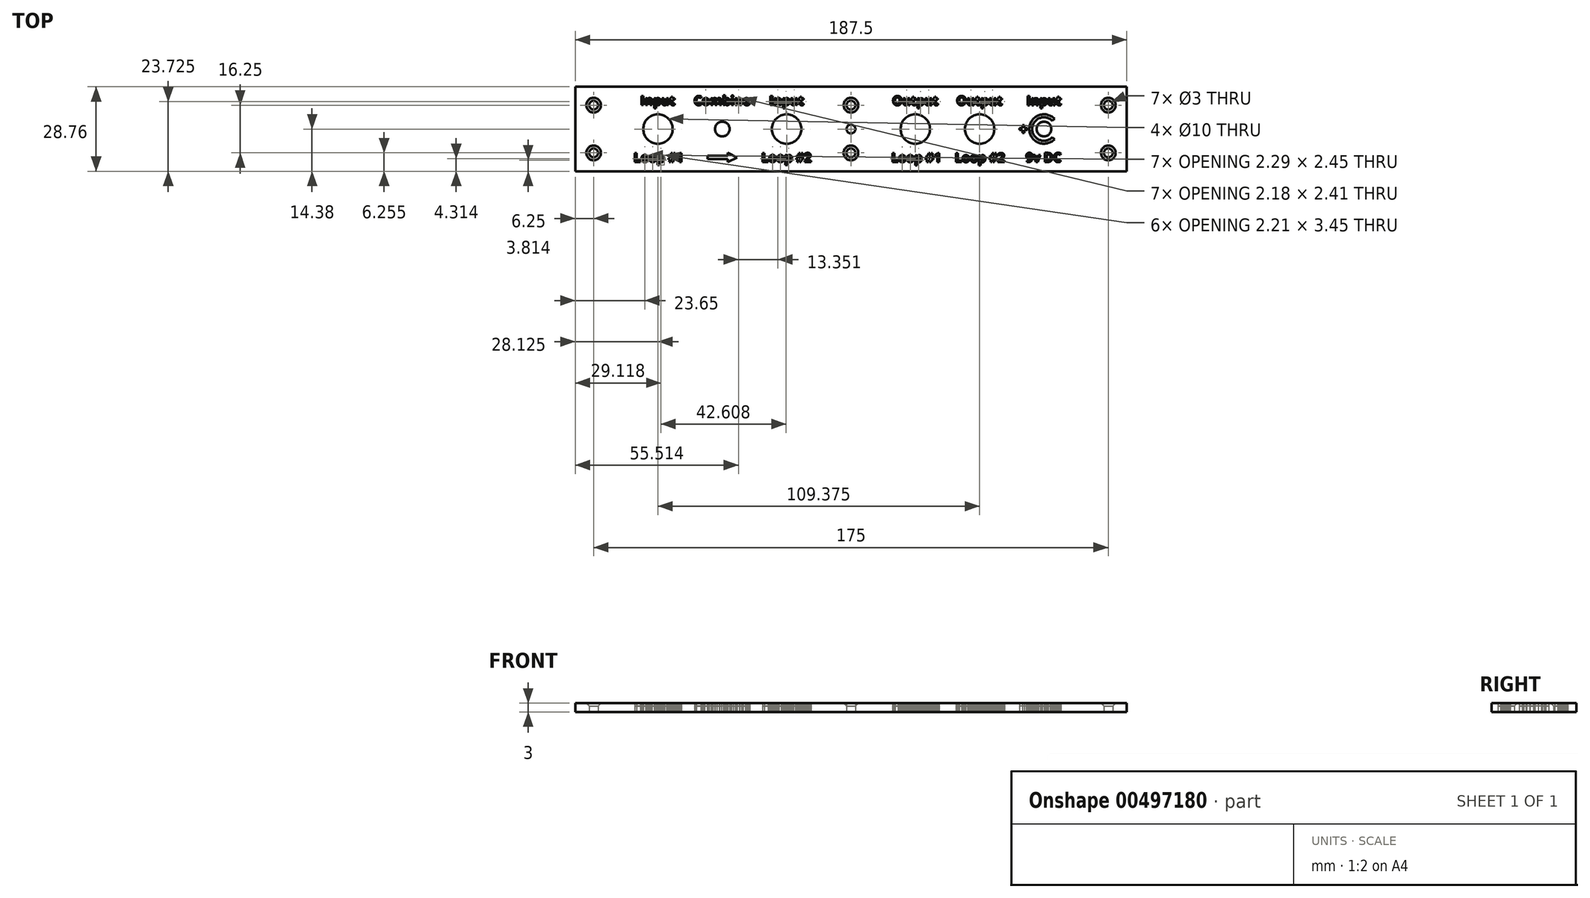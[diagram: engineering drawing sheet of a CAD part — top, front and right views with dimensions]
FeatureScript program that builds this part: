
annotation { "Feature Type Name" : "Feature", "Feature Type Description" : "" }
export const myFeature = defineFeature(function(context is Context, id is Id, definition is map)
    precondition{}
    {
        {
            var Q0;
            Q0=qCreatedBy(makeId("Top.planeOp"),FACE);
            var sketch = newSketch(context, id + "F0", { "sketchPlane" : qUnion([Q0])});
            skLineSegment(sketch, "E0.bottom", {"start": v(-93.75, 14.38) * mm, "end": v(93.75, 14.38) * mm});
            skLineSegment(sketch, "E0.top", {"start": v(-93.75, -14.37) * mm, "end": v(93.75, -14.37) * mm});
            skLineSegment(sketch, "E0.left", {"start": v(-93.75, 14.38) * mm, "end": v(-93.75, -14.37) * mm});
            skLineSegment(sketch, "E0.right", {"start": v(93.75, 14.38) * mm, "end": v(93.75, -14.37) * mm});
            skPoint(sketch, "E0.middle", {"position": v(0, 0) * mm});
            skPoint(sketch, "E1", {"position": v(-87.5, 14.38) * mm});
            skPoint(sketch, "E2", {"position": v(-87.5, -14.37) * mm});
            skPoint(sketch, "E3", {"position": v(87.5, 14.38) * mm});
            skPoint(sketch, "E4", {"position": v(87.5, -14.37) * mm});
            skPoint(sketch, "E5", {"position": v(-93.75, 8.12) * mm});
            skPoint(sketch, "E6", {"position": v(93.75, 8.13) * mm});
            skPoint(sketch, "E7", {"position": v(93.75, -8.13) * mm});
            skPoint(sketch, "E8", {"position": v(-93.75, -8.13) * mm});
            skPoint(sketch, "E9", {"position": v(-87.5, 8.12) * mm});
            skPoint(sketch, "E10", {"position": v(-87.5, -8.13) * mm});
            skPoint(sketch, "E11", {"position": v(87.5, 8.13) * mm});
            skPoint(sketch, "E12", {"position": v(87.5, -8.13) * mm});
            skLineSegment(sketch, "E13", {"start": v(-87.5, 8.12) * mm, "end": v(87.5, 8.13) * mm, "construction": true});
            skLineSegment(sketch, "E14", {"start": v(87.5, 8.13) * mm, "end": v(87.5, -8.13) * mm, "construction": true});
            skLineSegment(sketch, "E15", {"start": v(87.5, -8.13) * mm, "end": v(-87.5, -8.13) * mm, "construction": true});
            skLineSegment(sketch, "E16", {"start": v(-87.5, -8.13) * mm, "end": v(-87.5, 8.12) * mm, "construction": true});
            skPoint(sketch, "E17", {"position": v(0, 8.12) * mm});
            skPoint(sketch, "E18", {"position": v(0, -8.13) * mm});
            skLineSegment(sketch, "E19", {"start": v(0, 8.12) * mm, "end": v(0, -8.13) * mm, "construction": true});
            skPoint(sketch, "E20", {"position": v(-43.75, 8.13) * mm});
            skPoint(sketch, "E21", {"position": v(-43.75, -8.12) * mm});
            skPoint(sketch, "E22", {"position": v(43.75, 8.13) * mm});
            skPoint(sketch, "E23", {"position": v(43.75, -8.12) * mm});
            skPoint(sketch, "E24", {"position": v(-65.62, -8.12) * mm});
            skPoint(sketch, "E25", {"position": v(-65.62, 8.13) * mm});
            skPoint(sketch, "E26", {"position": v(-21.88, 8.13) * mm});
            skPoint(sketch, "E27", {"position": v(-21.88, -8.12) * mm});
            skPoint(sketch, "E28", {"position": v(21.88, 8.13) * mm});
            skPoint(sketch, "E29", {"position": v(21.88, -8.12) * mm});
            skPoint(sketch, "E30", {"position": v(65.62, 8.13) * mm});
            skPoint(sketch, "E31", {"position": v(65.62, -8.12) * mm});
            skLineSegment(sketch, "E32", {"start": v(-65.62, 8.13) * mm, "end": v(-65.62, -8.12) * mm, "construction": true});
            skLineSegment(sketch, "E33", {"start": v(-43.75, 8.12) * mm, "end": v(-43.75, -8.12) * mm, "construction": true});
            skLineSegment(sketch, "E34", {"start": v(-21.88, 8.13) * mm, "end": v(-21.88, -8.12) * mm, "construction": true});
            skLineSegment(sketch, "E35", {"start": v(21.88, 8.13) * mm, "end": v(21.88, -8.12) * mm, "construction": true});
            skLineSegment(sketch, "E36", {"start": v(43.75, 8.13) * mm, "end": v(43.75, -8.12) * mm, "construction": true});
            skLineSegment(sketch, "E37", {"start": v(65.62, 8.13) * mm, "end": v(65.62, -8.12) * mm, "construction": true});
            skPoint(sketch, "E38", {"position": v(65.62, 0) * mm});
            skPoint(sketch, "E39", {"position": v(43.75, 0) * mm});
            skPoint(sketch, "E40", {"position": v(21.88, 0) * mm});
            skPoint(sketch, "E41", {"position": v(-21.88, 0) * mm});
            skPoint(sketch, "E42", {"position": v(-43.75, 0) * mm});
            skPoint(sketch, "E43", {"position": v(-65.62, 0) * mm});
            skCircle(sketch, "E44", {"center": v(-65.62, 0) * mm, "radius": 5 * mm});
            skCircle(sketch, "E45", {"center": v(-21.88, 0) * mm, "radius": 5 * mm});
            skCircle(sketch, "E46", {"center": v(21.88, 0) * mm, "radius": 5 * mm});
            skCircle(sketch, "E47", {"center": v(43.75, 0) * mm, "radius": 5 * mm});
            skCircle(sketch, "E48", {"center": v(65.62, 0) * mm, "radius": 2.5 * mm});
            skCircle(sketch, "E49", {"center": v(0, 0) * mm, "radius": 1.5 * mm});
            skCircle(sketch, "E50", {"center": v(-43.75, 0) * mm, "radius": 2.5 * mm});
            skPoint(sketch, "E51", {"position": v(-65.62, 11.25) * mm});
            skPoint(sketch, "E52", {"position": v(-65.62, -11.25) * mm});
            skPoint(sketch, "E53", {"position": v(-43.75, -11.25) * mm});
            skPoint(sketch, "E54", {"position": v(-21.88, -11.25) * mm});
            skPoint(sketch, "E55", {"position": v(0, -11.25) * mm});
            skPoint(sketch, "E56", {"position": v(-43.75, 11.25) * mm});
            skPoint(sketch, "E57", {"position": v(-21.88, 11.25) * mm});
            skPoint(sketch, "E58", {"position": v(0, 11.25) * mm});
            skPoint(sketch, "E59", {"position": v(21.88, 11.25) * mm});
            skPoint(sketch, "E60", {"position": v(21.88, -11.25) * mm});
            skPoint(sketch, "E61", {"position": v(43.75, 11.25) * mm});
            skPoint(sketch, "E62", {"position": v(65.62, 11.25) * mm});
            skPoint(sketch, "E63", {"position": v(43.75, -11.25) * mm});
            skPoint(sketch, "E64", {"position": v(65.62, -11.25) * mm});
            skPoint(sketch, "E65", {"position": v(-73.89, -8.12) * mm});
            skPoint(sketch, "E66", {"position": v(-73.89, -11.25) * mm});
            skText(sketch, "E67", { "text": "Loop #1", "fontName": "OpenSans-Bold.ttf"});
            skPoint(sketch, "E68", {"position": v(-30.43, -8.12) * mm});
            skPoint(sketch, "E69", {"position": v(-30.43, -11.25) * mm});
            skText(sketch, "E70", { "text": "Loop #2", "fontName": "OpenSans-Bold.ttf"});
            skPoint(sketch, "E71", {"position": v(-71.6, 8.14) * mm});
            skPoint(sketch, "E72", {"position": v(-71.6, 11.27) * mm});
            skText(sketch, "E73", { "text": "Input", "fontName": "OpenSans-Bold.ttf"});
            skPoint(sketch, "E74", {"position": v(-53.43, 8.14) * mm});
            skPoint(sketch, "E75", {"position": v(-53.43, 11.27) * mm});
            skText(sketch, "E76", { "text": "Combine", "fontName": "OpenSans-Bold.ttf"});
            skPoint(sketch, "E77", {"position": v(-27.75, 8.14) * mm});
            skPoint(sketch, "E78", {"position": v(-27.75, 11.27) * mm});
            skText(sketch, "E79", { "text": "Input", "fontName": "OpenSans-Bold.ttf"});
            skPoint(sketch, "E80", {"position": v(-41.87, -8.12) * mm});
            skPoint(sketch, "E81", {"position": v(-41.87, -11.25) * mm});
            skPoint(sketch, "E82", {"position": v(-41.87, -9.12) * mm});
            skLineSegment(sketch, "E83", {"start": v(-41.87, -11.25) * mm, "end": v(-41.87, -10.25) * mm});
            skLineSegment(sketch, "E84", {"start": v(-41.87, -8.12) * mm, "end": v(-41.87, -9.12) * mm});
            skPoint(sketch, "E85", {"position": v(-48.75, -9.12) * mm});
            skPoint(sketch, "E86", {"position": v(-48.75, -10.25) * mm});
            skLineSegment(sketch, "E87", {"start": v(-41.87, -9.12) * mm, "end": v(-48.75, -9.12) * mm});
            skLineSegment(sketch, "E88", {"start": v(-41.87, -10.25) * mm, "end": v(-48.75, -10.25) * mm});
            skLineSegment(sketch, "E89", {"start": v(-48.75, -10.25) * mm, "end": v(-48.75, -9.12) * mm});
            skPoint(sketch, "E90", {"position": v(-38.75, -9.69) * mm});
            skLineSegment(sketch, "E91", {"start": v(-41.87, -8.12) * mm, "end": v(-38.75, -9.69) * mm});
            skLineSegment(sketch, "E92", {"start": v(-41.87, -11.25) * mm, "end": v(-38.75, -9.69) * mm});
            skPoint(sketch, "E93", {"position": v(-6.94, 2.58) * mm});
            skPoint(sketch, "E94", {"position": v(-6.94, 5.7) * mm});
            skPoint(sketch, "E95", {"position": v(14.05, 8.12) * mm});
            skPoint(sketch, "E96", {"position": v(14.05, 11.25) * mm});
            skText(sketch, "E97", { "text": "Output", "fontName": "OpenSans-Bold.ttf"});
            skPoint(sketch, "E98", {"position": v(35.87, 8.12) * mm});
            skPoint(sketch, "E99", {"position": v(35.87, 11.25) * mm});
            skText(sketch, "E100", { "text": "Output", "fontName": "OpenSans-Bold.ttf"});
            skPoint(sketch, "E101", {"position": v(59.74, 8.11) * mm});
            skPoint(sketch, "E102", {"position": v(59.74, 11.24) * mm});
            skText(sketch, "E103", { "text": "Input", "fontName": "OpenSans-Bold.ttf"});
            skPoint(sketch, "E104", {"position": v(59.47, -11.22) * mm});
            skPoint(sketch, "E105", {"position": v(59.47, -8.1) * mm});
            skText(sketch, "E106", { "text": "9v DC", "fontName": "OpenSans-Bold.ttf"});
            skPoint(sketch, "E107", {"position": v(13.69, -11.28) * mm});
            skPoint(sketch, "E108", {"position": v(13.69, -8.15) * mm});
            skText(sketch, "E109", { "text": "Loop #1", "fontName": "OpenSans-Bold.ttf"});
            skPoint(sketch, "E110", {"position": v(35.29, -11.28) * mm});
            skPoint(sketch, "E111", {"position": v(35.29, -8.15) * mm});
            skText(sketch, "E112", { "text": "Loop #2", "fontName": "OpenSans-Bold.ttf"});
            skCircle(sketch, "E113", {"center": v(65.62, 0) * mm, "radius": 4 * mm});
            skCircle(sketch, "E114", {"center": v(65.62, 0) * mm, "radius": 5 * mm});
            skLineSegment(sketch, "E115", {"start": v(65.62, 0) * mm, "end": v(70.63, 0) * mm, "construction": true});
            skPoint(sketch, "E116", {"position": v(69.2, 3.5) * mm});
            skPoint(sketch, "E117", {"position": v(69.2, -3.5) * mm});
            skPoint(sketch, "E118", {"position": v(68.48, 2.8) * mm});
            skPoint(sketch, "E119", {"position": v(68.48, -2.8) * mm});
            skLineSegment(sketch, "E120", {"start": v(68.48, 2.8) * mm, "end": v(69.2, 3.5) * mm});
            skLineSegment(sketch, "E121", {"start": v(68.48, -2.8) * mm, "end": v(69.2, -3.5) * mm});
            skPoint(sketch, "E122", {"position": v(57, -1.92) * mm});
            skPoint(sketch, "E123", {"position": v(57, 2.08) * mm});
            skText(sketch, "E124", { "text": "+", "fontName": "OpenSans-Bold.ttf"});
            skLineSegment(sketch, "E125", {"start": v(65.62, 0) * mm, "end": v(60.3, 0) * mm, "construction": true});
            const initialGuessF0  = {"E67": [-0.07389, -0.01125, 1, 0, 0.00312], "E70": [-0.03043, -0.01125, 1, 0, 0.00312], "E73": [-0.0716, 0.00814, 1, 0, 0.00313], "E76": [-0.05343, 0.00814, 1, 0, 0.00312], "E79": [-0.02775, 0.00814, 1, 0, 0.00312], "E97": [0.01405, 0.00812, 1, 0, 0.00312], "E100": [0.03587, 0.00812, 1, 0, 0.00312], "E103": [0.05974, 0.00811, 1, 0, 0.00313], "E106": [0.05947, -0.01122, 1, 0, 0.00313], "E109": [0.01369, -0.01128, 1, 0, 0.00312], "E112": [0.03529, -0.01128, 1, 0, 0.00313], "E124": [0.057, -0.00192, 1, 0, 0.004]};
            skSetInitialGuess(sketch, initialGuessF0);
            skSolve(sketch);
        }
        {
            var Q0;
            Q0=makeQuery(id+"F0.imprint","IMPRINT",FACE,{"disambiguationData":[TD([[makeQuery(id+"F0.imprint","IMPRINT",EDGE,{"derivedFrom":sQuery(id+"F0.wireOp",EDGE,"E73.sketch_text.stroke-0")}),-1.0]])]});
            var Q1;
            Q1=makeQuery(id+"F0.imprint","IMPRINT",FACE,{"disambiguationData":[TD([[makeQuery(id+"F0.imprint","IMPRINT",EDGE,{"derivedFrom":sQuery(id+"F0.wireOp",EDGE,"E73.sketch_text.stroke-4")}),-1.0]])]});
            var Q2;
            Q2=makeQuery(id+"F0.imprint","IMPRINT",FACE,{"disambiguationData":[TD([[makeQuery(id+"F0.imprint","IMPRINT",EDGE,{"derivedFrom":sQuery(id+"F0.wireOp",EDGE,"E73.sketch_text.stroke-21")}),-1.0]])]});
            var Q3;
            Q3=makeQuery(id+"F0.imprint","IMPRINT",FACE,{"disambiguationData":[TD([[makeQuery(id+"F0.imprint","IMPRINT",EDGE,{"derivedFrom":sQuery(id+"F0.wireOp",EDGE,"E73.sketch_text.stroke-44")}),-1.0]])]});
            var Q4;
            Q4=makeQuery(id+"F0.imprint","IMPRINT",FACE,{"disambiguationData":[TD([[makeQuery(id+"F0.imprint","IMPRINT",EDGE,{"derivedFrom":sQuery(id+"F0.wireOp",EDGE,"E73.sketch_text.stroke-61")}),-1.0]])]});
            var Q5;
            Q5=makeQuery(id+"F0.imprint","IMPRINT",FACE,{"disambiguationData":[TD([[makeQuery(id+"F0.imprint","IMPRINT",EDGE,{"derivedFrom":sQuery(id+"F0.wireOp",EDGE,"E76.sketch_text.stroke-0")}),-1.0]])]});
            var Q6;
            Q6=makeQuery(id+"F0.imprint","IMPRINT",FACE,{"disambiguationData":[TD([[makeQuery(id+"F0.imprint","IMPRINT",EDGE,{"derivedFrom":sQuery(id+"F0.wireOp",EDGE,"E76.sketch_text.stroke-15")}),-1.0]])]});
            var Q7;
            Q7=makeQuery(id+"F0.imprint","IMPRINT",FACE,{"disambiguationData":[TD([[makeQuery(id+"F0.imprint","IMPRINT",EDGE,{"derivedFrom":sQuery(id+"F0.wireOp",EDGE,"E76.sketch_text.stroke-33")}),-1.0]])]});
            var Q8;
            Q8=makeQuery(id+"F0.imprint","IMPRINT",FACE,{"disambiguationData":[TD([[makeQuery(id+"F0.imprint","IMPRINT",EDGE,{"derivedFrom":sQuery(id+"F0.wireOp",EDGE,"E76.sketch_text.stroke-61")}),-1.0]])]});
            var Q9;
            Q9=makeQuery(id+"F0.imprint","IMPRINT",FACE,{"disambiguationData":[TD([[makeQuery(id+"F0.imprint","IMPRINT",EDGE,{"derivedFrom":sQuery(id+"F0.wireOp",EDGE,"E76.sketch_text.stroke-89")}),-1.0]])]});
            var Q10;
            Q10=makeQuery(id+"F0.imprint","IMPRINT",FACE,{"disambiguationData":[TD([[makeQuery(id+"F0.imprint","IMPRINT",EDGE,{"derivedFrom":sQuery(id+"F0.wireOp",EDGE,"E76.sketch_text.stroke-84")}),-1.0]])]});
            var Q11;
            Q11=makeQuery(id+"F0.imprint","IMPRINT",FACE,{"disambiguationData":[TD([[makeQuery(id+"F0.imprint","IMPRINT",EDGE,{"derivedFrom":sQuery(id+"F0.wireOp",EDGE,"E76.sketch_text.stroke-93")}),-1.0]])]});
            var Q12;
            Q12=makeQuery(id+"F0.imprint","IMPRINT",FACE,{"disambiguationData":[TD([[makeQuery(id+"F0.imprint","IMPRINT",EDGE,{"derivedFrom":sQuery(id+"F0.wireOp",EDGE,"E76.sketch_text.stroke-110")}),-1.0]])]});
            var Q13;
            Q13=makeQuery(id+"F0.imprint","IMPRINT",FACE,{"disambiguationData":[TD([[makeQuery(id+"F0.imprint","IMPRINT",EDGE,{"derivedFrom":sQuery(id+"F0.wireOp",EDGE,"E79.sketch_text.stroke-0")}),-1.0]])]});
            var Q14;
            Q14=makeQuery(id+"F0.imprint","IMPRINT",FACE,{"disambiguationData":[TD([[makeQuery(id+"F0.imprint","IMPRINT",EDGE,{"derivedFrom":sQuery(id+"F0.wireOp",EDGE,"E79.sketch_text.stroke-4")}),-1.0]])]});
            var Q15;
            Q15=makeQuery(id+"F0.imprint","IMPRINT",FACE,{"disambiguationData":[TD([[makeQuery(id+"F0.imprint","IMPRINT",EDGE,{"derivedFrom":sQuery(id+"F0.wireOp",EDGE,"E79.sketch_text.stroke-21")}),-1.0]])]});
            var Q16;
            Q16=makeQuery(id+"F0.imprint","IMPRINT",FACE,{"disambiguationData":[TD([[makeQuery(id+"F0.imprint","IMPRINT",EDGE,{"derivedFrom":sQuery(id+"F0.wireOp",EDGE,"E79.sketch_text.stroke-44")}),-1.0]])]});
            var Q17;
            Q17=makeQuery(id+"F0.imprint","IMPRINT",FACE,{"disambiguationData":[TD([[makeQuery(id+"F0.imprint","IMPRINT",EDGE,{"derivedFrom":sQuery(id+"F0.wireOp",EDGE,"E67.sketch_text.stroke-0")}),-1.0]])]});
            var Q18;
            Q18=makeQuery(id+"F0.imprint","IMPRINT",FACE,{"disambiguationData":[TD([[makeQuery(id+"F0.imprint","IMPRINT",EDGE,{"derivedFrom":sQuery(id+"F0.wireOp",EDGE,"E67.sketch_text.stroke-6")}),-1.0]])]});
            var Q19;
            Q19=makeQuery(id+"F0.imprint","IMPRINT",FACE,{"disambiguationData":[TD([[makeQuery(id+"F0.imprint","IMPRINT",EDGE,{"derivedFrom":sQuery(id+"F0.wireOp",EDGE,"E67.sketch_text.stroke-42")}),-1.0]])]});
            var Q20;
            Q20=makeQuery(id+"F0.imprint","IMPRINT",FACE,{"disambiguationData":[TD([[makeQuery(id+"F0.imprint","IMPRINT",EDGE,{"derivedFrom":sQuery(id+"F0.wireOp",EDGE,"E67.sketch_text.stroke-24")}),-1.0]])]});
            var Q21;
            Q21=makeQuery(id+"F0.imprint","IMPRINT",FACE,{"disambiguationData":[TD([[makeQuery(id+"F0.imprint","IMPRINT",EDGE,{"derivedFrom":sQuery(id+"F0.wireOp",EDGE,"E67.sketch_text.stroke-65")}),-1.0]])]});
            var Q22;
            Q22=makeQuery(id+"F0.imprint","IMPRINT",FACE,{"disambiguationData":[TD([[makeQuery(id+"F0.imprint","IMPRINT",EDGE,{"derivedFrom":sQuery(id+"F0.wireOp",EDGE,"E67.sketch_text.stroke-97")}),-1.0]])]});
            var Q23;
            Q23=makeQuery(id+"F0.imprint","IMPRINT",FACE,{"disambiguationData":[TD([[makeQuery(id+"F0.imprint","IMPRINT",EDGE,{"derivedFrom":sQuery(id+"F0.wireOp",EDGE,"E83")}),-1.0]])]});
            var Q24;
            Q24=makeQuery(id+"F0.imprint","IMPRINT",FACE,{"disambiguationData":[TD([[makeQuery(id+"F0.imprint","IMPRINT",EDGE,{"derivedFrom":sQuery(id+"F0.wireOp",EDGE,"E79.sketch_text.stroke-61")}),-1.0]])]});
            var Q25;
            Q25=makeQuery(id+"F0.imprint","IMPRINT",FACE,{"disambiguationData":[TD([[makeQuery(id+"F0.imprint","IMPRINT",EDGE,{"derivedFrom":sQuery(id+"F0.wireOp",EDGE,"E70.sketch_text.stroke-97")}),-1.0]])]});
            var Q26;
            Q26=makeQuery(id+"F0.imprint","IMPRINT",FACE,{"disambiguationData":[TD([[makeQuery(id+"F0.imprint","IMPRINT",EDGE,{"derivedFrom":sQuery(id+"F0.wireOp",EDGE,"E70.sketch_text.stroke-65")}),-1.0]])]});
            var Q27;
            Q27=makeQuery(id+"F0.imprint","IMPRINT",FACE,{"disambiguationData":[TD([[makeQuery(id+"F0.imprint","IMPRINT",EDGE,{"derivedFrom":sQuery(id+"F0.wireOp",EDGE,"E70.sketch_text.stroke-42")}),-1.0]])]});
            var Q28;
            Q28=makeQuery(id+"F0.imprint","IMPRINT",FACE,{"disambiguationData":[TD([[makeQuery(id+"F0.imprint","IMPRINT",EDGE,{"derivedFrom":sQuery(id+"F0.wireOp",EDGE,"E70.sketch_text.stroke-24")}),-1.0]])]});
            var Q29;
            Q29=makeQuery(id+"F0.imprint","IMPRINT",FACE,{"disambiguationData":[TD([[makeQuery(id+"F0.imprint","IMPRINT",EDGE,{"derivedFrom":sQuery(id+"F0.wireOp",EDGE,"E70.sketch_text.stroke-6")}),-1.0]])]});
            var Q30;
            Q30=makeQuery(id+"F0.imprint","IMPRINT",FACE,{"disambiguationData":[TD([[makeQuery(id+"F0.imprint","IMPRINT",EDGE,{"derivedFrom":sQuery(id+"F0.wireOp",EDGE,"E70.sketch_text.stroke-0")}),-1.0]])]});
            var Q31;
            Q31=makeQuery(id+"F0.imprint","IMPRINT",FACE,{"disambiguationData":[TD([[makeQuery(id+"F0.imprint","IMPRINT",EDGE,{"derivedFrom":sQuery(id+"F0.wireOp",EDGE,"ed6ad51a-24f1-4634-a6e9-502759cafa60.sketch_text.stroke-0")}),-1.0]])]});
            var Q32;
            Q32=makeQuery(id+"F0.imprint","IMPRINT",FACE,{"disambiguationData":[TD([[makeQuery(id+"F0.imprint","IMPRINT",EDGE,{"derivedFrom":sQuery(id+"F0.wireOp",EDGE,"ed6ad51a-24f1-4634-a6e9-502759cafa60.sketch_text.stroke-16")}),-1.0]])]});
            var Q33;
            Q33=makeQuery(id+"F0.imprint","IMPRINT",FACE,{"disambiguationData":[TD([[makeQuery(id+"F0.imprint","IMPRINT",EDGE,{"derivedFrom":sQuery(id+"F0.wireOp",EDGE,"ed6ad51a-24f1-4634-a6e9-502759cafa60.sketch_text.stroke-34")}),-1.0]])]});
            var Q34;
            Q34=makeQuery(id+"F0.imprint","IMPRINT",FACE,{"disambiguationData":[TD([[makeQuery(id+"F0.imprint","IMPRINT",EDGE,{"derivedFrom":sQuery(id+"F0.wireOp",EDGE,"ed6ad51a-24f1-4634-a6e9-502759cafa60.sketch_text.stroke-60")}),-1.0]])]});
            var Q35;
            Q35=makeQuery(id+"F0.imprint","IMPRINT",FACE,{"disambiguationData":[TD([[makeQuery(id+"F0.imprint","IMPRINT",EDGE,{"derivedFrom":sQuery(id+"F0.wireOp",EDGE,"ed6ad51a-24f1-4634-a6e9-502759cafa60.sketch_text.stroke-80")}),-1.0]])]});
            var Q36;
            Q36=makeQuery(id+"F0.imprint","IMPRINT",FACE,{"disambiguationData":[TD([[makeQuery(id+"F0.imprint","IMPRINT",EDGE,{"derivedFrom":sQuery(id+"F0.wireOp",EDGE,"E97.sketch_text.stroke-0")}),-1.0]])]});
            var Q37;
            Q37=makeQuery(id+"F0.imprint","IMPRINT",FACE,{"disambiguationData":[TD([[makeQuery(id+"F0.imprint","IMPRINT",EDGE,{"derivedFrom":sQuery(id+"F0.wireOp",EDGE,"E97.sketch_text.stroke-14")}),-1.0]])]});
            var Q38;
            Q38=makeQuery(id+"F0.imprint","IMPRINT",FACE,{"disambiguationData":[TD([[makeQuery(id+"F0.imprint","IMPRINT",EDGE,{"derivedFrom":sQuery(id+"F0.wireOp",EDGE,"E97.sketch_text.stroke-31")}),-1.0]])]});
            var Q39;
            Q39=makeQuery(id+"F0.imprint","IMPRINT",FACE,{"disambiguationData":[TD([[makeQuery(id+"F0.imprint","IMPRINT",EDGE,{"derivedFrom":sQuery(id+"F0.wireOp",EDGE,"E97.sketch_text.stroke-49")}),-1.0]])]});
            var Q40;
            Q40=makeQuery(id+"F0.imprint","IMPRINT",FACE,{"disambiguationData":[TD([[makeQuery(id+"F0.imprint","IMPRINT",EDGE,{"derivedFrom":sQuery(id+"F0.wireOp",EDGE,"E97.sketch_text.stroke-72")}),-1.0]])]});
            var Q41;
            Q41=makeQuery(id+"F0.imprint","IMPRINT",FACE,{"disambiguationData":[TD([[makeQuery(id+"F0.imprint","IMPRINT",EDGE,{"derivedFrom":sQuery(id+"F0.wireOp",EDGE,"E97.sketch_text.stroke-89")}),-1.0]])]});
            var Q42;
            Q42=makeQuery(id+"F0.imprint","IMPRINT",FACE,{"disambiguationData":[TD([[makeQuery(id+"F0.imprint","IMPRINT",EDGE,{"derivedFrom":sQuery(id+"F0.wireOp",EDGE,"E109.sketch_text.stroke-0")}),-1.0]])]});
            var Q43;
            Q43=makeQuery(id+"F0.imprint","IMPRINT",FACE,{"disambiguationData":[TD([[makeQuery(id+"F0.imprint","IMPRINT",EDGE,{"derivedFrom":sQuery(id+"F0.wireOp",EDGE,"E109.sketch_text.stroke-6")}),-1.0]])]});
            var Q44;
            Q44=makeQuery(id+"F0.imprint","IMPRINT",FACE,{"disambiguationData":[TD([[makeQuery(id+"F0.imprint","IMPRINT",EDGE,{"derivedFrom":sQuery(id+"F0.wireOp",EDGE,"E109.sketch_text.stroke-24")}),-1.0]])]});
            var Q45;
            Q45=makeQuery(id+"F0.imprint","IMPRINT",FACE,{"disambiguationData":[TD([[makeQuery(id+"F0.imprint","IMPRINT",EDGE,{"derivedFrom":sQuery(id+"F0.wireOp",EDGE,"E109.sketch_text.stroke-42")}),-1.0]])]});
            var Q46;
            Q46=makeQuery(id+"F0.imprint","IMPRINT",FACE,{"disambiguationData":[TD([[makeQuery(id+"F0.imprint","IMPRINT",EDGE,{"derivedFrom":sQuery(id+"F0.wireOp",EDGE,"E109.sketch_text.stroke-65")}),-1.0]])]});
            var Q47;
            Q47=makeQuery(id+"F0.imprint","IMPRINT",FACE,{"disambiguationData":[TD([[makeQuery(id+"F0.imprint","IMPRINT",EDGE,{"derivedFrom":sQuery(id+"F0.wireOp",EDGE,"E109.sketch_text.stroke-97")}),-1.0]])]});
            var Q48;
            Q48=makeQuery(id+"F0.imprint","IMPRINT",FACE,{"disambiguationData":[TD([[makeQuery(id+"F0.imprint","IMPRINT",EDGE,{"derivedFrom":sQuery(id+"F0.wireOp",EDGE,"E100.sketch_text.stroke-0")}),-1.0]])]});
            var Q49;
            Q49=makeQuery(id+"F0.imprint","IMPRINT",FACE,{"disambiguationData":[TD([[makeQuery(id+"F0.imprint","IMPRINT",EDGE,{"derivedFrom":sQuery(id+"F0.wireOp",EDGE,"E100.sketch_text.stroke-14")}),-1.0]])]});
            var Q50;
            Q50=makeQuery(id+"F0.imprint","IMPRINT",FACE,{"disambiguationData":[TD([[makeQuery(id+"F0.imprint","IMPRINT",EDGE,{"derivedFrom":sQuery(id+"F0.wireOp",EDGE,"E100.sketch_text.stroke-31")}),-1.0]])]});
            var Q51;
            Q51=makeQuery(id+"F0.imprint","IMPRINT",FACE,{"disambiguationData":[TD([[makeQuery(id+"F0.imprint","IMPRINT",EDGE,{"derivedFrom":sQuery(id+"F0.wireOp",EDGE,"E100.sketch_text.stroke-49")}),-1.0]])]});
            var Q52;
            Q52=makeQuery(id+"F0.imprint","IMPRINT",FACE,{"disambiguationData":[TD([[makeQuery(id+"F0.imprint","IMPRINT",EDGE,{"derivedFrom":sQuery(id+"F0.wireOp",EDGE,"E112.sketch_text.stroke-0")}),-1.0]])]});
            var Q53;
            Q53=makeQuery(id+"F0.imprint","IMPRINT",FACE,{"disambiguationData":[TD([[makeQuery(id+"F0.imprint","IMPRINT",EDGE,{"derivedFrom":sQuery(id+"F0.wireOp",EDGE,"E112.sketch_text.stroke-6")}),-1.0]])]});
            var Q54;
            Q54=makeQuery(id+"F0.imprint","IMPRINT",FACE,{"disambiguationData":[TD([[makeQuery(id+"F0.imprint","IMPRINT",EDGE,{"derivedFrom":sQuery(id+"F0.wireOp",EDGE,"E112.sketch_text.stroke-24")}),-1.0]])]});
            var Q55;
            Q55=makeQuery(id+"F0.imprint","IMPRINT",FACE,{"disambiguationData":[TD([[makeQuery(id+"F0.imprint","IMPRINT",EDGE,{"derivedFrom":sQuery(id+"F0.wireOp",EDGE,"E112.sketch_text.stroke-42")}),-1.0]])]});
            var Q56;
            Q56=makeQuery(id+"F0.imprint","IMPRINT",FACE,{"disambiguationData":[TD([[makeQuery(id+"F0.imprint","IMPRINT",EDGE,{"derivedFrom":sQuery(id+"F0.wireOp",EDGE,"E100.sketch_text.stroke-72")}),-1.0]])]});
            var Q57;
            Q57=makeQuery(id+"F0.imprint","IMPRINT",FACE,{"disambiguationData":[TD([[makeQuery(id+"F0.imprint","IMPRINT",EDGE,{"derivedFrom":sQuery(id+"F0.wireOp",EDGE,"E100.sketch_text.stroke-89")}),-1.0]])]});
            var Q58;
            Q58=makeQuery(id+"F0.imprint","IMPRINT",FACE,{"disambiguationData":[TD([[makeQuery(id+"F0.imprint","IMPRINT",EDGE,{"derivedFrom":sQuery(id+"F0.wireOp",EDGE,"E112.sketch_text.stroke-65")}),-1.0]])]});
            var Q59;
            Q59=makeQuery(id+"F0.imprint","IMPRINT",FACE,{"disambiguationData":[TD([[makeQuery(id+"F0.imprint","IMPRINT",EDGE,{"derivedFrom":sQuery(id+"F0.wireOp",EDGE,"E112.sketch_text.stroke-97")}),-1.0]])]});
            var Q60;
            Q60=makeQuery(id+"F0.imprint","IMPRINT",FACE,{"disambiguationData":[TD([[makeQuery(id+"F0.imprint","IMPRINT",EDGE,{"derivedFrom":sQuery(id+"F0.wireOp",EDGE,"E124.sketch_text.stroke-0")}),-1.0]])]});
            var Q61;
            Q61=makeQuery(id+"F0.imprint","IMPRINT",FACE,{"disambiguationData":[TD([[makeQuery(id+"F0.imprint","IMPRINT",EDGE,{"derivedFrom":sQuery(id+"F0.wireOp",EDGE,"E106.sketch_text.stroke-0")}),-1.0]])]});
            var Q62;
            Q62=makeQuery(id+"F0.imprint","IMPRINT",FACE,{"disambiguationData":[TD([[makeQuery(id+"F0.imprint","IMPRINT",EDGE,{"derivedFrom":sQuery(id+"F0.wireOp",EDGE,"E106.sketch_text.stroke-26")}),-1.0]])]});
            var Q63;
            Q63=makeQuery(id+"F0.imprint","IMPRINT",FACE,{"disambiguationData":[TD([[makeQuery(id+"F0.imprint","IMPRINT",EDGE,{"derivedFrom":sQuery(id+"F0.wireOp",EDGE,"E106.sketch_text.stroke-36")}),-1.0]])]});
            var Q64;
            Q64=makeQuery(id+"F0.imprint","IMPRINT",FACE,{"disambiguationData":[TD([[makeQuery(id+"F0.imprint","IMPRINT",EDGE,{"derivedFrom":sQuery(id+"F0.wireOp",EDGE,"E106.sketch_text.stroke-48")}),-1.0]])]});
            var Q65;
            {var subQ0=sQuery(id+"F0.wireOp",EDGE,"E120");Q65=makeQuery(id+"F0.imprint","IMPRINT",FACE,{"disambiguationData":[TD([[makeQuery(id+"F0.imprint","IMPRINT",EDGE,{"derivedFrom":subQ0}),1.0]])]});}
            var Q66;
            Q66=makeQuery(id+"F0.imprint","IMPRINT",FACE,{"disambiguationData":[TD([[makeQuery(id+"F0.imprint","IMPRINT",EDGE,{"derivedFrom":sQuery(id+"F0.wireOp",EDGE,"E103.sketch_text.stroke-0")}),-1.0]])]});
            var Q67;
            Q67=makeQuery(id+"F0.imprint","IMPRINT",FACE,{"disambiguationData":[TD([[makeQuery(id+"F0.imprint","IMPRINT",EDGE,{"derivedFrom":sQuery(id+"F0.wireOp",EDGE,"E103.sketch_text.stroke-4")}),-1.0]])]});
            var Q68;
            Q68=makeQuery(id+"F0.imprint","IMPRINT",FACE,{"disambiguationData":[TD([[makeQuery(id+"F0.imprint","IMPRINT",EDGE,{"derivedFrom":sQuery(id+"F0.wireOp",EDGE,"E103.sketch_text.stroke-21")}),-1.0]])]});
            var Q69;
            Q69=makeQuery(id+"F0.imprint","IMPRINT",FACE,{"disambiguationData":[TD([[makeQuery(id+"F0.imprint","IMPRINT",EDGE,{"derivedFrom":sQuery(id+"F0.wireOp",EDGE,"E103.sketch_text.stroke-44")}),-1.0]])]});
            var Q70;
            Q70=makeQuery(id+"F0.imprint","IMPRINT",FACE,{"disambiguationData":[TD([[makeQuery(id+"F0.imprint","IMPRINT",EDGE,{"derivedFrom":sQuery(id+"F0.wireOp",EDGE,"E103.sketch_text.stroke-61")}),-1.0]])]});
            extrude(context, id + "F1", {"entities" : qUnion([Q0, Q1, Q2, Q3, Q4, Q5, Q6, Q7, Q8, Q9, Q10, Q11, Q12, Q13, Q14, Q15, Q16, Q17, Q18, Q19, Q20, Q21, Q22, Q23, Q24, Q25, Q26, Q27, Q28, Q29, Q30, Q31, Q32, Q33, Q34, Q35, Q36, Q37, Q38, Q39, Q40, Q41, Q42, Q43, Q44, Q45, Q46, Q47, Q48, Q49, Q50, Q51, Q52, Q53, Q54, Q55, Q56, Q57, Q58, Q59, Q60, Q61, Q62, Q63, Q64, Q65, Q66, Q67, Q68, Q69, Q70]), "depth" : 2 * mm});
        }
        {
            var Q0;
            {var subQ0=sQuery(id+"F0.wireOp",EDGE,"E120");Q0=makeQuery(id+"F0.imprint","IMPRINT",FACE,{"disambiguationData":[TD([[makeQuery(id+"F0.imprint","IMPRINT",EDGE,{"derivedFrom":subQ0}),-1.0]])]});}
            var Q1;
            Q1=makeQuery(id+"F0.imprint","IMPRINT",FACE,{"disambiguationData":[TD([[makeQuery(id+"F0.imprint","IMPRINT",EDGE,{"derivedFrom":sQuery(id+"F0.wireOp",EDGE,"E0.bottom")}),-1.0]])]});
            var Q2;
            Q2=makeQuery(id+"F0.imprint","IMPRINT",FACE,{"disambiguationData":[TD([[makeQuery(id+"F0.imprint","IMPRINT",EDGE,{"derivedFrom":sQuery(id+"F0.wireOp",EDGE,"E73.sketch_text.stroke-36")}),1.0]])]});
            var Q3;
            Q3=makeQuery(id+"F0.imprint","IMPRINT",FACE,{"disambiguationData":[TD([[makeQuery(id+"F0.imprint","IMPRINT",EDGE,{"derivedFrom":sQuery(id+"F0.wireOp",EDGE,"E76.sketch_text.stroke-15")}),1.0]])]});
            var Q4;
            Q4=makeQuery(id+"F0.imprint","IMPRINT",FACE,{"disambiguationData":[TD([[makeQuery(id+"F0.imprint","IMPRINT",EDGE,{"derivedFrom":sQuery(id+"F0.wireOp",EDGE,"E76.sketch_text.stroke-75")}),1.0]])]});
            var Q5;
            Q5=makeQuery(id+"F0.imprint","IMPRINT",FACE,{"disambiguationData":[TD([[makeQuery(id+"F0.imprint","IMPRINT",EDGE,{"derivedFrom":sQuery(id+"F0.wireOp",EDGE,"E76.sketch_text.stroke-110")}),1.0]])]});
            var Q6;
            Q6=makeQuery(id+"F0.imprint","IMPRINT",FACE,{"disambiguationData":[TD([[makeQuery(id+"F0.imprint","IMPRINT",EDGE,{"derivedFrom":sQuery(id+"F0.wireOp",EDGE,"E67.sketch_text.stroke-6")}),1.0]])]});
            var Q7;
            Q7=makeQuery(id+"F0.imprint","IMPRINT",FACE,{"disambiguationData":[TD([[makeQuery(id+"F0.imprint","IMPRINT",EDGE,{"derivedFrom":sQuery(id+"F0.wireOp",EDGE,"E67.sketch_text.stroke-24")}),1.0]])]});
            var Q8;
            Q8=makeQuery(id+"F0.imprint","IMPRINT",FACE,{"disambiguationData":[TD([[makeQuery(id+"F0.imprint","IMPRINT",EDGE,{"derivedFrom":sQuery(id+"F0.wireOp",EDGE,"E67.sketch_text.stroke-57")}),1.0]])]});
            var Q9;
            Q9=makeQuery(id+"F0.imprint","IMPRINT",FACE,{"disambiguationData":[TD([[makeQuery(id+"F0.imprint","IMPRINT",EDGE,{"derivedFrom":sQuery(id+"F0.wireOp",EDGE,"E67.sketch_text.stroke-93")}),1.0]])]});
            var Q10;
            Q10=makeQuery(id+"F0.imprint","IMPRINT",FACE,{"disambiguationData":[TD([[makeQuery(id+"F0.imprint","IMPRINT",EDGE,{"derivedFrom":sQuery(id+"F0.wireOp",EDGE,"E70.sketch_text.stroke-6")}),1.0]])]});
            var Q11;
            Q11=makeQuery(id+"F0.imprint","IMPRINT",FACE,{"disambiguationData":[TD([[makeQuery(id+"F0.imprint","IMPRINT",EDGE,{"derivedFrom":sQuery(id+"F0.wireOp",EDGE,"E70.sketch_text.stroke-24")}),1.0]])]});
            var Q12;
            Q12=makeQuery(id+"F0.imprint","IMPRINT",FACE,{"disambiguationData":[TD([[makeQuery(id+"F0.imprint","IMPRINT",EDGE,{"derivedFrom":sQuery(id+"F0.wireOp",EDGE,"E70.sketch_text.stroke-57")}),1.0]])]});
            var Q13;
            Q13=makeQuery(id+"F0.imprint","IMPRINT",FACE,{"disambiguationData":[TD([[makeQuery(id+"F0.imprint","IMPRINT",EDGE,{"derivedFrom":sQuery(id+"F0.wireOp",EDGE,"E79.sketch_text.stroke-36")}),1.0]])]});
            var Q14;
            Q14=makeQuery(id+"F0.imprint","IMPRINT",FACE,{"disambiguationData":[TD([[makeQuery(id+"F0.imprint","IMPRINT",EDGE,{"derivedFrom":sQuery(id+"F0.wireOp",EDGE,"E70.sketch_text.stroke-93")}),1.0]])]});
            var Q15;
            Q15=makeQuery(id+"F0.imprint","IMPRINT",FACE,{"disambiguationData":[TD([[makeQuery(id+"F0.imprint","IMPRINT",EDGE,{"derivedFrom":sQuery(id+"F0.wireOp",EDGE,"ed6ad51a-24f1-4634-a6e9-502759cafa60.sketch_text.stroke-0")}),1.0]])]});
            var Q16;
            Q16=makeQuery(id+"F0.imprint","IMPRINT",FACE,{"disambiguationData":[TD([[makeQuery(id+"F0.imprint","IMPRINT",EDGE,{"derivedFrom":sQuery(id+"F0.wireOp",EDGE,"ed6ad51a-24f1-4634-a6e9-502759cafa60.sketch_text.stroke-16")}),1.0]])]});
            var Q17;
            Q17=makeQuery(id+"F0.imprint","IMPRINT",FACE,{"disambiguationData":[TD([[makeQuery(id+"F0.imprint","IMPRINT",EDGE,{"derivedFrom":sQuery(id+"F0.wireOp",EDGE,"ed6ad51a-24f1-4634-a6e9-502759cafa60.sketch_text.stroke-60")}),1.0]])]});
            var Q18;
            Q18=makeQuery(id+"F0.imprint","IMPRINT",FACE,{"disambiguationData":[TD([[makeQuery(id+"F0.imprint","IMPRINT",EDGE,{"derivedFrom":sQuery(id+"F0.wireOp",EDGE,"E97.sketch_text.stroke-8")}),1.0]])]});
            var Q19;
            Q19=makeQuery(id+"F0.imprint","IMPRINT",FACE,{"disambiguationData":[TD([[makeQuery(id+"F0.imprint","IMPRINT",EDGE,{"derivedFrom":sQuery(id+"F0.wireOp",EDGE,"E97.sketch_text.stroke-64")}),1.0]])]});
            var Q20;
            Q20=makeQuery(id+"F0.imprint","IMPRINT",FACE,{"disambiguationData":[TD([[makeQuery(id+"F0.imprint","IMPRINT",EDGE,{"derivedFrom":sQuery(id+"F0.wireOp",EDGE,"E109.sketch_text.stroke-6")}),1.0]])]});
            var Q21;
            Q21=makeQuery(id+"F0.imprint","IMPRINT",FACE,{"disambiguationData":[TD([[makeQuery(id+"F0.imprint","IMPRINT",EDGE,{"derivedFrom":sQuery(id+"F0.wireOp",EDGE,"E109.sketch_text.stroke-24")}),1.0]])]});
            var Q22;
            Q22=makeQuery(id+"F0.imprint","IMPRINT",FACE,{"disambiguationData":[TD([[makeQuery(id+"F0.imprint","IMPRINT",EDGE,{"derivedFrom":sQuery(id+"F0.wireOp",EDGE,"E109.sketch_text.stroke-57")}),1.0]])]});
            var Q23;
            Q23=makeQuery(id+"F0.imprint","IMPRINT",FACE,{"disambiguationData":[TD([[makeQuery(id+"F0.imprint","IMPRINT",EDGE,{"derivedFrom":sQuery(id+"F0.wireOp",EDGE,"E109.sketch_text.stroke-93")}),1.0]])]});
            var Q24;
            Q24=makeQuery(id+"F0.imprint","IMPRINT",FACE,{"disambiguationData":[TD([[makeQuery(id+"F0.imprint","IMPRINT",EDGE,{"derivedFrom":sQuery(id+"F0.wireOp",EDGE,"E100.sketch_text.stroke-8")}),1.0]])]});
            var Q25;
            Q25=makeQuery(id+"F0.imprint","IMPRINT",FACE,{"disambiguationData":[TD([[makeQuery(id+"F0.imprint","IMPRINT",EDGE,{"derivedFrom":sQuery(id+"F0.wireOp",EDGE,"E100.sketch_text.stroke-64")}),1.0]])]});
            var Q26;
            Q26=makeQuery(id+"F0.imprint","IMPRINT",FACE,{"disambiguationData":[TD([[makeQuery(id+"F0.imprint","IMPRINT",EDGE,{"derivedFrom":sQuery(id+"F0.wireOp",EDGE,"E112.sketch_text.stroke-6")}),1.0]])]});
            var Q27;
            Q27=makeQuery(id+"F0.imprint","IMPRINT",FACE,{"disambiguationData":[TD([[makeQuery(id+"F0.imprint","IMPRINT",EDGE,{"derivedFrom":sQuery(id+"F0.wireOp",EDGE,"E112.sketch_text.stroke-24")}),1.0]])]});
            var Q28;
            Q28=makeQuery(id+"F0.imprint","IMPRINT",FACE,{"disambiguationData":[TD([[makeQuery(id+"F0.imprint","IMPRINT",EDGE,{"derivedFrom":sQuery(id+"F0.wireOp",EDGE,"E112.sketch_text.stroke-57")}),1.0]])]});
            var Q29;
            Q29=makeQuery(id+"F0.imprint","IMPRINT",FACE,{"disambiguationData":[TD([[makeQuery(id+"F0.imprint","IMPRINT",EDGE,{"derivedFrom":sQuery(id+"F0.wireOp",EDGE,"E112.sketch_text.stroke-93")}),1.0]])]});
            var Q30;
            Q30=makeQuery(id+"F0.imprint","IMPRINT",FACE,{"disambiguationData":[TD([[makeQuery(id+"F0.imprint","IMPRINT",EDGE,{"derivedFrom":sQuery(id+"F0.wireOp",EDGE,"E48")}),-1.0]])]});
            var Q31;
            Q31=makeQuery(id+"F0.imprint","IMPRINT",FACE,{"disambiguationData":[TD([[makeQuery(id+"F0.imprint","IMPRINT",EDGE,{"derivedFrom":sQuery(id+"F0.wireOp",EDGE,"E106.sketch_text.stroke-18")}),1.0]])]});
            var Q32;
            Q32=makeQuery(id+"F0.imprint","IMPRINT",FACE,{"disambiguationData":[TD([[makeQuery(id+"F0.imprint","IMPRINT",EDGE,{"derivedFrom":sQuery(id+"F0.wireOp",EDGE,"E106.sketch_text.stroke-43")}),1.0]])]});
            var Q33;
            Q33=makeQuery(id+"F0.imprint","IMPRINT",FACE,{"disambiguationData":[TD([[makeQuery(id+"F0.imprint","IMPRINT",EDGE,{"derivedFrom":sQuery(id+"F0.wireOp",EDGE,"E103.sketch_text.stroke-36")}),1.0]])]});
            extrude(context, id + "F2", {"entities" : qUnion([Q0, Q1, Q2, Q3, Q4, Q5, Q6, Q7, Q8, Q9, Q10, Q11, Q12, Q13, Q14, Q15, Q16, Q17, Q18, Q19, Q20, Q21, Q22, Q23, Q24, Q25, Q26, Q27, Q28, Q29, Q30, Q31, Q32, Q33]), "depth" : 3 * mm});
        }
        {
            var Q0;
            Q0=makeQuery(id+"F2.opExtrude","CAP_FACE",FACE,{"disambiguationData":[OSD([sQuery(id+"F0.wireOp",EDGE,"E0.bottom"),sQuery(id+"F0.wireOp",EDGE,"E0.top"),sQuery(id+"F0.wireOp",EDGE,"E0.left"),sQuery(id+"F0.wireOp",EDGE,"E0.right"),sQuery(id+"F0.wireOp",EDGE,"E44"),sQuery(id+"F0.wireOp",EDGE,"E45"),sQuery(id+"F0.wireOp",EDGE,"E46"),sQuery(id+"F0.wireOp",EDGE,"E47"),sQuery(id+"F0.wireOp",EDGE,"E48"),sQuery(id+"F0.wireOp",EDGE,"E49"),sQuery(id+"F0.wireOp",EDGE,"E50"),sQuery(id+"F0.wireOp",EDGE,"E67.sketch_text.stroke-0"),sQuery(id+"F0.wireOp",EDGE,"E67.sketch_text.stroke-1"),sQuery(id+"F0.wireOp",EDGE,"E67.sketch_text.stroke-2"),sQuery(id+"F0.wireOp",EDGE,"E67.sketch_text.stroke-3"),sQuery(id+"F0.wireOp",EDGE,"E67.sketch_text.stroke-4"),sQuery(id+"F0.wireOp",EDGE,"E67.sketch_text.stroke-5"),sQuery(id+"F0.wireOp",EDGE,"E67.sketch_text.stroke-14"),sQuery(id+"F0.wireOp",EDGE,"E67.sketch_text.stroke-15"),sQuery(id+"F0.wireOp",EDGE,"E67.sketch_text.stroke-16"),sQuery(id+"F0.wireOp",EDGE,"E67.sketch_text.stroke-17"),sQuery(id+"F0.wireOp",EDGE,"E67.sketch_text.stroke-18"),sQuery(id+"F0.wireOp",EDGE,"E67.sketch_text.stroke-19"),sQuery(id+"F0.wireOp",EDGE,"E67.sketch_text.stroke-20"),sQuery(id+"F0.wireOp",EDGE,"E67.sketch_text.stroke-21"),sQuery(id+"F0.wireOp",EDGE,"E67.sketch_text.stroke-22"),sQuery(id+"F0.wireOp",EDGE,"E67.sketch_text.stroke-23"),sQuery(id+"F0.wireOp",EDGE,"E67.sketch_text.stroke-32"),sQuery(id+"F0.wireOp",EDGE,"E67.sketch_text.stroke-33"),sQuery(id+"F0.wireOp",EDGE,"E67.sketch_text.stroke-34"),sQuery(id+"F0.wireOp",EDGE,"E67.sketch_text.stroke-35"),sQuery(id+"F0.wireOp",EDGE,"E67.sketch_text.stroke-36"),sQuery(id+"F0.wireOp",EDGE,"E67.sketch_text.stroke-37"),sQuery(id+"F0.wireOp",EDGE,"E67.sketch_text.stroke-38"),sQuery(id+"F0.wireOp",EDGE,"E67.sketch_text.stroke-39"),sQuery(id+"F0.wireOp",EDGE,"E67.sketch_text.stroke-40"),sQuery(id+"F0.wireOp",EDGE,"E67.sketch_text.stroke-41"),sQuery(id+"F0.wireOp",EDGE,"E67.sketch_text.stroke-42"),sQuery(id+"F0.wireOp",EDGE,"E67.sketch_text.stroke-43"),sQuery(id+"F0.wireOp",EDGE,"E67.sketch_text.stroke-44"),sQuery(id+"F0.wireOp",EDGE,"E67.sketch_text.stroke-45"),sQuery(id+"F0.wireOp",EDGE,"E67.sketch_text.stroke-46"),sQuery(id+"F0.wireOp",EDGE,"E67.sketch_text.stroke-47"),sQuery(id+"F0.wireOp",EDGE,"E67.sketch_text.stroke-48"),sQuery(id+"F0.wireOp",EDGE,"E67.sketch_text.stroke-49"),sQuery(id+"F0.wireOp",EDGE,"E67.sketch_text.stroke-50"),sQuery(id+"F0.wireOp",EDGE,"E67.sketch_text.stroke-51"),sQuery(id+"F0.wireOp",EDGE,"E67.sketch_text.stroke-52"),sQuery(id+"F0.wireOp",EDGE,"E67.sketch_text.stroke-53"),sQuery(id+"F0.wireOp",EDGE,"E67.sketch_text.stroke-54"),sQuery(id+"F0.wireOp",EDGE,"E67.sketch_text.stroke-55"),sQuery(id+"F0.wireOp",EDGE,"E67.sketch_text.stroke-56"),sQuery(id+"F0.wireOp",EDGE,"E67.sketch_text.stroke-65"),sQuery(id+"F0.wireOp",EDGE,"E67.sketch_text.stroke-66"),sQuery(id+"F0.wireOp",EDGE,"E67.sketch_text.stroke-67"),sQuery(id+"F0.wireOp",EDGE,"E67.sketch_text.stroke-68"),sQuery(id+"F0.wireOp",EDGE,"E67.sketch_text.stroke-69"),sQuery(id+"F0.wireOp",EDGE,"E67.sketch_text.stroke-70"),sQuery(id+"F0.wireOp",EDGE,"E67.sketch_text.stroke-71"),sQuery(id+"F0.wireOp",EDGE,"E67.sketch_text.stroke-72"),sQuery(id+"F0.wireOp",EDGE,"E67.sketch_text.stroke-73"),sQuery(id+"F0.wireOp",EDGE,"E67.sketch_text.stroke-74"),sQuery(id+"F0.wireOp",EDGE,"E67.sketch_text.stroke-75"),sQuery(id+"F0.wireOp",EDGE,"E67.sketch_text.stroke-76"),sQuery(id+"F0.wireOp",EDGE,"E67.sketch_text.stroke-77"),sQuery(id+"F0.wireOp",EDGE,"E67.sketch_text.stroke-78"),sQuery(id+"F0.wireOp",EDGE,"E67.sketch_text.stroke-79"),sQuery(id+"F0.wireOp",EDGE,"E67.sketch_text.stroke-80"),sQuery(id+"F0.wireOp",EDGE,"E67.sketch_text.stroke-81"),sQuery(id+"F0.wireOp",EDGE,"E67.sketch_text.stroke-82"),sQuery(id+"F0.wireOp",EDGE,"E67.sketch_text.stroke-83"),sQuery(id+"F0.wireOp",EDGE,"E67.sketch_text.stroke-84"),sQuery(id+"F0.wireOp",EDGE,"E67.sketch_text.stroke-85"),sQuery(id+"F0.wireOp",EDGE,"E67.sketch_text.stroke-86"),sQuery(id+"F0.wireOp",EDGE,"E67.sketch_text.stroke-87"),sQuery(id+"F0.wireOp",EDGE,"E67.sketch_text.stroke-88"),sQuery(id+"F0.wireOp",EDGE,"E67.sketch_text.stroke-89"),sQuery(id+"F0.wireOp",EDGE,"E67.sketch_text.stroke-90"),sQuery(id+"F0.wireOp",EDGE,"E67.sketch_text.stroke-91"),sQuery(id+"F0.wireOp",EDGE,"E67.sketch_text.stroke-92"),sQuery(id+"F0.wireOp",EDGE,"E67.sketch_text.stroke-97"),sQuery(id+"F0.wireOp",EDGE,"E67.sketch_text.stroke-98"),sQuery(id+"F0.wireOp",EDGE,"E67.sketch_text.stroke-99"),sQuery(id+"F0.wireOp",EDGE,"E67.sketch_text.stroke-100"),sQuery(id+"F0.wireOp",EDGE,"E67.sketch_text.stroke-101"),sQuery(id+"F0.wireOp",EDGE,"E67.sketch_text.stroke-102"),sQuery(id+"F0.wireOp",EDGE,"E67.sketch_text.stroke-103"),sQuery(id+"F0.wireOp",EDGE,"E67.sketch_text.stroke-104"),sQuery(id+"F0.wireOp",EDGE,"E67.sketch_text.stroke-105"),sQuery(id+"F0.wireOp",EDGE,"E67.sketch_text.stroke-106"),sQuery(id+"F0.wireOp",EDGE,"E70.sketch_text.stroke-0"),sQuery(id+"F0.wireOp",EDGE,"E70.sketch_text.stroke-1"),sQuery(id+"F0.wireOp",EDGE,"E70.sketch_text.stroke-2"),sQuery(id+"F0.wireOp",EDGE,"E70.sketch_text.stroke-3"),sQuery(id+"F0.wireOp",EDGE,"E70.sketch_text.stroke-4"),sQuery(id+"F0.wireOp",EDGE,"E70.sketch_text.stroke-5"),sQuery(id+"F0.wireOp",EDGE,"E70.sketch_text.stroke-14"),sQuery(id+"F0.wireOp",EDGE,"E70.sketch_text.stroke-15"),sQuery(id+"F0.wireOp",EDGE,"E70.sketch_text.stroke-16"),sQuery(id+"F0.wireOp",EDGE,"E70.sketch_text.stroke-17"),sQuery(id+"F0.wireOp",EDGE,"E70.sketch_text.stroke-18"),sQuery(id+"F0.wireOp",EDGE,"E70.sketch_text.stroke-19"),sQuery(id+"F0.wireOp",EDGE,"E70.sketch_text.stroke-20"),sQuery(id+"F0.wireOp",EDGE,"E70.sketch_text.stroke-21"),sQuery(id+"F0.wireOp",EDGE,"E70.sketch_text.stroke-22"),sQuery(id+"F0.wireOp",EDGE,"E70.sketch_text.stroke-23"),sQuery(id+"F0.wireOp",EDGE,"E70.sketch_text.stroke-32"),sQuery(id+"F0.wireOp",EDGE,"E70.sketch_text.stroke-33"),sQuery(id+"F0.wireOp",EDGE,"E70.sketch_text.stroke-34"),sQuery(id+"F0.wireOp",EDGE,"E70.sketch_text.stroke-35"),sQuery(id+"F0.wireOp",EDGE,"E70.sketch_text.stroke-36"),sQuery(id+"F0.wireOp",EDGE,"E70.sketch_text.stroke-37"),sQuery(id+"F0.wireOp",EDGE,"E70.sketch_text.stroke-38"),sQuery(id+"F0.wireOp",EDGE,"E70.sketch_text.stroke-39"),sQuery(id+"F0.wireOp",EDGE,"E70.sketch_text.stroke-40"),sQuery(id+"F0.wireOp",EDGE,"E70.sketch_text.stroke-41"),sQuery(id+"F0.wireOp",EDGE,"E70.sketch_text.stroke-42"),sQuery(id+"F0.wireOp",EDGE,"E70.sketch_text.stroke-43"),sQuery(id+"F0.wireOp",EDGE,"E70.sketch_text.stroke-44"),sQuery(id+"F0.wireOp",EDGE,"E70.sketch_text.stroke-45"),sQuery(id+"F0.wireOp",EDGE,"E70.sketch_text.stroke-46"),sQuery(id+"F0.wireOp",EDGE,"E70.sketch_text.stroke-47"),sQuery(id+"F0.wireOp",EDGE,"E70.sketch_text.stroke-48"),sQuery(id+"F0.wireOp",EDGE,"E70.sketch_text.stroke-49"),sQuery(id+"F0.wireOp",EDGE,"E70.sketch_text.stroke-50"),sQuery(id+"F0.wireOp",EDGE,"E70.sketch_text.stroke-51"),sQuery(id+"F0.wireOp",EDGE,"E70.sketch_text.stroke-52"),sQuery(id+"F0.wireOp",EDGE,"E70.sketch_text.stroke-53"),sQuery(id+"F0.wireOp",EDGE,"E70.sketch_text.stroke-54"),sQuery(id+"F0.wireOp",EDGE,"E70.sketch_text.stroke-55"),sQuery(id+"F0.wireOp",EDGE,"E70.sketch_text.stroke-56"),sQuery(id+"F0.wireOp",EDGE,"E70.sketch_text.stroke-65"),sQuery(id+"F0.wireOp",EDGE,"E70.sketch_text.stroke-66"),sQuery(id+"F0.wireOp",EDGE,"E70.sketch_text.stroke-67"),sQuery(id+"F0.wireOp",EDGE,"E70.sketch_text.stroke-68"),sQuery(id+"F0.wireOp",EDGE,"E70.sketch_text.stroke-69"),sQuery(id+"F0.wireOp",EDGE,"E70.sketch_text.stroke-70"),sQuery(id+"F0.wireOp",EDGE,"E70.sketch_text.stroke-71"),sQuery(id+"F0.wireOp",EDGE,"E70.sketch_text.stroke-72"),sQuery(id+"F0.wireOp",EDGE,"E70.sketch_text.stroke-73"),sQuery(id+"F0.wireOp",EDGE,"E70.sketch_text.stroke-74"),sQuery(id+"F0.wireOp",EDGE,"E70.sketch_text.stroke-75"),sQuery(id+"F0.wireOp",EDGE,"E70.sketch_text.stroke-76"),sQuery(id+"F0.wireOp",EDGE,"E70.sketch_text.stroke-77"),sQuery(id+"F0.wireOp",EDGE,"E70.sketch_text.stroke-78"),sQuery(id+"F0.wireOp",EDGE,"E70.sketch_text.stroke-79"),sQuery(id+"F0.wireOp",EDGE,"E70.sketch_text.stroke-80"),sQuery(id+"F0.wireOp",EDGE,"E70.sketch_text.stroke-81"),sQuery(id+"F0.wireOp",EDGE,"E70.sketch_text.stroke-82"),sQuery(id+"F0.wireOp",EDGE,"E70.sketch_text.stroke-83"),sQuery(id+"F0.wireOp",EDGE,"E70.sketch_text.stroke-84"),sQuery(id+"F0.wireOp",EDGE,"E70.sketch_text.stroke-85"),sQuery(id+"F0.wireOp",EDGE,"E70.sketch_text.stroke-86"),sQuery(id+"F0.wireOp",EDGE,"E70.sketch_text.stroke-87"),sQuery(id+"F0.wireOp",EDGE,"E70.sketch_text.stroke-88"),sQuery(id+"F0.wireOp",EDGE,"E70.sketch_text.stroke-89"),sQuery(id+"F0.wireOp",EDGE,"E70.sketch_text.stroke-90"),sQuery(id+"F0.wireOp",EDGE,"E70.sketch_text.stroke-91"),sQuery(id+"F0.wireOp",EDGE,"E70.sketch_text.stroke-92"),sQuery(id+"F0.wireOp",EDGE,"E70.sketch_text.stroke-97"),sQuery(id+"F0.wireOp",EDGE,"E70.sketch_text.stroke-98"),sQuery(id+"F0.wireOp",EDGE,"E70.sketch_text.stroke-99"),sQuery(id+"F0.wireOp",EDGE,"E70.sketch_text.stroke-100"),sQuery(id+"F0.wireOp",EDGE,"E70.sketch_text.stroke-101"),sQuery(id+"F0.wireOp",EDGE,"E70.sketch_text.stroke-102"),sQuery(id+"F0.wireOp",EDGE,"E70.sketch_text.stroke-103"),sQuery(id+"F0.wireOp",EDGE,"E70.sketch_text.stroke-104"),sQuery(id+"F0.wireOp",EDGE,"E70.sketch_text.stroke-105"),sQuery(id+"F0.wireOp",EDGE,"E70.sketch_text.stroke-106"),sQuery(id+"F0.wireOp",EDGE,"E70.sketch_text.stroke-107"),sQuery(id+"F0.wireOp",EDGE,"E70.sketch_text.stroke-108"),sQuery(id+"F0.wireOp",EDGE,"E70.sketch_text.stroke-109"),sQuery(id+"F0.wireOp",EDGE,"E70.sketch_text.stroke-110"),sQuery(id+"F0.wireOp",EDGE,"E70.sketch_text.stroke-111"),sQuery(id+"F0.wireOp",EDGE,"E70.sketch_text.stroke-112"),sQuery(id+"F0.wireOp",EDGE,"E70.sketch_text.stroke-113"),sQuery(id+"F0.wireOp",EDGE,"E70.sketch_text.stroke-114"),sQuery(id+"F0.wireOp",EDGE,"E70.sketch_text.stroke-115"),sQuery(id+"F0.wireOp",EDGE,"E70.sketch_text.stroke-116"),sQuery(id+"F0.wireOp",EDGE,"E70.sketch_text.stroke-117"),sQuery(id+"F0.wireOp",EDGE,"E70.sketch_text.stroke-118"),sQuery(id+"F0.wireOp",EDGE,"E70.sketch_text.stroke-119"),sQuery(id+"F0.wireOp",EDGE,"E70.sketch_text.stroke-120"),sQuery(id+"F0.wireOp",EDGE,"E73.sketch_text.stroke-0"),sQuery(id+"F0.wireOp",EDGE,"E73.sketch_text.stroke-1"),sQuery(id+"F0.wireOp",EDGE,"E73.sketch_text.stroke-2"),sQuery(id+"F0.wireOp",EDGE,"E73.sketch_text.stroke-3"),sQuery(id+"F0.wireOp",EDGE,"E73.sketch_text.stroke-4"),sQuery(id+"F0.wireOp",EDGE,"E73.sketch_text.stroke-5"),sQuery(id+"F0.wireOp",EDGE,"E73.sketch_text.stroke-6"),sQuery(id+"F0.wireOp",EDGE,"E73.sketch_text.stroke-7"),sQuery(id+"F0.wireOp",EDGE,"E73.sketch_text.stroke-8"),sQuery(id+"F0.wireOp",EDGE,"E73.sketch_text.stroke-9"),sQuery(id+"F0.wireOp",EDGE,"E73.sketch_text.stroke-10"),sQuery(id+"F0.wireOp",EDGE,"E73.sketch_text.stroke-11"),sQuery(id+"F0.wireOp",EDGE,"E73.sketch_text.stroke-12"),sQuery(id+"F0.wireOp",EDGE,"E73.sketch_text.stroke-13"),sQuery(id+"F0.wireOp",EDGE,"E73.sketch_text.stroke-14"),sQuery(id+"F0.wireOp",EDGE,"E73.sketch_text.stroke-15"),sQuery(id+"F0.wireOp",EDGE,"E73.sketch_text.stroke-16"),sQuery(id+"F0.wireOp",EDGE,"E73.sketch_text.stroke-17"),sQuery(id+"F0.wireOp",EDGE,"E73.sketch_text.stroke-18"),sQuery(id+"F0.wireOp",EDGE,"E73.sketch_text.stroke-19"),sQuery(id+"F0.wireOp",EDGE,"E73.sketch_text.stroke-20"),sQuery(id+"F0.wireOp",EDGE,"E73.sketch_text.stroke-21"),sQuery(id+"F0.wireOp",EDGE,"E73.sketch_text.stroke-22"),sQuery(id+"F0.wireOp",EDGE,"E73.sketch_text.stroke-23"),sQuery(id+"F0.wireOp",EDGE,"E73.sketch_text.stroke-24"),sQuery(id+"F0.wireOp",EDGE,"E73.sketch_text.stroke-25"),sQuery(id+"F0.wireOp",EDGE,"E73.sketch_text.stroke-26"),sQuery(id+"F0.wireOp",EDGE,"E73.sketch_text.stroke-27"),sQuery(id+"F0.wireOp",EDGE,"E73.sketch_text.stroke-28"),sQuery(id+"F0.wireOp",EDGE,"E73.sketch_text.stroke-29"),sQuery(id+"F0.wireOp",EDGE,"E73.sketch_text.stroke-30"),sQuery(id+"F0.wireOp",EDGE,"E73.sketch_text.stroke-31"),sQuery(id+"F0.wireOp",EDGE,"E73.sketch_text.stroke-32"),sQuery(id+"F0.wireOp",EDGE,"E73.sketch_text.stroke-33"),sQuery(id+"F0.wireOp",EDGE,"E73.sketch_text.stroke-34"),sQuery(id+"F0.wireOp",EDGE,"E73.sketch_text.stroke-35"),sQuery(id+"F0.wireOp",EDGE,"E73.sketch_text.stroke-44"),sQuery(id+"F0.wireOp",EDGE,"E73.sketch_text.stroke-45"),sQuery(id+"F0.wireOp",EDGE,"E73.sketch_text.stroke-46"),sQuery(id+"F0.wireOp",EDGE,"E73.sketch_text.stroke-47"),sQuery(id+"F0.wireOp",EDGE,"E73.sketch_text.stroke-48"),sQuery(id+"F0.wireOp",EDGE,"E73.sketch_text.stroke-49"),sQuery(id+"F0.wireOp",EDGE,"E73.sketch_text.stroke-50"),sQuery(id+"F0.wireOp",EDGE,"E73.sketch_text.stroke-51"),sQuery(id+"F0.wireOp",EDGE,"E73.sketch_text.stroke-52"),sQuery(id+"F0.wireOp",EDGE,"E73.sketch_text.stroke-53"),sQuery(id+"F0.wireOp",EDGE,"E73.sketch_text.stroke-54"),sQuery(id+"F0.wireOp",EDGE,"E73.sketch_text.stroke-55"),sQuery(id+"F0.wireOp",EDGE,"E73.sketch_text.stroke-56"),sQuery(id+"F0.wireOp",EDGE,"E73.sketch_text.stroke-57"),sQuery(id+"F0.wireOp",EDGE,"E73.sketch_text.stroke-58"),sQuery(id+"F0.wireOp",EDGE,"E73.sketch_text.stroke-59"),sQuery(id+"F0.wireOp",EDGE,"E73.sketch_text.stroke-60"),sQuery(id+"F0.wireOp",EDGE,"E73.sketch_text.stroke-61"),sQuery(id+"F0.wireOp",EDGE,"E73.sketch_text.stroke-62"),sQuery(id+"F0.wireOp",EDGE,"E73.sketch_text.stroke-63"),sQuery(id+"F0.wireOp",EDGE,"E73.sketch_text.stroke-64"),sQuery(id+"F0.wireOp",EDGE,"E73.sketch_text.stroke-65"),sQuery(id+"F0.wireOp",EDGE,"E73.sketch_text.stroke-66"),sQuery(id+"F0.wireOp",EDGE,"E73.sketch_text.stroke-67"),sQuery(id+"F0.wireOp",EDGE,"E73.sketch_text.stroke-68"),sQuery(id+"F0.wireOp",EDGE,"E73.sketch_text.stroke-69"),sQuery(id+"F0.wireOp",EDGE,"E73.sketch_text.stroke-70"),sQuery(id+"F0.wireOp",EDGE,"E73.sketch_text.stroke-71"),sQuery(id+"F0.wireOp",EDGE,"E73.sketch_text.stroke-72"),sQuery(id+"F0.wireOp",EDGE,"E73.sketch_text.stroke-73"),sQuery(id+"F0.wireOp",EDGE,"E73.sketch_text.stroke-74"),sQuery(id+"F0.wireOp",EDGE,"E73.sketch_text.stroke-75"),sQuery(id+"F0.wireOp",EDGE,"E73.sketch_text.stroke-76"),sQuery(id+"F0.wireOp",EDGE,"E73.sketch_text.stroke-77"),sQuery(id+"F0.wireOp",EDGE,"E73.sketch_text.stroke-78"),sQuery(id+"F0.wireOp",EDGE,"E76.sketch_text.stroke-0"),sQuery(id+"F0.wireOp",EDGE,"E76.sketch_text.stroke-1"),sQuery(id+"F0.wireOp",EDGE,"E76.sketch_text.stroke-2"),sQuery(id+"F0.wireOp",EDGE,"E76.sketch_text.stroke-3"),sQuery(id+"F0.wireOp",EDGE,"E76.sketch_text.stroke-4"),sQuery(id+"F0.wireOp",EDGE,"E76.sketch_text.stroke-5"),sQuery(id+"F0.wireOp",EDGE,"E76.sketch_text.stroke-6"),sQuery(id+"F0.wireOp",EDGE,"E76.sketch_text.stroke-7"),sQuery(id+"F0.wireOp",EDGE,"E76.sketch_text.stroke-8"),sQuery(id+"F0.wireOp",EDGE,"E76.sketch_text.stroke-9"),sQuery(id+"F0.wireOp",EDGE,"E76.sketch_text.stroke-10"),sQuery(id+"F0.wireOp",EDGE,"E76.sketch_text.stroke-11"),sQuery(id+"F0.wireOp",EDGE,"E76.sketch_text.stroke-12"),sQuery(id+"F0.wireOp",EDGE,"E76.sketch_text.stroke-13"),sQuery(id+"F0.wireOp",EDGE,"E76.sketch_text.stroke-14"),sQuery(id+"F0.wireOp",EDGE,"E76.sketch_text.stroke-23"),sQuery(id+"F0.wireOp",EDGE,"E76.sketch_text.stroke-24"),sQuery(id+"F0.wireOp",EDGE,"E76.sketch_text.stroke-25"),sQuery(id+"F0.wireOp",EDGE,"E76.sketch_text.stroke-26"),sQuery(id+"F0.wireOp",EDGE,"E76.sketch_text.stroke-27"),sQuery(id+"F0.wireOp",EDGE,"E76.sketch_text.stroke-28"),sQuery(id+"F0.wireOp",EDGE,"E76.sketch_text.stroke-29"),sQuery(id+"F0.wireOp",EDGE,"E76.sketch_text.stroke-30"),sQuery(id+"F0.wireOp",EDGE,"E76.sketch_text.stroke-31"),sQuery(id+"F0.wireOp",EDGE,"E76.sketch_text.stroke-32"),sQuery(id+"F0.wireOp",EDGE,"E76.sketch_text.stroke-33"),sQuery(id+"F0.wireOp",EDGE,"E76.sketch_text.stroke-34"),sQuery(id+"F0.wireOp",EDGE,"E76.sketch_text.stroke-35"),sQuery(id+"F0.wireOp",EDGE,"E76.sketch_text.stroke-36"),sQuery(id+"F0.wireOp",EDGE,"E76.sketch_text.stroke-37"),sQuery(id+"F0.wireOp",EDGE,"E76.sketch_text.stroke-38"),sQuery(id+"F0.wireOp",EDGE,"E76.sketch_text.stroke-39"),sQuery(id+"F0.wireOp",EDGE,"E76.sketch_text.stroke-40"),sQuery(id+"F0.wireOp",EDGE,"E76.sketch_text.stroke-41"),sQuery(id+"F0.wireOp",EDGE,"E76.sketch_text.stroke-42"),sQuery(id+"F0.wireOp",EDGE,"E76.sketch_text.stroke-43"),sQuery(id+"F0.wireOp",EDGE,"E76.sketch_text.stroke-44"),sQuery(id+"F0.wireOp",EDGE,"E76.sketch_text.stroke-45"),sQuery(id+"F0.wireOp",EDGE,"E76.sketch_text.stroke-46"),sQuery(id+"F0.wireOp",EDGE,"E76.sketch_text.stroke-47"),sQuery(id+"F0.wireOp",EDGE,"E76.sketch_text.stroke-48"),sQuery(id+"F0.wireOp",EDGE,"E76.sketch_text.stroke-49"),sQuery(id+"F0.wireOp",EDGE,"E76.sketch_text.stroke-50"),sQuery(id+"F0.wireOp",EDGE,"E76.sketch_text.stroke-51"),sQuery(id+"F0.wireOp",EDGE,"E76.sketch_text.stroke-52"),sQuery(id+"F0.wireOp",EDGE,"E76.sketch_text.stroke-53"),sQuery(id+"F0.wireOp",EDGE,"E76.sketch_text.stroke-54"),sQuery(id+"F0.wireOp",EDGE,"E76.sketch_text.stroke-55"),sQuery(id+"F0.wireOp",EDGE,"E76.sketch_text.stroke-56"),sQuery(id+"F0.wireOp",EDGE,"E76.sketch_text.stroke-57"),sQuery(id+"F0.wireOp",EDGE,"E76.sketch_text.stroke-58"),sQuery(id+"F0.wireOp",EDGE,"E76.sketch_text.stroke-59"),sQuery(id+"F0.wireOp",EDGE,"E76.sketch_text.stroke-60"),sQuery(id+"F0.wireOp",EDGE,"E76.sketch_text.stroke-61"),sQuery(id+"F0.wireOp",EDGE,"E76.sketch_text.stroke-62"),sQuery(id+"F0.wireOp",EDGE,"E76.sketch_text.stroke-63"),sQuery(id+"F0.wireOp",EDGE,"E76.sketch_text.stroke-64"),sQuery(id+"F0.wireOp",EDGE,"E76.sketch_text.stroke-65"),sQuery(id+"F0.wireOp",EDGE,"E76.sketch_text.stroke-66"),sQuery(id+"F0.wireOp",EDGE,"E76.sketch_text.stroke-67"),sQuery(id+"F0.wireOp",EDGE,"E76.sketch_text.stroke-68"),sQuery(id+"F0.wireOp",EDGE,"E76.sketch_text.stroke-69"),sQuery(id+"F0.wireOp",EDGE,"E76.sketch_text.stroke-70"),sQuery(id+"F0.wireOp",EDGE,"E76.sketch_text.stroke-71"),sQuery(id+"F0.wireOp",EDGE,"E76.sketch_text.stroke-72"),sQuery(id+"F0.wireOp",EDGE,"E76.sketch_text.stroke-73"),sQuery(id+"F0.wireOp",EDGE,"E76.sketch_text.stroke-74"),sQuery(id+"F0.wireOp",EDGE,"E76.sketch_text.stroke-84"),sQuery(id+"F0.wireOp",EDGE,"E76.sketch_text.stroke-85"),sQuery(id+"F0.wireOp",EDGE,"E76.sketch_text.stroke-86"),sQuery(id+"F0.wireOp",EDGE,"E76.sketch_text.stroke-87"),sQuery(id+"F0.wireOp",EDGE,"E76.sketch_text.stroke-88"),sQuery(id+"F0.wireOp",EDGE,"E76.sketch_text.stroke-89"),sQuery(id+"F0.wireOp",EDGE,"E76.sketch_text.stroke-90"),sQuery(id+"F0.wireOp",EDGE,"E76.sketch_text.stroke-91"),sQuery(id+"F0.wireOp",EDGE,"E76.sketch_text.stroke-92"),sQuery(id+"F0.wireOp",EDGE,"E76.sketch_text.stroke-93"),sQuery(id+"F0.wireOp",EDGE,"E76.sketch_text.stroke-94"),sQuery(id+"F0.wireOp",EDGE,"E76.sketch_text.stroke-95"),sQuery(id+"F0.wireOp",EDGE,"E76.sketch_text.stroke-96"),sQuery(id+"F0.wireOp",EDGE,"E76.sketch_text.stroke-97"),sQuery(id+"F0.wireOp",EDGE,"E76.sketch_text.stroke-98"),sQuery(id+"F0.wireOp",EDGE,"E76.sketch_text.stroke-99"),sQuery(id+"F0.wireOp",EDGE,"E76.sketch_text.stroke-100"),sQuery(id+"F0.wireOp",EDGE,"E76.sketch_text.stroke-101"),sQuery(id+"F0.wireOp",EDGE,"E76.sketch_text.stroke-102"),sQuery(id+"F0.wireOp",EDGE,"E76.sketch_text.stroke-103"),sQuery(id+"F0.wireOp",EDGE,"E76.sketch_text.stroke-104"),sQuery(id+"F0.wireOp",EDGE,"E76.sketch_text.stroke-105"),sQuery(id+"F0.wireOp",EDGE,"E76.sketch_text.stroke-106"),sQuery(id+"F0.wireOp",EDGE,"E76.sketch_text.stroke-107"),sQuery(id+"F0.wireOp",EDGE,"E76.sketch_text.stroke-108"),sQuery(id+"F0.wireOp",EDGE,"E76.sketch_text.stroke-109"),sQuery(id+"F0.wireOp",EDGE,"E76.sketch_text.stroke-115"),sQuery(id+"F0.wireOp",EDGE,"E76.sketch_text.stroke-116"),sQuery(id+"F0.wireOp",EDGE,"E76.sketch_text.stroke-117"),sQuery(id+"F0.wireOp",EDGE,"E76.sketch_text.stroke-118"),sQuery(id+"F0.wireOp",EDGE,"E76.sketch_text.stroke-119"),sQuery(id+"F0.wireOp",EDGE,"E76.sketch_text.stroke-120"),sQuery(id+"F0.wireOp",EDGE,"E76.sketch_text.stroke-121"),sQuery(id+"F0.wireOp",EDGE,"E76.sketch_text.stroke-122"),sQuery(id+"F0.wireOp",EDGE,"E76.sketch_text.stroke-123"),sQuery(id+"F0.wireOp",EDGE,"E76.sketch_text.stroke-124"),sQuery(id+"F0.wireOp",EDGE,"E76.sketch_text.stroke-125"),sQuery(id+"F0.wireOp",EDGE,"E76.sketch_text.stroke-126"),sQuery(id+"F0.wireOp",EDGE,"E76.sketch_text.stroke-127"),sQuery(id+"F0.wireOp",EDGE,"E76.sketch_text.stroke-128"),sQuery(id+"F0.wireOp",EDGE,"E76.sketch_text.stroke-129"),sQuery(id+"F0.wireOp",EDGE,"E79.sketch_text.stroke-0"),sQuery(id+"F0.wireOp",EDGE,"E79.sketch_text.stroke-1"),sQuery(id+"F0.wireOp",EDGE,"E79.sketch_text.stroke-2"),sQuery(id+"F0.wireOp",EDGE,"E79.sketch_text.stroke-3"),sQuery(id+"F0.wireOp",EDGE,"E79.sketch_text.stroke-4"),sQuery(id+"F0.wireOp",EDGE,"E79.sketch_text.stroke-5"),sQuery(id+"F0.wireOp",EDGE,"E79.sketch_text.stroke-6"),sQuery(id+"F0.wireOp",EDGE,"E79.sketch_text.stroke-7"),sQuery(id+"F0.wireOp",EDGE,"E79.sketch_text.stroke-8"),sQuery(id+"F0.wireOp",EDGE,"E79.sketch_text.stroke-9"),sQuery(id+"F0.wireOp",EDGE,"E79.sketch_text.stroke-10"),sQuery(id+"F0.wireOp",EDGE,"E79.sketch_text.stroke-11"),sQuery(id+"F0.wireOp",EDGE,"E79.sketch_text.stroke-12"),sQuery(id+"F0.wireOp",EDGE,"E79.sketch_text.stroke-13"),sQuery(id+"F0.wireOp",EDGE,"E79.sketch_text.stroke-14"),sQuery(id+"F0.wireOp",EDGE,"E79.sketch_text.stroke-15"),sQuery(id+"F0.wireOp",EDGE,"E79.sketch_text.stroke-16"),sQuery(id+"F0.wireOp",EDGE,"E79.sketch_text.stroke-17"),sQuery(id+"F0.wireOp",EDGE,"E79.sketch_text.stroke-18"),sQuery(id+"F0.wireOp",EDGE,"E79.sketch_text.stroke-19"),sQuery(id+"F0.wireOp",EDGE,"E79.sketch_text.stroke-20"),sQuery(id+"F0.wireOp",EDGE,"E79.sketch_text.stroke-21"),sQuery(id+"F0.wireOp",EDGE,"E79.sketch_text.stroke-22"),sQuery(id+"F0.wireOp",EDGE,"E79.sketch_text.stroke-23"),sQuery(id+"F0.wireOp",EDGE,"E79.sketch_text.stroke-24"),sQuery(id+"F0.wireOp",EDGE,"E79.sketch_text.stroke-25"),sQuery(id+"F0.wireOp",EDGE,"E79.sketch_text.stroke-26"),sQuery(id+"F0.wireOp",EDGE,"E79.sketch_text.stroke-27"),sQuery(id+"F0.wireOp",EDGE,"E79.sketch_text.stroke-28"),sQuery(id+"F0.wireOp",EDGE,"E79.sketch_text.stroke-29"),sQuery(id+"F0.wireOp",EDGE,"E79.sketch_text.stroke-30"),sQuery(id+"F0.wireOp",EDGE,"E79.sketch_text.stroke-31"),sQuery(id+"F0.wireOp",EDGE,"E79.sketch_text.stroke-32"),sQuery(id+"F0.wireOp",EDGE,"E79.sketch_text.stroke-33"),sQuery(id+"F0.wireOp",EDGE,"E79.sketch_text.stroke-34"),sQuery(id+"F0.wireOp",EDGE,"E79.sketch_text.stroke-35"),sQuery(id+"F0.wireOp",EDGE,"E79.sketch_text.stroke-44"),sQuery(id+"F0.wireOp",EDGE,"E79.sketch_text.stroke-45"),sQuery(id+"F0.wireOp",EDGE,"E79.sketch_text.stroke-46"),sQuery(id+"F0.wireOp",EDGE,"E79.sketch_text.stroke-47"),sQuery(id+"F0.wireOp",EDGE,"E79.sketch_text.stroke-48"),sQuery(id+"F0.wireOp",EDGE,"E79.sketch_text.stroke-49"),sQuery(id+"F0.wireOp",EDGE,"E79.sketch_text.stroke-50"),sQuery(id+"F0.wireOp",EDGE,"E79.sketch_text.stroke-51"),sQuery(id+"F0.wireOp",EDGE,"E79.sketch_text.stroke-52"),sQuery(id+"F0.wireOp",EDGE,"E79.sketch_text.stroke-53"),sQuery(id+"F0.wireOp",EDGE,"E79.sketch_text.stroke-54"),sQuery(id+"F0.wireOp",EDGE,"E79.sketch_text.stroke-55"),sQuery(id+"F0.wireOp",EDGE,"E79.sketch_text.stroke-56"),sQuery(id+"F0.wireOp",EDGE,"E79.sketch_text.stroke-57"),sQuery(id+"F0.wireOp",EDGE,"E79.sketch_text.stroke-58"),sQuery(id+"F0.wireOp",EDGE,"E79.sketch_text.stroke-59"),sQuery(id+"F0.wireOp",EDGE,"E79.sketch_text.stroke-60"),sQuery(id+"F0.wireOp",EDGE,"E79.sketch_text.stroke-61"),sQuery(id+"F0.wireOp",EDGE,"E79.sketch_text.stroke-62"),sQuery(id+"F0.wireOp",EDGE,"E79.sketch_text.stroke-63"),sQuery(id+"F0.wireOp",EDGE,"E79.sketch_text.stroke-64"),sQuery(id+"F0.wireOp",EDGE,"E79.sketch_text.stroke-65"),sQuery(id+"F0.wireOp",EDGE,"E79.sketch_text.stroke-66"),sQuery(id+"F0.wireOp",EDGE,"E79.sketch_text.stroke-67"),sQuery(id+"F0.wireOp",EDGE,"E79.sketch_text.stroke-68"),sQuery(id+"F0.wireOp",EDGE,"E79.sketch_text.stroke-69"),sQuery(id+"F0.wireOp",EDGE,"E79.sketch_text.stroke-70"),sQuery(id+"F0.wireOp",EDGE,"E79.sketch_text.stroke-71"),sQuery(id+"F0.wireOp",EDGE,"E79.sketch_text.stroke-72"),sQuery(id+"F0.wireOp",EDGE,"E79.sketch_text.stroke-73"),sQuery(id+"F0.wireOp",EDGE,"E79.sketch_text.stroke-74"),sQuery(id+"F0.wireOp",EDGE,"E79.sketch_text.stroke-75"),sQuery(id+"F0.wireOp",EDGE,"E79.sketch_text.stroke-76"),sQuery(id+"F0.wireOp",EDGE,"E79.sketch_text.stroke-77"),sQuery(id+"F0.wireOp",EDGE,"E79.sketch_text.stroke-78"),sQuery(id+"F0.wireOp",EDGE,"E83"),sQuery(id+"F0.wireOp",EDGE,"E84"),sQuery(id+"F0.wireOp",EDGE,"E87"),sQuery(id+"F0.wireOp",EDGE,"E88"),sQuery(id+"F0.wireOp",EDGE,"E89"),sQuery(id+"F0.wireOp",EDGE,"E91"),sQuery(id+"F0.wireOp",EDGE,"E92"),sQuery(id+"F0.wireOp",EDGE,"ed6ad51a-24f1-4634-a6e9-502759cafa60.sketch_text.stroke-7"),sQuery(id+"F0.wireOp",EDGE,"ed6ad51a-24f1-4634-a6e9-502759cafa60.sketch_text.stroke-8"),sQuery(id+"F0.wireOp",EDGE,"ed6ad51a-24f1-4634-a6e9-502759cafa60.sketch_text.stroke-9"),sQuery(id+"F0.wireOp",EDGE,"ed6ad51a-24f1-4634-a6e9-502759cafa60.sketch_text.stroke-10"),sQuery(id+"F0.wireOp",EDGE,"ed6ad51a-24f1-4634-a6e9-502759cafa60.sketch_text.stroke-11"),sQuery(id+"F0.wireOp",EDGE,"ed6ad51a-24f1-4634-a6e9-502759cafa60.sketch_text.stroke-12"),sQuery(id+"F0.wireOp",EDGE,"ed6ad51a-24f1-4634-a6e9-502759cafa60.sketch_text.stroke-13"),sQuery(id+"F0.wireOp",EDGE,"ed6ad51a-24f1-4634-a6e9-502759cafa60.sketch_text.stroke-14"),sQuery(id+"F0.wireOp",EDGE,"ed6ad51a-24f1-4634-a6e9-502759cafa60.sketch_text.stroke-15"),sQuery(id+"F0.wireOp",EDGE,"ed6ad51a-24f1-4634-a6e9-502759cafa60.sketch_text.stroke-24"),sQuery(id+"F0.wireOp",EDGE,"ed6ad51a-24f1-4634-a6e9-502759cafa60.sketch_text.stroke-25"),sQuery(id+"F0.wireOp",EDGE,"ed6ad51a-24f1-4634-a6e9-502759cafa60.sketch_text.stroke-26"),sQuery(id+"F0.wireOp",EDGE,"ed6ad51a-24f1-4634-a6e9-502759cafa60.sketch_text.stroke-27"),sQuery(id+"F0.wireOp",EDGE,"ed6ad51a-24f1-4634-a6e9-502759cafa60.sketch_text.stroke-28"),sQuery(id+"F0.wireOp",EDGE,"ed6ad51a-24f1-4634-a6e9-502759cafa60.sketch_text.stroke-29"),sQuery(id+"F0.wireOp",EDGE,"ed6ad51a-24f1-4634-a6e9-502759cafa60.sketch_text.stroke-30"),sQuery(id+"F0.wireOp",EDGE,"ed6ad51a-24f1-4634-a6e9-502759cafa60.sketch_text.stroke-31"),sQuery(id+"F0.wireOp",EDGE,"ed6ad51a-24f1-4634-a6e9-502759cafa60.sketch_text.stroke-32"),sQuery(id+"F0.wireOp",EDGE,"ed6ad51a-24f1-4634-a6e9-502759cafa60.sketch_text.stroke-33"),sQuery(id+"F0.wireOp",EDGE,"ed6ad51a-24f1-4634-a6e9-502759cafa60.sketch_text.stroke-34"),sQuery(id+"F0.wireOp",EDGE,"ed6ad51a-24f1-4634-a6e9-502759cafa60.sketch_text.stroke-35"),sQuery(id+"F0.wireOp",EDGE,"ed6ad51a-24f1-4634-a6e9-502759cafa60.sketch_text.stroke-36"),sQuery(id+"F0.wireOp",EDGE,"ed6ad51a-24f1-4634-a6e9-502759cafa60.sketch_text.stroke-37"),sQuery(id+"F0.wireOp",EDGE,"ed6ad51a-24f1-4634-a6e9-502759cafa60.sketch_text.stroke-38"),sQuery(id+"F0.wireOp",EDGE,"ed6ad51a-24f1-4634-a6e9-502759cafa60.sketch_text.stroke-39"),sQuery(id+"F0.wireOp",EDGE,"ed6ad51a-24f1-4634-a6e9-502759cafa60.sketch_text.stroke-40"),sQuery(id+"F0.wireOp",EDGE,"ed6ad51a-24f1-4634-a6e9-502759cafa60.sketch_text.stroke-41"),sQuery(id+"F0.wireOp",EDGE,"ed6ad51a-24f1-4634-a6e9-502759cafa60.sketch_text.stroke-42"),sQuery(id+"F0.wireOp",EDGE,"ed6ad51a-24f1-4634-a6e9-502759cafa60.sketch_text.stroke-43"),sQuery(id+"F0.wireOp",EDGE,"ed6ad51a-24f1-4634-a6e9-502759cafa60.sketch_text.stroke-44"),sQuery(id+"F0.wireOp",EDGE,"ed6ad51a-24f1-4634-a6e9-502759cafa60.sketch_text.stroke-45"),sQuery(id+"F0.wireOp",EDGE,"ed6ad51a-24f1-4634-a6e9-502759cafa60.sketch_text.stroke-46"),sQuery(id+"F0.wireOp",EDGE,"ed6ad51a-24f1-4634-a6e9-502759cafa60.sketch_text.stroke-47"),sQuery(id+"F0.wireOp",EDGE,"ed6ad51a-24f1-4634-a6e9-502759cafa60.sketch_text.stroke-48"),sQuery(id+"F0.wireOp",EDGE,"ed6ad51a-24f1-4634-a6e9-502759cafa60.sketch_text.stroke-49"),sQuery(id+"F0.wireOp",EDGE,"ed6ad51a-24f1-4634-a6e9-502759cafa60.sketch_text.stroke-50"),sQuery(id+"F0.wireOp",EDGE,"ed6ad51a-24f1-4634-a6e9-502759cafa60.sketch_text.stroke-51"),sQuery(id+"F0.wireOp",EDGE,"ed6ad51a-24f1-4634-a6e9-502759cafa60.sketch_text.stroke-52"),sQuery(id+"F0.wireOp",EDGE,"ed6ad51a-24f1-4634-a6e9-502759cafa60.sketch_text.stroke-53"),sQuery(id+"F0.wireOp",EDGE,"ed6ad51a-24f1-4634-a6e9-502759cafa60.sketch_text.stroke-54"),sQuery(id+"F0.wireOp",EDGE,"ed6ad51a-24f1-4634-a6e9-502759cafa60.sketch_text.stroke-55"),sQuery(id+"F0.wireOp",EDGE,"ed6ad51a-24f1-4634-a6e9-502759cafa60.sketch_text.stroke-56"),sQuery(id+"F0.wireOp",EDGE,"ed6ad51a-24f1-4634-a6e9-502759cafa60.sketch_text.stroke-57"),sQuery(id+"F0.wireOp",EDGE,"ed6ad51a-24f1-4634-a6e9-502759cafa60.sketch_text.stroke-58"),sQuery(id+"F0.wireOp",EDGE,"ed6ad51a-24f1-4634-a6e9-502759cafa60.sketch_text.stroke-59"),sQuery(id+"F0.wireOp",EDGE,"ed6ad51a-24f1-4634-a6e9-502759cafa60.sketch_text.stroke-65"),sQuery(id+"F0.wireOp",EDGE,"ed6ad51a-24f1-4634-a6e9-502759cafa60.sketch_text.stroke-66"),sQuery(id+"F0.wireOp",EDGE,"ed6ad51a-24f1-4634-a6e9-502759cafa60.sketch_text.stroke-67"),sQuery(id+"F0.wireOp",EDGE,"ed6ad51a-24f1-4634-a6e9-502759cafa60.sketch_text.stroke-68"),sQuery(id+"F0.wireOp",EDGE,"ed6ad51a-24f1-4634-a6e9-502759cafa60.sketch_text.stroke-69"),sQuery(id+"F0.wireOp",EDGE,"ed6ad51a-24f1-4634-a6e9-502759cafa60.sketch_text.stroke-70"),sQuery(id+"F0.wireOp",EDGE,"ed6ad51a-24f1-4634-a6e9-502759cafa60.sketch_text.stroke-71"),sQuery(id+"F0.wireOp",EDGE,"ed6ad51a-24f1-4634-a6e9-502759cafa60.sketch_text.stroke-72"),sQuery(id+"F0.wireOp",EDGE,"ed6ad51a-24f1-4634-a6e9-502759cafa60.sketch_text.stroke-73"),sQuery(id+"F0.wireOp",EDGE,"ed6ad51a-24f1-4634-a6e9-502759cafa60.sketch_text.stroke-74"),sQuery(id+"F0.wireOp",EDGE,"ed6ad51a-24f1-4634-a6e9-502759cafa60.sketch_text.stroke-75"),sQuery(id+"F0.wireOp",EDGE,"ed6ad51a-24f1-4634-a6e9-502759cafa60.sketch_text.stroke-76"),sQuery(id+"F0.wireOp",EDGE,"ed6ad51a-24f1-4634-a6e9-502759cafa60.sketch_text.stroke-77"),sQuery(id+"F0.wireOp",EDGE,"ed6ad51a-24f1-4634-a6e9-502759cafa60.sketch_text.stroke-78"),sQuery(id+"F0.wireOp",EDGE,"ed6ad51a-24f1-4634-a6e9-502759cafa60.sketch_text.stroke-79"),sQuery(id+"F0.wireOp",EDGE,"ed6ad51a-24f1-4634-a6e9-502759cafa60.sketch_text.stroke-80"),sQuery(id+"F0.wireOp",EDGE,"ed6ad51a-24f1-4634-a6e9-502759cafa60.sketch_text.stroke-81"),sQuery(id+"F0.wireOp",EDGE,"ed6ad51a-24f1-4634-a6e9-502759cafa60.sketch_text.stroke-82"),sQuery(id+"F0.wireOp",EDGE,"ed6ad51a-24f1-4634-a6e9-502759cafa60.sketch_text.stroke-83"),sQuery(id+"F0.wireOp",EDGE,"ed6ad51a-24f1-4634-a6e9-502759cafa60.sketch_text.stroke-84"),sQuery(id+"F0.wireOp",EDGE,"ed6ad51a-24f1-4634-a6e9-502759cafa60.sketch_text.stroke-85"),sQuery(id+"F0.wireOp",EDGE,"ed6ad51a-24f1-4634-a6e9-502759cafa60.sketch_text.stroke-86"),sQuery(id+"F0.wireOp",EDGE,"ed6ad51a-24f1-4634-a6e9-502759cafa60.sketch_text.stroke-87"),sQuery(id+"F0.wireOp",EDGE,"ed6ad51a-24f1-4634-a6e9-502759cafa60.sketch_text.stroke-88"),sQuery(id+"F0.wireOp",EDGE,"ed6ad51a-24f1-4634-a6e9-502759cafa60.sketch_text.stroke-89"),sQuery(id+"F0.wireOp",EDGE,"ed6ad51a-24f1-4634-a6e9-502759cafa60.sketch_text.stroke-90"),sQuery(id+"F0.wireOp",EDGE,"ed6ad51a-24f1-4634-a6e9-502759cafa60.sketch_text.stroke-91"),sQuery(id+"F0.wireOp",EDGE,"ed6ad51a-24f1-4634-a6e9-502759cafa60.sketch_text.stroke-92"),sQuery(id+"F0.wireOp",EDGE,"E97.sketch_text.stroke-0"),sQuery(id+"F0.wireOp",EDGE,"E97.sketch_text.stroke-1"),sQuery(id+"F0.wireOp",EDGE,"E97.sketch_text.stroke-2"),sQuery(id+"F0.wireOp",EDGE,"E97.sketch_text.stroke-3"),sQuery(id+"F0.wireOp",EDGE,"E97.sketch_text.stroke-4"),sQuery(id+"F0.wireOp",EDGE,"E97.sketch_text.stroke-5"),sQuery(id+"F0.wireOp",EDGE,"E97.sketch_text.stroke-6"),sQuery(id+"F0.wireOp",EDGE,"E97.sketch_text.stroke-7"),sQuery(id+"F0.wireOp",EDGE,"E97.sketch_text.stroke-14"),sQuery(id+"F0.wireOp",EDGE,"E97.sketch_text.stroke-15"),sQuery(id+"F0.wireOp",EDGE,"E97.sketch_text.stroke-16"),sQuery(id+"F0.wireOp",EDGE,"E97.sketch_text.stroke-17"),sQuery(id+"F0.wireOp",EDGE,"E97.sketch_text.stroke-18"),sQuery(id+"F0.wireOp",EDGE,"E97.sketch_text.stroke-19"),sQuery(id+"F0.wireOp",EDGE,"E97.sketch_text.stroke-20"),sQuery(id+"F0.wireOp",EDGE,"E97.sketch_text.stroke-21"),sQuery(id+"F0.wireOp",EDGE,"E97.sketch_text.stroke-22"),sQuery(id+"F0.wireOp",EDGE,"E97.sketch_text.stroke-23"),sQuery(id+"F0.wireOp",EDGE,"E97.sketch_text.stroke-24"),sQuery(id+"F0.wireOp",EDGE,"E97.sketch_text.stroke-25"),sQuery(id+"F0.wireOp",EDGE,"E97.sketch_text.stroke-26"),sQuery(id+"F0.wireOp",EDGE,"E97.sketch_text.stroke-27"),sQuery(id+"F0.wireOp",EDGE,"E97.sketch_text.stroke-28"),sQuery(id+"F0.wireOp",EDGE,"E97.sketch_text.stroke-29"),sQuery(id+"F0.wireOp",EDGE,"E97.sketch_text.stroke-30"),sQuery(id+"F0.wireOp",EDGE,"E97.sketch_text.stroke-31"),sQuery(id+"F0.wireOp",EDGE,"E97.sketch_text.stroke-32"),sQuery(id+"F0.wireOp",EDGE,"E97.sketch_text.stroke-33"),sQuery(id+"F0.wireOp",EDGE,"E97.sketch_text.stroke-34"),sQuery(id+"F0.wireOp",EDGE,"E97.sketch_text.stroke-35"),sQuery(id+"F0.wireOp",EDGE,"E97.sketch_text.stroke-36"),sQuery(id+"F0.wireOp",EDGE,"E97.sketch_text.stroke-37"),sQuery(id+"F0.wireOp",EDGE,"E97.sketch_text.stroke-38"),sQuery(id+"F0.wireOp",EDGE,"E97.sketch_text.stroke-39"),sQuery(id+"F0.wireOp",EDGE,"E97.sketch_text.stroke-40"),sQuery(id+"F0.wireOp",EDGE,"E97.sketch_text.stroke-41"),sQuery(id+"F0.wireOp",EDGE,"E97.sketch_text.stroke-42"),sQuery(id+"F0.wireOp",EDGE,"E97.sketch_text.stroke-43"),sQuery(id+"F0.wireOp",EDGE,"E97.sketch_text.stroke-44"),sQuery(id+"F0.wireOp",EDGE,"E97.sketch_text.stroke-45"),sQuery(id+"F0.wireOp",EDGE,"E97.sketch_text.stroke-46"),sQuery(id+"F0.wireOp",EDGE,"E97.sketch_text.stroke-47"),sQuery(id+"F0.wireOp",EDGE,"E97.sketch_text.stroke-48"),sQuery(id+"F0.wireOp",EDGE,"E97.sketch_text.stroke-49"),sQuery(id+"F0.wireOp",EDGE,"E97.sketch_text.stroke-50"),sQuery(id+"F0.wireOp",EDGE,"E97.sketch_text.stroke-51"),sQuery(id+"F0.wireOp",EDGE,"E97.sketch_text.stroke-52"),sQuery(id+"F0.wireOp",EDGE,"E97.sketch_text.stroke-53"),sQuery(id+"F0.wireOp",EDGE,"E97.sketch_text.stroke-54"),sQuery(id+"F0.wireOp",EDGE,"E97.sketch_text.stroke-55"),sQuery(id+"F0.wireOp",EDGE,"E97.sketch_text.stroke-56"),sQuery(id+"F0.wireOp",EDGE,"E97.sketch_text.stroke-57"),sQuery(id+"F0.wireOp",EDGE,"E97.sketch_text.stroke-58"),sQuery(id+"F0.wireOp",EDGE,"E97.sketch_text.stroke-59"),sQuery(id+"F0.wireOp",EDGE,"E97.sketch_text.stroke-60"),sQuery(id+"F0.wireOp",EDGE,"E97.sketch_text.stroke-61"),sQuery(id+"F0.wireOp",EDGE,"E97.sketch_text.stroke-62"),sQuery(id+"F0.wireOp",EDGE,"E97.sketch_text.stroke-63"),sQuery(id+"F0.wireOp",EDGE,"E97.sketch_text.stroke-72"),sQuery(id+"F0.wireOp",EDGE,"E97.sketch_text.stroke-73"),sQuery(id+"F0.wireOp",EDGE,"E97.sketch_text.stroke-74"),sQuery(id+"F0.wireOp",EDGE,"E97.sketch_text.stroke-75"),sQuery(id+"F0.wireOp",EDGE,"E97.sketch_text.stroke-76"),sQuery(id+"F0.wireOp",EDGE,"E97.sketch_text.stroke-77"),sQuery(id+"F0.wireOp",EDGE,"E97.sketch_text.stroke-78"),sQuery(id+"F0.wireOp",EDGE,"E97.sketch_text.stroke-79"),sQuery(id+"F0.wireOp",EDGE,"E97.sketch_text.stroke-80"),sQuery(id+"F0.wireOp",EDGE,"E97.sketch_text.stroke-81"),sQuery(id+"F0.wireOp",EDGE,"E97.sketch_text.stroke-82"),sQuery(id+"F0.wireOp",EDGE,"E97.sketch_text.stroke-83"),sQuery(id+"F0.wireOp",EDGE,"E97.sketch_text.stroke-84"),sQuery(id+"F0.wireOp",EDGE,"E97.sketch_text.stroke-85"),sQuery(id+"F0.wireOp",EDGE,"E97.sketch_text.stroke-86"),sQuery(id+"F0.wireOp",EDGE,"E97.sketch_text.stroke-87"),sQuery(id+"F0.wireOp",EDGE,"E97.sketch_text.stroke-88"),sQuery(id+"F0.wireOp",EDGE,"E97.sketch_text.stroke-89"),sQuery(id+"F0.wireOp",EDGE,"E97.sketch_text.stroke-90"),sQuery(id+"F0.wireOp",EDGE,"E97.sketch_text.stroke-91"),sQuery(id+"F0.wireOp",EDGE,"E97.sketch_text.stroke-92"),sQuery(id+"F0.wireOp",EDGE,"E97.sketch_text.stroke-93"),sQuery(id+"F0.wireOp",EDGE,"E97.sketch_text.stroke-94"),sQuery(id+"F0.wireOp",EDGE,"E97.sketch_text.stroke-95"),sQuery(id+"F0.wireOp",EDGE,"E97.sketch_text.stroke-96"),sQuery(id+"F0.wireOp",EDGE,"E97.sketch_text.stroke-97"),sQuery(id+"F0.wireOp",EDGE,"E97.sketch_text.stroke-98"),sQuery(id+"F0.wireOp",EDGE,"E97.sketch_text.stroke-99"),sQuery(id+"F0.wireOp",EDGE,"E97.sketch_text.stroke-100"),sQuery(id+"F0.wireOp",EDGE,"E97.sketch_text.stroke-101"),sQuery(id+"F0.wireOp",EDGE,"E97.sketch_text.stroke-102"),sQuery(id+"F0.wireOp",EDGE,"E97.sketch_text.stroke-103"),sQuery(id+"F0.wireOp",EDGE,"E97.sketch_text.stroke-104"),sQuery(id+"F0.wireOp",EDGE,"E97.sketch_text.stroke-105"),sQuery(id+"F0.wireOp",EDGE,"E97.sketch_text.stroke-106"),sQuery(id+"F0.wireOp",EDGE,"E100.sketch_text.stroke-0"),sQuery(id+"F0.wireOp",EDGE,"E100.sketch_text.stroke-1"),sQuery(id+"F0.wireOp",EDGE,"E100.sketch_text.stroke-2"),sQuery(id+"F0.wireOp",EDGE,"E100.sketch_text.stroke-3"),sQuery(id+"F0.wireOp",EDGE,"E100.sketch_text.stroke-4"),sQuery(id+"F0.wireOp",EDGE,"E100.sketch_text.stroke-5"),sQuery(id+"F0.wireOp",EDGE,"E100.sketch_text.stroke-6"),sQuery(id+"F0.wireOp",EDGE,"E100.sketch_text.stroke-7"),sQuery(id+"F0.wireOp",EDGE,"E100.sketch_text.stroke-14"),sQuery(id+"F0.wireOp",EDGE,"E100.sketch_text.stroke-15"),sQuery(id+"F0.wireOp",EDGE,"E100.sketch_text.stroke-16"),sQuery(id+"F0.wireOp",EDGE,"E100.sketch_text.stroke-17"),sQuery(id+"F0.wireOp",EDGE,"E100.sketch_text.stroke-18"),sQuery(id+"F0.wireOp",EDGE,"E100.sketch_text.stroke-19"),sQuery(id+"F0.wireOp",EDGE,"E100.sketch_text.stroke-20"),sQuery(id+"F0.wireOp",EDGE,"E100.sketch_text.stroke-21"),sQuery(id+"F0.wireOp",EDGE,"E100.sketch_text.stroke-22"),sQuery(id+"F0.wireOp",EDGE,"E100.sketch_text.stroke-23"),sQuery(id+"F0.wireOp",EDGE,"E100.sketch_text.stroke-24"),sQuery(id+"F0.wireOp",EDGE,"E100.sketch_text.stroke-25"),sQuery(id+"F0.wireOp",EDGE,"E100.sketch_text.stroke-26"),sQuery(id+"F0.wireOp",EDGE,"E100.sketch_text.stroke-27"),sQuery(id+"F0.wireOp",EDGE,"E100.sketch_text.stroke-28"),sQuery(id+"F0.wireOp",EDGE,"E100.sketch_text.stroke-29"),sQuery(id+"F0.wireOp",EDGE,"E100.sketch_text.stroke-30"),sQuery(id+"F0.wireOp",EDGE,"E100.sketch_text.stroke-31"),sQuery(id+"F0.wireOp",EDGE,"E100.sketch_text.stroke-32"),sQuery(id+"F0.wireOp",EDGE,"E100.sketch_text.stroke-33"),sQuery(id+"F0.wireOp",EDGE,"E100.sketch_text.stroke-34"),sQuery(id+"F0.wireOp",EDGE,"E100.sketch_text.stroke-35"),sQuery(id+"F0.wireOp",EDGE,"E100.sketch_text.stroke-36"),sQuery(id+"F0.wireOp",EDGE,"E100.sketch_text.stroke-37"),sQuery(id+"F0.wireOp",EDGE,"E100.sketch_text.stroke-38"),sQuery(id+"F0.wireOp",EDGE,"E100.sketch_text.stroke-39"),sQuery(id+"F0.wireOp",EDGE,"E100.sketch_text.stroke-40"),sQuery(id+"F0.wireOp",EDGE,"E100.sketch_text.stroke-41"),sQuery(id+"F0.wireOp",EDGE,"E100.sketch_text.stroke-42"),sQuery(id+"F0.wireOp",EDGE,"E100.sketch_text.stroke-43"),sQuery(id+"F0.wireOp",EDGE,"E100.sketch_text.stroke-44"),sQuery(id+"F0.wireOp",EDGE,"E100.sketch_text.stroke-45"),sQuery(id+"F0.wireOp",EDGE,"E100.sketch_text.stroke-46"),sQuery(id+"F0.wireOp",EDGE,"E100.sketch_text.stroke-47"),sQuery(id+"F0.wireOp",EDGE,"E100.sketch_text.stroke-48"),sQuery(id+"F0.wireOp",EDGE,"E100.sketch_text.stroke-49"),sQuery(id+"F0.wireOp",EDGE,"E100.sketch_text.stroke-50"),sQuery(id+"F0.wireOp",EDGE,"E100.sketch_text.stroke-51"),sQuery(id+"F0.wireOp",EDGE,"E100.sketch_text.stroke-52"),sQuery(id+"F0.wireOp",EDGE,"E100.sketch_text.stroke-53"),sQuery(id+"F0.wireOp",EDGE,"E100.sketch_text.stroke-54"),sQuery(id+"F0.wireOp",EDGE,"E100.sketch_text.stroke-55"),sQuery(id+"F0.wireOp",EDGE,"E100.sketch_text.stroke-56"),sQuery(id+"F0.wireOp",EDGE,"E100.sketch_text.stroke-57"),sQuery(id+"F0.wireOp",EDGE,"E100.sketch_text.stroke-58"),sQuery(id+"F0.wireOp",EDGE,"E100.sketch_text.stroke-59"),sQuery(id+"F0.wireOp",EDGE,"E100.sketch_text.stroke-60"),sQuery(id+"F0.wireOp",EDGE,"E100.sketch_text.stroke-61"),sQuery(id+"F0.wireOp",EDGE,"E100.sketch_text.stroke-62"),sQuery(id+"F0.wireOp",EDGE,"E100.sketch_text.stroke-63"),sQuery(id+"F0.wireOp",EDGE,"E100.sketch_text.stroke-72"),sQuery(id+"F0.wireOp",EDGE,"E100.sketch_text.stroke-73"),sQuery(id+"F0.wireOp",EDGE,"E100.sketch_text.stroke-74"),sQuery(id+"F0.wireOp",EDGE,"E100.sketch_text.stroke-75"),sQuery(id+"F0.wireOp",EDGE,"E100.sketch_text.stroke-76"),sQuery(id+"F0.wireOp",EDGE,"E100.sketch_text.stroke-77"),sQuery(id+"F0.wireOp",EDGE,"E100.sketch_text.stroke-78"),sQuery(id+"F0.wireOp",EDGE,"E100.sketch_text.stroke-79"),sQuery(id+"F0.wireOp",EDGE,"E100.sketch_text.stroke-80"),sQuery(id+"F0.wireOp",EDGE,"E100.sketch_text.stroke-81"),sQuery(id+"F0.wireOp",EDGE,"E100.sketch_text.stroke-82"),sQuery(id+"F0.wireOp",EDGE,"E100.sketch_text.stroke-83"),sQuery(id+"F0.wireOp",EDGE,"E100.sketch_text.stroke-84"),sQuery(id+"F0.wireOp",EDGE,"E100.sketch_text.stroke-85"),sQuery(id+"F0.wireOp",EDGE,"E100.sketch_text.stroke-86"),sQuery(id+"F0.wireOp",EDGE,"E100.sketch_text.stroke-87"),sQuery(id+"F0.wireOp",EDGE,"E100.sketch_text.stroke-88"),sQuery(id+"F0.wireOp",EDGE,"E100.sketch_text.stroke-89"),sQuery(id+"F0.wireOp",EDGE,"E100.sketch_text.stroke-90"),sQuery(id+"F0.wireOp",EDGE,"E100.sketch_text.stroke-91"),sQuery(id+"F0.wireOp",EDGE,"E100.sketch_text.stroke-92"),sQuery(id+"F0.wireOp",EDGE,"E100.sketch_text.stroke-93"),sQuery(id+"F0.wireOp",EDGE,"E100.sketch_text.stroke-94"),sQuery(id+"F0.wireOp",EDGE,"E100.sketch_text.stroke-95"),sQuery(id+"F0.wireOp",EDGE,"E100.sketch_text.stroke-96"),sQuery(id+"F0.wireOp",EDGE,"E100.sketch_text.stroke-97"),sQuery(id+"F0.wireOp",EDGE,"E100.sketch_text.stroke-98"),sQuery(id+"F0.wireOp",EDGE,"E100.sketch_text.stroke-99"),sQuery(id+"F0.wireOp",EDGE,"E100.sketch_text.stroke-100"),sQuery(id+"F0.wireOp",EDGE,"E100.sketch_text.stroke-101"),sQuery(id+"F0.wireOp",EDGE,"E100.sketch_text.stroke-102"),sQuery(id+"F0.wireOp",EDGE,"E100.sketch_text.stroke-103"),sQuery(id+"F0.wireOp",EDGE,"E100.sketch_text.stroke-104"),sQuery(id+"F0.wireOp",EDGE,"E100.sketch_text.stroke-105"),sQuery(id+"F0.wireOp",EDGE,"E100.sketch_text.stroke-106"),sQuery(id+"F0.wireOp",EDGE,"E103.sketch_text.stroke-0"),sQuery(id+"F0.wireOp",EDGE,"E103.sketch_text.stroke-1"),sQuery(id+"F0.wireOp",EDGE,"E103.sketch_text.stroke-2"),sQuery(id+"F0.wireOp",EDGE,"E103.sketch_text.stroke-3"),sQuery(id+"F0.wireOp",EDGE,"E103.sketch_text.stroke-4"),sQuery(id+"F0.wireOp",EDGE,"E103.sketch_text.stroke-5"),sQuery(id+"F0.wireOp",EDGE,"E103.sketch_text.stroke-6"),sQuery(id+"F0.wireOp",EDGE,"E103.sketch_text.stroke-7"),sQuery(id+"F0.wireOp",EDGE,"E103.sketch_text.stroke-8"),sQuery(id+"F0.wireOp",EDGE,"E103.sketch_text.stroke-9"),sQuery(id+"F0.wireOp",EDGE,"E103.sketch_text.stroke-10"),sQuery(id+"F0.wireOp",EDGE,"E103.sketch_text.stroke-11"),sQuery(id+"F0.wireOp",EDGE,"E103.sketch_text.stroke-12"),sQuery(id+"F0.wireOp",EDGE,"E103.sketch_text.stroke-13"),sQuery(id+"F0.wireOp",EDGE,"E103.sketch_text.stroke-14"),sQuery(id+"F0.wireOp",EDGE,"E103.sketch_text.stroke-15"),sQuery(id+"F0.wireOp",EDGE,"E103.sketch_text.stroke-16"),sQuery(id+"F0.wireOp",EDGE,"E103.sketch_text.stroke-17"),sQuery(id+"F0.wireOp",EDGE,"E103.sketch_text.stroke-18"),sQuery(id+"F0.wireOp",EDGE,"E103.sketch_text.stroke-19"),sQuery(id+"F0.wireOp",EDGE,"E103.sketch_text.stroke-20"),sQuery(id+"F0.wireOp",EDGE,"E103.sketch_text.stroke-21"),sQuery(id+"F0.wireOp",EDGE,"E103.sketch_text.stroke-22"),sQuery(id+"F0.wireOp",EDGE,"E103.sketch_text.stroke-23"),sQuery(id+"F0.wireOp",EDGE,"E103.sketch_text.stroke-24"),sQuery(id+"F0.wireOp",EDGE,"E103.sketch_text.stroke-25"),sQuery(id+"F0.wireOp",EDGE,"E103.sketch_text.stroke-26"),sQuery(id+"F0.wireOp",EDGE,"E103.sketch_text.stroke-27"),sQuery(id+"F0.wireOp",EDGE,"E103.sketch_text.stroke-28"),sQuery(id+"F0.wireOp",EDGE,"E103.sketch_text.stroke-29"),sQuery(id+"F0.wireOp",EDGE,"E103.sketch_text.stroke-30"),sQuery(id+"F0.wireOp",EDGE,"E103.sketch_text.stroke-31"),sQuery(id+"F0.wireOp",EDGE,"E103.sketch_text.stroke-32"),sQuery(id+"F0.wireOp",EDGE,"E103.sketch_text.stroke-33"),sQuery(id+"F0.wireOp",EDGE,"E103.sketch_text.stroke-34"),sQuery(id+"F0.wireOp",EDGE,"E103.sketch_text.stroke-35"),sQuery(id+"F0.wireOp",EDGE,"E103.sketch_text.stroke-44"),sQuery(id+"F0.wireOp",EDGE,"E103.sketch_text.stroke-45"),sQuery(id+"F0.wireOp",EDGE,"E103.sketch_text.stroke-46"),sQuery(id+"F0.wireOp",EDGE,"E103.sketch_text.stroke-47"),sQuery(id+"F0.wireOp",EDGE,"E103.sketch_text.stroke-48"),sQuery(id+"F0.wireOp",EDGE,"E103.sketch_text.stroke-49"),sQuery(id+"F0.wireOp",EDGE,"E103.sketch_text.stroke-50"),sQuery(id+"F0.wireOp",EDGE,"E103.sketch_text.stroke-51"),sQuery(id+"F0.wireOp",EDGE,"E103.sketch_text.stroke-52"),sQuery(id+"F0.wireOp",EDGE,"E103.sketch_text.stroke-53"),sQuery(id+"F0.wireOp",EDGE,"E103.sketch_text.stroke-54"),sQuery(id+"F0.wireOp",EDGE,"E103.sketch_text.stroke-55"),sQuery(id+"F0.wireOp",EDGE,"E103.sketch_text.stroke-56"),sQuery(id+"F0.wireOp",EDGE,"E103.sketch_text.stroke-57"),sQuery(id+"F0.wireOp",EDGE,"E103.sketch_text.stroke-58"),sQuery(id+"F0.wireOp",EDGE,"E103.sketch_text.stroke-59"),sQuery(id+"F0.wireOp",EDGE,"E103.sketch_text.stroke-60"),sQuery(id+"F0.wireOp",EDGE,"E103.sketch_text.stroke-61"),sQuery(id+"F0.wireOp",EDGE,"E103.sketch_text.stroke-62"),sQuery(id+"F0.wireOp",EDGE,"E103.sketch_text.stroke-63"),sQuery(id+"F0.wireOp",EDGE,"E103.sketch_text.stroke-64"),sQuery(id+"F0.wireOp",EDGE,"E103.sketch_text.stroke-65"),sQuery(id+"F0.wireOp",EDGE,"E103.sketch_text.stroke-66"),sQuery(id+"F0.wireOp",EDGE,"E103.sketch_text.stroke-67"),sQuery(id+"F0.wireOp",EDGE,"E103.sketch_text.stroke-68"),sQuery(id+"F0.wireOp",EDGE,"E103.sketch_text.stroke-69"),sQuery(id+"F0.wireOp",EDGE,"E103.sketch_text.stroke-70"),sQuery(id+"F0.wireOp",EDGE,"E103.sketch_text.stroke-71"),sQuery(id+"F0.wireOp",EDGE,"E103.sketch_text.stroke-72"),sQuery(id+"F0.wireOp",EDGE,"E103.sketch_text.stroke-73"),sQuery(id+"F0.wireOp",EDGE,"E103.sketch_text.stroke-74"),sQuery(id+"F0.wireOp",EDGE,"E103.sketch_text.stroke-75"),sQuery(id+"F0.wireOp",EDGE,"E103.sketch_text.stroke-76"),sQuery(id+"F0.wireOp",EDGE,"E103.sketch_text.stroke-77"),sQuery(id+"F0.wireOp",EDGE,"E103.sketch_text.stroke-78"),sQuery(id+"F0.wireOp",EDGE,"E106.sketch_text.stroke-0"),sQuery(id+"F0.wireOp",EDGE,"E106.sketch_text.stroke-1"),sQuery(id+"F0.wireOp",EDGE,"E106.sketch_text.stroke-2"),sQuery(id+"F0.wireOp",EDGE,"E106.sketch_text.stroke-3"),sQuery(id+"F0.wireOp",EDGE,"E106.sketch_text.stroke-4"),sQuery(id+"F0.wireOp",EDGE,"E106.sketch_text.stroke-5"),sQuery(id+"F0.wireOp",EDGE,"E106.sketch_text.stroke-6"),sQuery(id+"F0.wireOp",EDGE,"E106.sketch_text.stroke-7"),sQuery(id+"F0.wireOp",EDGE,"E106.sketch_text.stroke-8"),sQuery(id+"F0.wireOp",EDGE,"E106.sketch_text.stroke-9"),sQuery(id+"F0.wireOp",EDGE,"E106.sketch_text.stroke-10"),sQuery(id+"F0.wireOp",EDGE,"E106.sketch_text.stroke-11"),sQuery(id+"F0.wireOp",EDGE,"E106.sketch_text.stroke-12"),sQuery(id+"F0.wireOp",EDGE,"E106.sketch_text.stroke-13"),sQuery(id+"F0.wireOp",EDGE,"E106.sketch_text.stroke-14"),sQuery(id+"F0.wireOp",EDGE,"E106.sketch_text.stroke-15"),sQuery(id+"F0.wireOp",EDGE,"E106.sketch_text.stroke-16"),sQuery(id+"F0.wireOp",EDGE,"E106.sketch_text.stroke-17"),sQuery(id+"F0.wireOp",EDGE,"E106.sketch_text.stroke-26"),sQuery(id+"F0.wireOp",EDGE,"E106.sketch_text.stroke-27"),sQuery(id+"F0.wireOp",EDGE,"E106.sketch_text.stroke-28"),sQuery(id+"F0.wireOp",EDGE,"E106.sketch_text.stroke-29"),sQuery(id+"F0.wireOp",EDGE,"E106.sketch_text.stroke-30"),sQuery(id+"F0.wireOp",EDGE,"E106.sketch_text.stroke-31"),sQuery(id+"F0.wireOp",EDGE,"E106.sketch_text.stroke-32"),sQuery(id+"F0.wireOp",EDGE,"E106.sketch_text.stroke-33"),sQuery(id+"F0.wireOp",EDGE,"E106.sketch_text.stroke-34"),sQuery(id+"F0.wireOp",EDGE,"E106.sketch_text.stroke-35"),sQuery(id+"F0.wireOp",EDGE,"E106.sketch_text.stroke-36"),sQuery(id+"F0.wireOp",EDGE,"E106.sketch_text.stroke-37"),sQuery(id+"F0.wireOp",EDGE,"E106.sketch_text.stroke-38"),sQuery(id+"F0.wireOp",EDGE,"E106.sketch_text.stroke-39"),sQuery(id+"F0.wireOp",EDGE,"E106.sketch_text.stroke-40"),sQuery(id+"F0.wireOp",EDGE,"E106.sketch_text.stroke-41"),sQuery(id+"F0.wireOp",EDGE,"E106.sketch_text.stroke-42"),sQuery(id+"F0.wireOp",EDGE,"E106.sketch_text.stroke-48"),sQuery(id+"F0.wireOp",EDGE,"E106.sketch_text.stroke-49"),sQuery(id+"F0.wireOp",EDGE,"E106.sketch_text.stroke-50"),sQuery(id+"F0.wireOp",EDGE,"E106.sketch_text.stroke-51"),sQuery(id+"F0.wireOp",EDGE,"E106.sketch_text.stroke-52"),sQuery(id+"F0.wireOp",EDGE,"E106.sketch_text.stroke-53"),sQuery(id+"F0.wireOp",EDGE,"E106.sketch_text.stroke-54"),sQuery(id+"F0.wireOp",EDGE,"E106.sketch_text.stroke-55"),sQuery(id+"F0.wireOp",EDGE,"E106.sketch_text.stroke-56"),sQuery(id+"F0.wireOp",EDGE,"E106.sketch_text.stroke-57"),sQuery(id+"F0.wireOp",EDGE,"E106.sketch_text.stroke-58"),sQuery(id+"F0.wireOp",EDGE,"E106.sketch_text.stroke-59"),sQuery(id+"F0.wireOp",EDGE,"E106.sketch_text.stroke-60"),sQuery(id+"F0.wireOp",EDGE,"E106.sketch_text.stroke-61"),sQuery(id+"F0.wireOp",EDGE,"E106.sketch_text.stroke-62"),sQuery(id+"F0.wireOp",EDGE,"E109.sketch_text.stroke-0"),sQuery(id+"F0.wireOp",EDGE,"E109.sketch_text.stroke-1"),sQuery(id+"F0.wireOp",EDGE,"E109.sketch_text.stroke-2"),sQuery(id+"F0.wireOp",EDGE,"E109.sketch_text.stroke-3"),sQuery(id+"F0.wireOp",EDGE,"E109.sketch_text.stroke-4"),sQuery(id+"F0.wireOp",EDGE,"E109.sketch_text.stroke-5"),sQuery(id+"F0.wireOp",EDGE,"E109.sketch_text.stroke-14"),sQuery(id+"F0.wireOp",EDGE,"E109.sketch_text.stroke-15"),sQuery(id+"F0.wireOp",EDGE,"E109.sketch_text.stroke-16"),sQuery(id+"F0.wireOp",EDGE,"E109.sketch_text.stroke-17"),sQuery(id+"F0.wireOp",EDGE,"E109.sketch_text.stroke-18"),sQuery(id+"F0.wireOp",EDGE,"E109.sketch_text.stroke-19"),sQuery(id+"F0.wireOp",EDGE,"E109.sketch_text.stroke-20"),sQuery(id+"F0.wireOp",EDGE,"E109.sketch_text.stroke-21"),sQuery(id+"F0.wireOp",EDGE,"E109.sketch_text.stroke-22"),sQuery(id+"F0.wireOp",EDGE,"E109.sketch_text.stroke-23"),sQuery(id+"F0.wireOp",EDGE,"E109.sketch_text.stroke-32"),sQuery(id+"F0.wireOp",EDGE,"E109.sketch_text.stroke-33"),sQuery(id+"F0.wireOp",EDGE,"E109.sketch_text.stroke-34"),sQuery(id+"F0.wireOp",EDGE,"E109.sketch_text.stroke-35"),sQuery(id+"F0.wireOp",EDGE,"E109.sketch_text.stroke-36"),sQuery(id+"F0.wireOp",EDGE,"E109.sketch_text.stroke-37"),sQuery(id+"F0.wireOp",EDGE,"E109.sketch_text.stroke-38"),sQuery(id+"F0.wireOp",EDGE,"E109.sketch_text.stroke-39"),sQuery(id+"F0.wireOp",EDGE,"E109.sketch_text.stroke-40"),sQuery(id+"F0.wireOp",EDGE,"E109.sketch_text.stroke-41"),sQuery(id+"F0.wireOp",EDGE,"E109.sketch_text.stroke-42"),sQuery(id+"F0.wireOp",EDGE,"E109.sketch_text.stroke-43"),sQuery(id+"F0.wireOp",EDGE,"E109.sketch_text.stroke-44"),sQuery(id+"F0.wireOp",EDGE,"E109.sketch_text.stroke-45"),sQuery(id+"F0.wireOp",EDGE,"E109.sketch_text.stroke-46"),sQuery(id+"F0.wireOp",EDGE,"E109.sketch_text.stroke-47"),sQuery(id+"F0.wireOp",EDGE,"E109.sketch_text.stroke-48"),sQuery(id+"F0.wireOp",EDGE,"E109.sketch_text.stroke-49"),sQuery(id+"F0.wireOp",EDGE,"E109.sketch_text.stroke-50"),sQuery(id+"F0.wireOp",EDGE,"E109.sketch_text.stroke-51"),sQuery(id+"F0.wireOp",EDGE,"E109.sketch_text.stroke-52"),sQuery(id+"F0.wireOp",EDGE,"E109.sketch_text.stroke-53"),sQuery(id+"F0.wireOp",EDGE,"E109.sketch_text.stroke-54"),sQuery(id+"F0.wireOp",EDGE,"E109.sketch_text.stroke-55"),sQuery(id+"F0.wireOp",EDGE,"E109.sketch_text.stroke-56"),sQuery(id+"F0.wireOp",EDGE,"E109.sketch_text.stroke-65"),sQuery(id+"F0.wireOp",EDGE,"E109.sketch_text.stroke-66"),sQuery(id+"F0.wireOp",EDGE,"E109.sketch_text.stroke-67"),sQuery(id+"F0.wireOp",EDGE,"E109.sketch_text.stroke-68"),sQuery(id+"F0.wireOp",EDGE,"E109.sketch_text.stroke-69"),sQuery(id+"F0.wireOp",EDGE,"E109.sketch_text.stroke-70"),sQuery(id+"F0.wireOp",EDGE,"E109.sketch_text.stroke-71"),sQuery(id+"F0.wireOp",EDGE,"E109.sketch_text.stroke-72"),sQuery(id+"F0.wireOp",EDGE,"E109.sketch_text.stroke-73"),sQuery(id+"F0.wireOp",EDGE,"E109.sketch_text.stroke-74"),sQuery(id+"F0.wireOp",EDGE,"E109.sketch_text.stroke-75"),sQuery(id+"F0.wireOp",EDGE,"E109.sketch_text.stroke-76"),sQuery(id+"F0.wireOp",EDGE,"E109.sketch_text.stroke-77"),sQuery(id+"F0.wireOp",EDGE,"E109.sketch_text.stroke-78"),sQuery(id+"F0.wireOp",EDGE,"E109.sketch_text.stroke-79"),sQuery(id+"F0.wireOp",EDGE,"E109.sketch_text.stroke-80"),sQuery(id+"F0.wireOp",EDGE,"E109.sketch_text.stroke-81"),sQuery(id+"F0.wireOp",EDGE,"E109.sketch_text.stroke-82"),sQuery(id+"F0.wireOp",EDGE,"E109.sketch_text.stroke-83"),sQuery(id+"F0.wireOp",EDGE,"E109.sketch_text.stroke-84"),sQuery(id+"F0.wireOp",EDGE,"E109.sketch_text.stroke-85"),sQuery(id+"F0.wireOp",EDGE,"E109.sketch_text.stroke-86"),sQuery(id+"F0.wireOp",EDGE,"E109.sketch_text.stroke-87"),sQuery(id+"F0.wireOp",EDGE,"E109.sketch_text.stroke-88"),sQuery(id+"F0.wireOp",EDGE,"E109.sketch_text.stroke-89"),sQuery(id+"F0.wireOp",EDGE,"E109.sketch_text.stroke-90"),sQuery(id+"F0.wireOp",EDGE,"E109.sketch_text.stroke-91"),sQuery(id+"F0.wireOp",EDGE,"E109.sketch_text.stroke-92"),sQuery(id+"F0.wireOp",EDGE,"E109.sketch_text.stroke-97"),sQuery(id+"F0.wireOp",EDGE,"E109.sketch_text.stroke-98"),sQuery(id+"F0.wireOp",EDGE,"E109.sketch_text.stroke-99"),sQuery(id+"F0.wireOp",EDGE,"E109.sketch_text.stroke-100"),sQuery(id+"F0.wireOp",EDGE,"E109.sketch_text.stroke-101"),sQuery(id+"F0.wireOp",EDGE,"E109.sketch_text.stroke-102"),sQuery(id+"F0.wireOp",EDGE,"E109.sketch_text.stroke-103"),sQuery(id+"F0.wireOp",EDGE,"E109.sketch_text.stroke-104"),sQuery(id+"F0.wireOp",EDGE,"E109.sketch_text.stroke-105"),sQuery(id+"F0.wireOp",EDGE,"E109.sketch_text.stroke-106"),sQuery(id+"F0.wireOp",EDGE,"E112.sketch_text.stroke-0"),sQuery(id+"F0.wireOp",EDGE,"E112.sketch_text.stroke-1"),sQuery(id+"F0.wireOp",EDGE,"E112.sketch_text.stroke-2"),sQuery(id+"F0.wireOp",EDGE,"E112.sketch_text.stroke-3"),sQuery(id+"F0.wireOp",EDGE,"E112.sketch_text.stroke-4"),sQuery(id+"F0.wireOp",EDGE,"E112.sketch_text.stroke-5"),sQuery(id+"F0.wireOp",EDGE,"E112.sketch_text.stroke-14"),sQuery(id+"F0.wireOp",EDGE,"E112.sketch_text.stroke-15"),sQuery(id+"F0.wireOp",EDGE,"E112.sketch_text.stroke-16"),sQuery(id+"F0.wireOp",EDGE,"E112.sketch_text.stroke-17"),sQuery(id+"F0.wireOp",EDGE,"E112.sketch_text.stroke-18"),sQuery(id+"F0.wireOp",EDGE,"E112.sketch_text.stroke-19"),sQuery(id+"F0.wireOp",EDGE,"E112.sketch_text.stroke-20"),sQuery(id+"F0.wireOp",EDGE,"E112.sketch_text.stroke-21"),sQuery(id+"F0.wireOp",EDGE,"E112.sketch_text.stroke-22"),sQuery(id+"F0.wireOp",EDGE,"E112.sketch_text.stroke-23"),sQuery(id+"F0.wireOp",EDGE,"E112.sketch_text.stroke-32"),sQuery(id+"F0.wireOp",EDGE,"E112.sketch_text.stroke-33"),sQuery(id+"F0.wireOp",EDGE,"E112.sketch_text.stroke-34"),sQuery(id+"F0.wireOp",EDGE,"E112.sketch_text.stroke-35"),sQuery(id+"F0.wireOp",EDGE,"E112.sketch_text.stroke-36"),sQuery(id+"F0.wireOp",EDGE,"E112.sketch_text.stroke-37"),sQuery(id+"F0.wireOp",EDGE,"E112.sketch_text.stroke-38"),sQuery(id+"F0.wireOp",EDGE,"E112.sketch_text.stroke-39"),sQuery(id+"F0.wireOp",EDGE,"E112.sketch_text.stroke-40"),sQuery(id+"F0.wireOp",EDGE,"E112.sketch_text.stroke-41"),sQuery(id+"F0.wireOp",EDGE,"E112.sketch_text.stroke-42"),sQuery(id+"F0.wireOp",EDGE,"E112.sketch_text.stroke-43"),sQuery(id+"F0.wireOp",EDGE,"E112.sketch_text.stroke-44"),sQuery(id+"F0.wireOp",EDGE,"E112.sketch_text.stroke-45"),sQuery(id+"F0.wireOp",EDGE,"E112.sketch_text.stroke-46"),sQuery(id+"F0.wireOp",EDGE,"E112.sketch_text.stroke-47"),sQuery(id+"F0.wireOp",EDGE,"E112.sketch_text.stroke-48"),sQuery(id+"F0.wireOp",EDGE,"E112.sketch_text.stroke-49"),sQuery(id+"F0.wireOp",EDGE,"E112.sketch_text.stroke-50"),sQuery(id+"F0.wireOp",EDGE,"E112.sketch_text.stroke-51"),sQuery(id+"F0.wireOp",EDGE,"E112.sketch_text.stroke-52"),sQuery(id+"F0.wireOp",EDGE,"E112.sketch_text.stroke-53"),sQuery(id+"F0.wireOp",EDGE,"E112.sketch_text.stroke-54"),sQuery(id+"F0.wireOp",EDGE,"E112.sketch_text.stroke-55"),sQuery(id+"F0.wireOp",EDGE,"E112.sketch_text.stroke-56"),sQuery(id+"F0.wireOp",EDGE,"E112.sketch_text.stroke-65"),sQuery(id+"F0.wireOp",EDGE,"E112.sketch_text.stroke-66"),sQuery(id+"F0.wireOp",EDGE,"E112.sketch_text.stroke-67"),sQuery(id+"F0.wireOp",EDGE,"E112.sketch_text.stroke-68"),sQuery(id+"F0.wireOp",EDGE,"E112.sketch_text.stroke-69"),sQuery(id+"F0.wireOp",EDGE,"E112.sketch_text.stroke-70"),sQuery(id+"F0.wireOp",EDGE,"E112.sketch_text.stroke-71"),sQuery(id+"F0.wireOp",EDGE,"E112.sketch_text.stroke-72"),sQuery(id+"F0.wireOp",EDGE,"E112.sketch_text.stroke-73"),sQuery(id+"F0.wireOp",EDGE,"E112.sketch_text.stroke-74"),sQuery(id+"F0.wireOp",EDGE,"E112.sketch_text.stroke-75"),sQuery(id+"F0.wireOp",EDGE,"E112.sketch_text.stroke-76"),sQuery(id+"F0.wireOp",EDGE,"E112.sketch_text.stroke-77"),sQuery(id+"F0.wireOp",EDGE,"E112.sketch_text.stroke-78"),sQuery(id+"F0.wireOp",EDGE,"E112.sketch_text.stroke-79"),sQuery(id+"F0.wireOp",EDGE,"E112.sketch_text.stroke-80"),sQuery(id+"F0.wireOp",EDGE,"E112.sketch_text.stroke-81"),sQuery(id+"F0.wireOp",EDGE,"E112.sketch_text.stroke-82"),sQuery(id+"F0.wireOp",EDGE,"E112.sketch_text.stroke-83"),sQuery(id+"F0.wireOp",EDGE,"E112.sketch_text.stroke-84"),sQuery(id+"F0.wireOp",EDGE,"E112.sketch_text.stroke-85"),sQuery(id+"F0.wireOp",EDGE,"E112.sketch_text.stroke-86"),sQuery(id+"F0.wireOp",EDGE,"E112.sketch_text.stroke-87"),sQuery(id+"F0.wireOp",EDGE,"E112.sketch_text.stroke-88"),sQuery(id+"F0.wireOp",EDGE,"E112.sketch_text.stroke-89"),sQuery(id+"F0.wireOp",EDGE,"E112.sketch_text.stroke-90"),sQuery(id+"F0.wireOp",EDGE,"E112.sketch_text.stroke-91"),sQuery(id+"F0.wireOp",EDGE,"E112.sketch_text.stroke-92"),sQuery(id+"F0.wireOp",EDGE,"E112.sketch_text.stroke-97"),sQuery(id+"F0.wireOp",EDGE,"E112.sketch_text.stroke-98"),sQuery(id+"F0.wireOp",EDGE,"E112.sketch_text.stroke-99"),sQuery(id+"F0.wireOp",EDGE,"E112.sketch_text.stroke-100"),sQuery(id+"F0.wireOp",EDGE,"E112.sketch_text.stroke-101"),sQuery(id+"F0.wireOp",EDGE,"E112.sketch_text.stroke-102"),sQuery(id+"F0.wireOp",EDGE,"E112.sketch_text.stroke-103"),sQuery(id+"F0.wireOp",EDGE,"E112.sketch_text.stroke-104"),sQuery(id+"F0.wireOp",EDGE,"E112.sketch_text.stroke-105"),sQuery(id+"F0.wireOp",EDGE,"E112.sketch_text.stroke-106"),sQuery(id+"F0.wireOp",EDGE,"E112.sketch_text.stroke-107"),sQuery(id+"F0.wireOp",EDGE,"E112.sketch_text.stroke-108"),sQuery(id+"F0.wireOp",EDGE,"E112.sketch_text.stroke-109"),sQuery(id+"F0.wireOp",EDGE,"E112.sketch_text.stroke-110"),sQuery(id+"F0.wireOp",EDGE,"E112.sketch_text.stroke-111"),sQuery(id+"F0.wireOp",EDGE,"E112.sketch_text.stroke-112"),sQuery(id+"F0.wireOp",EDGE,"E112.sketch_text.stroke-113"),sQuery(id+"F0.wireOp",EDGE,"E112.sketch_text.stroke-114"),sQuery(id+"F0.wireOp",EDGE,"E112.sketch_text.stroke-115"),sQuery(id+"F0.wireOp",EDGE,"E112.sketch_text.stroke-116"),sQuery(id+"F0.wireOp",EDGE,"E112.sketch_text.stroke-117"),sQuery(id+"F0.wireOp",EDGE,"E112.sketch_text.stroke-118"),sQuery(id+"F0.wireOp",EDGE,"E112.sketch_text.stroke-119"),sQuery(id+"F0.wireOp",EDGE,"E112.sketch_text.stroke-120"),sQuery(id+"F0.wireOp",EDGE,"E113"),sQuery(id+"F0.wireOp",EDGE,"E114"),sQuery(id+"F0.wireOp",EDGE,"E120"),sQuery(id+"F0.wireOp",EDGE,"E121"),sQuery(id+"F0.wireOp",EDGE,"E124.sketch_text.stroke-0"),sQuery(id+"F0.wireOp",EDGE,"E124.sketch_text.stroke-1"),sQuery(id+"F0.wireOp",EDGE,"E124.sketch_text.stroke-2"),sQuery(id+"F0.wireOp",EDGE,"E124.sketch_text.stroke-3")])],"isStart":false});
            var sketch = newSketch(context, id + "F3", { "sketchPlane" : qUnion([Q0])});
            skPoint(sketch, "E126", {"position": v(-87.5, 14.38) * mm});
            skPoint(sketch, "E127", {"position": v(-87.5, -14.37) * mm});
            skPoint(sketch, "E128", {"position": v(-93.75, 8.13) * mm});
            skPoint(sketch, "E129", {"position": v(93.75, 8.13) * mm});
            skPoint(sketch, "E130", {"position": v(-93.75, -8.13) * mm});
            skPoint(sketch, "E131", {"position": v(93.75, -8.12) * mm});
            skPoint(sketch, "E132", {"position": v(87.5, 14.38) * mm});
            skPoint(sketch, "E133", {"position": v(87.5, -14.37) * mm});
            skPoint(sketch, "E134", {"position": v(-87.5, 8.13) * mm});
            skPoint(sketch, "E135", {"position": v(-87.5, -8.13) * mm});
            skPoint(sketch, "E136", {"position": v(87.5, 8.13) * mm});
            skPoint(sketch, "E137", {"position": v(87.5, -8.12) * mm});
            skPoint(sketch, "E138", {"position": v(0, 8.13) * mm});
            skPoint(sketch, "E139", {"position": v(-0.01, -8.12) * mm});
            skSolve(sketch);
        }
        {
            var Q0;
            Q0=sQuery(id+"F3.wireOp",VERTEX,"E134");
            var Q1;
            Q1=sQuery(id+"F3.wireOp",VERTEX,"E135");
            var Q2;
            Q2=sQuery(id+"F3.wireOp",VERTEX,"E138");
            var Q3;
            Q3=sQuery(id+"F3.wireOp",VERTEX,"E139");
            var Q4;
            Q4=sQuery(id+"F3.wireOp",VERTEX,"E136");
            var Q5;
            Q5=sQuery(id+"F3.wireOp",VERTEX,"E137");
            var Q6;
            Q6=makeQuery(id+"F2.opExtrude","SWEPT_BODY",BODY,{"disambiguationData":[OSD([sQuery(id+"F0.wireOp",EDGE,"E0.bottom"),sQuery(id+"F0.wireOp",EDGE,"E0.top"),sQuery(id+"F0.wireOp",EDGE,"E0.left"),sQuery(id+"F0.wireOp",EDGE,"E0.right"),sQuery(id+"F0.wireOp",EDGE,"E44"),sQuery(id+"F0.wireOp",EDGE,"E45"),sQuery(id+"F0.wireOp",EDGE,"E46"),sQuery(id+"F0.wireOp",EDGE,"E47"),sQuery(id+"F0.wireOp",EDGE,"E48"),sQuery(id+"F0.wireOp",EDGE,"E49"),sQuery(id+"F0.wireOp",EDGE,"E50"),sQuery(id+"F0.wireOp",EDGE,"E67.sketch_text.stroke-0"),sQuery(id+"F0.wireOp",EDGE,"E67.sketch_text.stroke-1"),sQuery(id+"F0.wireOp",EDGE,"E67.sketch_text.stroke-2"),sQuery(id+"F0.wireOp",EDGE,"E67.sketch_text.stroke-3"),sQuery(id+"F0.wireOp",EDGE,"E67.sketch_text.stroke-4"),sQuery(id+"F0.wireOp",EDGE,"E67.sketch_text.stroke-5"),sQuery(id+"F0.wireOp",EDGE,"E67.sketch_text.stroke-14"),sQuery(id+"F0.wireOp",EDGE,"E67.sketch_text.stroke-15"),sQuery(id+"F0.wireOp",EDGE,"E67.sketch_text.stroke-16"),sQuery(id+"F0.wireOp",EDGE,"E67.sketch_text.stroke-17"),sQuery(id+"F0.wireOp",EDGE,"E67.sketch_text.stroke-18"),sQuery(id+"F0.wireOp",EDGE,"E67.sketch_text.stroke-19"),sQuery(id+"F0.wireOp",EDGE,"E67.sketch_text.stroke-20"),sQuery(id+"F0.wireOp",EDGE,"E67.sketch_text.stroke-21"),sQuery(id+"F0.wireOp",EDGE,"E67.sketch_text.stroke-22"),sQuery(id+"F0.wireOp",EDGE,"E67.sketch_text.stroke-23"),sQuery(id+"F0.wireOp",EDGE,"E67.sketch_text.stroke-32"),sQuery(id+"F0.wireOp",EDGE,"E67.sketch_text.stroke-33"),sQuery(id+"F0.wireOp",EDGE,"E67.sketch_text.stroke-34"),sQuery(id+"F0.wireOp",EDGE,"E67.sketch_text.stroke-35"),sQuery(id+"F0.wireOp",EDGE,"E67.sketch_text.stroke-36"),sQuery(id+"F0.wireOp",EDGE,"E67.sketch_text.stroke-37"),sQuery(id+"F0.wireOp",EDGE,"E67.sketch_text.stroke-38"),sQuery(id+"F0.wireOp",EDGE,"E67.sketch_text.stroke-39"),sQuery(id+"F0.wireOp",EDGE,"E67.sketch_text.stroke-40"),sQuery(id+"F0.wireOp",EDGE,"E67.sketch_text.stroke-41"),sQuery(id+"F0.wireOp",EDGE,"E67.sketch_text.stroke-42"),sQuery(id+"F0.wireOp",EDGE,"E67.sketch_text.stroke-43"),sQuery(id+"F0.wireOp",EDGE,"E67.sketch_text.stroke-44"),sQuery(id+"F0.wireOp",EDGE,"E67.sketch_text.stroke-45"),sQuery(id+"F0.wireOp",EDGE,"E67.sketch_text.stroke-46"),sQuery(id+"F0.wireOp",EDGE,"E67.sketch_text.stroke-47"),sQuery(id+"F0.wireOp",EDGE,"E67.sketch_text.stroke-48"),sQuery(id+"F0.wireOp",EDGE,"E67.sketch_text.stroke-49"),sQuery(id+"F0.wireOp",EDGE,"E67.sketch_text.stroke-50"),sQuery(id+"F0.wireOp",EDGE,"E67.sketch_text.stroke-51"),sQuery(id+"F0.wireOp",EDGE,"E67.sketch_text.stroke-52"),sQuery(id+"F0.wireOp",EDGE,"E67.sketch_text.stroke-53"),sQuery(id+"F0.wireOp",EDGE,"E67.sketch_text.stroke-54"),sQuery(id+"F0.wireOp",EDGE,"E67.sketch_text.stroke-55"),sQuery(id+"F0.wireOp",EDGE,"E67.sketch_text.stroke-56"),sQuery(id+"F0.wireOp",EDGE,"E67.sketch_text.stroke-65"),sQuery(id+"F0.wireOp",EDGE,"E67.sketch_text.stroke-66"),sQuery(id+"F0.wireOp",EDGE,"E67.sketch_text.stroke-67"),sQuery(id+"F0.wireOp",EDGE,"E67.sketch_text.stroke-68"),sQuery(id+"F0.wireOp",EDGE,"E67.sketch_text.stroke-69"),sQuery(id+"F0.wireOp",EDGE,"E67.sketch_text.stroke-70"),sQuery(id+"F0.wireOp",EDGE,"E67.sketch_text.stroke-71"),sQuery(id+"F0.wireOp",EDGE,"E67.sketch_text.stroke-72"),sQuery(id+"F0.wireOp",EDGE,"E67.sketch_text.stroke-73"),sQuery(id+"F0.wireOp",EDGE,"E67.sketch_text.stroke-74"),sQuery(id+"F0.wireOp",EDGE,"E67.sketch_text.stroke-75"),sQuery(id+"F0.wireOp",EDGE,"E67.sketch_text.stroke-76"),sQuery(id+"F0.wireOp",EDGE,"E67.sketch_text.stroke-77"),sQuery(id+"F0.wireOp",EDGE,"E67.sketch_text.stroke-78"),sQuery(id+"F0.wireOp",EDGE,"E67.sketch_text.stroke-79"),sQuery(id+"F0.wireOp",EDGE,"E67.sketch_text.stroke-80"),sQuery(id+"F0.wireOp",EDGE,"E67.sketch_text.stroke-81"),sQuery(id+"F0.wireOp",EDGE,"E67.sketch_text.stroke-82"),sQuery(id+"F0.wireOp",EDGE,"E67.sketch_text.stroke-83"),sQuery(id+"F0.wireOp",EDGE,"E67.sketch_text.stroke-84"),sQuery(id+"F0.wireOp",EDGE,"E67.sketch_text.stroke-85"),sQuery(id+"F0.wireOp",EDGE,"E67.sketch_text.stroke-86"),sQuery(id+"F0.wireOp",EDGE,"E67.sketch_text.stroke-87"),sQuery(id+"F0.wireOp",EDGE,"E67.sketch_text.stroke-88"),sQuery(id+"F0.wireOp",EDGE,"E67.sketch_text.stroke-89"),sQuery(id+"F0.wireOp",EDGE,"E67.sketch_text.stroke-90"),sQuery(id+"F0.wireOp",EDGE,"E67.sketch_text.stroke-91"),sQuery(id+"F0.wireOp",EDGE,"E67.sketch_text.stroke-92"),sQuery(id+"F0.wireOp",EDGE,"E67.sketch_text.stroke-97"),sQuery(id+"F0.wireOp",EDGE,"E67.sketch_text.stroke-98"),sQuery(id+"F0.wireOp",EDGE,"E67.sketch_text.stroke-99"),sQuery(id+"F0.wireOp",EDGE,"E67.sketch_text.stroke-100"),sQuery(id+"F0.wireOp",EDGE,"E67.sketch_text.stroke-101"),sQuery(id+"F0.wireOp",EDGE,"E67.sketch_text.stroke-102"),sQuery(id+"F0.wireOp",EDGE,"E67.sketch_text.stroke-103"),sQuery(id+"F0.wireOp",EDGE,"E67.sketch_text.stroke-104"),sQuery(id+"F0.wireOp",EDGE,"E67.sketch_text.stroke-105"),sQuery(id+"F0.wireOp",EDGE,"E67.sketch_text.stroke-106"),sQuery(id+"F0.wireOp",EDGE,"E70.sketch_text.stroke-0"),sQuery(id+"F0.wireOp",EDGE,"E70.sketch_text.stroke-1"),sQuery(id+"F0.wireOp",EDGE,"E70.sketch_text.stroke-2"),sQuery(id+"F0.wireOp",EDGE,"E70.sketch_text.stroke-3"),sQuery(id+"F0.wireOp",EDGE,"E70.sketch_text.stroke-4"),sQuery(id+"F0.wireOp",EDGE,"E70.sketch_text.stroke-5"),sQuery(id+"F0.wireOp",EDGE,"E70.sketch_text.stroke-14"),sQuery(id+"F0.wireOp",EDGE,"E70.sketch_text.stroke-15"),sQuery(id+"F0.wireOp",EDGE,"E70.sketch_text.stroke-16"),sQuery(id+"F0.wireOp",EDGE,"E70.sketch_text.stroke-17"),sQuery(id+"F0.wireOp",EDGE,"E70.sketch_text.stroke-18"),sQuery(id+"F0.wireOp",EDGE,"E70.sketch_text.stroke-19"),sQuery(id+"F0.wireOp",EDGE,"E70.sketch_text.stroke-20"),sQuery(id+"F0.wireOp",EDGE,"E70.sketch_text.stroke-21"),sQuery(id+"F0.wireOp",EDGE,"E70.sketch_text.stroke-22"),sQuery(id+"F0.wireOp",EDGE,"E70.sketch_text.stroke-23"),sQuery(id+"F0.wireOp",EDGE,"E70.sketch_text.stroke-32"),sQuery(id+"F0.wireOp",EDGE,"E70.sketch_text.stroke-33"),sQuery(id+"F0.wireOp",EDGE,"E70.sketch_text.stroke-34"),sQuery(id+"F0.wireOp",EDGE,"E70.sketch_text.stroke-35"),sQuery(id+"F0.wireOp",EDGE,"E70.sketch_text.stroke-36"),sQuery(id+"F0.wireOp",EDGE,"E70.sketch_text.stroke-37"),sQuery(id+"F0.wireOp",EDGE,"E70.sketch_text.stroke-38"),sQuery(id+"F0.wireOp",EDGE,"E70.sketch_text.stroke-39"),sQuery(id+"F0.wireOp",EDGE,"E70.sketch_text.stroke-40"),sQuery(id+"F0.wireOp",EDGE,"E70.sketch_text.stroke-41"),sQuery(id+"F0.wireOp",EDGE,"E70.sketch_text.stroke-42"),sQuery(id+"F0.wireOp",EDGE,"E70.sketch_text.stroke-43"),sQuery(id+"F0.wireOp",EDGE,"E70.sketch_text.stroke-44"),sQuery(id+"F0.wireOp",EDGE,"E70.sketch_text.stroke-45"),sQuery(id+"F0.wireOp",EDGE,"E70.sketch_text.stroke-46"),sQuery(id+"F0.wireOp",EDGE,"E70.sketch_text.stroke-47"),sQuery(id+"F0.wireOp",EDGE,"E70.sketch_text.stroke-48"),sQuery(id+"F0.wireOp",EDGE,"E70.sketch_text.stroke-49"),sQuery(id+"F0.wireOp",EDGE,"E70.sketch_text.stroke-50"),sQuery(id+"F0.wireOp",EDGE,"E70.sketch_text.stroke-51"),sQuery(id+"F0.wireOp",EDGE,"E70.sketch_text.stroke-52"),sQuery(id+"F0.wireOp",EDGE,"E70.sketch_text.stroke-53"),sQuery(id+"F0.wireOp",EDGE,"E70.sketch_text.stroke-54"),sQuery(id+"F0.wireOp",EDGE,"E70.sketch_text.stroke-55"),sQuery(id+"F0.wireOp",EDGE,"E70.sketch_text.stroke-56"),sQuery(id+"F0.wireOp",EDGE,"E70.sketch_text.stroke-65"),sQuery(id+"F0.wireOp",EDGE,"E70.sketch_text.stroke-66"),sQuery(id+"F0.wireOp",EDGE,"E70.sketch_text.stroke-67"),sQuery(id+"F0.wireOp",EDGE,"E70.sketch_text.stroke-68"),sQuery(id+"F0.wireOp",EDGE,"E70.sketch_text.stroke-69"),sQuery(id+"F0.wireOp",EDGE,"E70.sketch_text.stroke-70"),sQuery(id+"F0.wireOp",EDGE,"E70.sketch_text.stroke-71"),sQuery(id+"F0.wireOp",EDGE,"E70.sketch_text.stroke-72"),sQuery(id+"F0.wireOp",EDGE,"E70.sketch_text.stroke-73"),sQuery(id+"F0.wireOp",EDGE,"E70.sketch_text.stroke-74"),sQuery(id+"F0.wireOp",EDGE,"E70.sketch_text.stroke-75"),sQuery(id+"F0.wireOp",EDGE,"E70.sketch_text.stroke-76"),sQuery(id+"F0.wireOp",EDGE,"E70.sketch_text.stroke-77"),sQuery(id+"F0.wireOp",EDGE,"E70.sketch_text.stroke-78"),sQuery(id+"F0.wireOp",EDGE,"E70.sketch_text.stroke-79"),sQuery(id+"F0.wireOp",EDGE,"E70.sketch_text.stroke-80"),sQuery(id+"F0.wireOp",EDGE,"E70.sketch_text.stroke-81"),sQuery(id+"F0.wireOp",EDGE,"E70.sketch_text.stroke-82"),sQuery(id+"F0.wireOp",EDGE,"E70.sketch_text.stroke-83"),sQuery(id+"F0.wireOp",EDGE,"E70.sketch_text.stroke-84"),sQuery(id+"F0.wireOp",EDGE,"E70.sketch_text.stroke-85"),sQuery(id+"F0.wireOp",EDGE,"E70.sketch_text.stroke-86"),sQuery(id+"F0.wireOp",EDGE,"E70.sketch_text.stroke-87"),sQuery(id+"F0.wireOp",EDGE,"E70.sketch_text.stroke-88"),sQuery(id+"F0.wireOp",EDGE,"E70.sketch_text.stroke-89"),sQuery(id+"F0.wireOp",EDGE,"E70.sketch_text.stroke-90"),sQuery(id+"F0.wireOp",EDGE,"E70.sketch_text.stroke-91"),sQuery(id+"F0.wireOp",EDGE,"E70.sketch_text.stroke-92"),sQuery(id+"F0.wireOp",EDGE,"E70.sketch_text.stroke-97"),sQuery(id+"F0.wireOp",EDGE,"E70.sketch_text.stroke-98"),sQuery(id+"F0.wireOp",EDGE,"E70.sketch_text.stroke-99"),sQuery(id+"F0.wireOp",EDGE,"E70.sketch_text.stroke-100"),sQuery(id+"F0.wireOp",EDGE,"E70.sketch_text.stroke-101"),sQuery(id+"F0.wireOp",EDGE,"E70.sketch_text.stroke-102"),sQuery(id+"F0.wireOp",EDGE,"E70.sketch_text.stroke-103"),sQuery(id+"F0.wireOp",EDGE,"E70.sketch_text.stroke-104"),sQuery(id+"F0.wireOp",EDGE,"E70.sketch_text.stroke-105"),sQuery(id+"F0.wireOp",EDGE,"E70.sketch_text.stroke-106"),sQuery(id+"F0.wireOp",EDGE,"E70.sketch_text.stroke-107"),sQuery(id+"F0.wireOp",EDGE,"E70.sketch_text.stroke-108"),sQuery(id+"F0.wireOp",EDGE,"E70.sketch_text.stroke-109"),sQuery(id+"F0.wireOp",EDGE,"E70.sketch_text.stroke-110"),sQuery(id+"F0.wireOp",EDGE,"E70.sketch_text.stroke-111"),sQuery(id+"F0.wireOp",EDGE,"E70.sketch_text.stroke-112"),sQuery(id+"F0.wireOp",EDGE,"E70.sketch_text.stroke-113"),sQuery(id+"F0.wireOp",EDGE,"E70.sketch_text.stroke-114"),sQuery(id+"F0.wireOp",EDGE,"E70.sketch_text.stroke-115"),sQuery(id+"F0.wireOp",EDGE,"E70.sketch_text.stroke-116"),sQuery(id+"F0.wireOp",EDGE,"E70.sketch_text.stroke-117"),sQuery(id+"F0.wireOp",EDGE,"E70.sketch_text.stroke-118"),sQuery(id+"F0.wireOp",EDGE,"E70.sketch_text.stroke-119"),sQuery(id+"F0.wireOp",EDGE,"E70.sketch_text.stroke-120"),sQuery(id+"F0.wireOp",EDGE,"E73.sketch_text.stroke-0"),sQuery(id+"F0.wireOp",EDGE,"E73.sketch_text.stroke-1"),sQuery(id+"F0.wireOp",EDGE,"E73.sketch_text.stroke-2"),sQuery(id+"F0.wireOp",EDGE,"E73.sketch_text.stroke-3"),sQuery(id+"F0.wireOp",EDGE,"E73.sketch_text.stroke-4"),sQuery(id+"F0.wireOp",EDGE,"E73.sketch_text.stroke-5"),sQuery(id+"F0.wireOp",EDGE,"E73.sketch_text.stroke-6"),sQuery(id+"F0.wireOp",EDGE,"E73.sketch_text.stroke-7"),sQuery(id+"F0.wireOp",EDGE,"E73.sketch_text.stroke-8"),sQuery(id+"F0.wireOp",EDGE,"E73.sketch_text.stroke-9"),sQuery(id+"F0.wireOp",EDGE,"E73.sketch_text.stroke-10"),sQuery(id+"F0.wireOp",EDGE,"E73.sketch_text.stroke-11"),sQuery(id+"F0.wireOp",EDGE,"E73.sketch_text.stroke-12"),sQuery(id+"F0.wireOp",EDGE,"E73.sketch_text.stroke-13"),sQuery(id+"F0.wireOp",EDGE,"E73.sketch_text.stroke-14"),sQuery(id+"F0.wireOp",EDGE,"E73.sketch_text.stroke-15"),sQuery(id+"F0.wireOp",EDGE,"E73.sketch_text.stroke-16"),sQuery(id+"F0.wireOp",EDGE,"E73.sketch_text.stroke-17"),sQuery(id+"F0.wireOp",EDGE,"E73.sketch_text.stroke-18"),sQuery(id+"F0.wireOp",EDGE,"E73.sketch_text.stroke-19"),sQuery(id+"F0.wireOp",EDGE,"E73.sketch_text.stroke-20"),sQuery(id+"F0.wireOp",EDGE,"E73.sketch_text.stroke-21"),sQuery(id+"F0.wireOp",EDGE,"E73.sketch_text.stroke-22"),sQuery(id+"F0.wireOp",EDGE,"E73.sketch_text.stroke-23"),sQuery(id+"F0.wireOp",EDGE,"E73.sketch_text.stroke-24"),sQuery(id+"F0.wireOp",EDGE,"E73.sketch_text.stroke-25"),sQuery(id+"F0.wireOp",EDGE,"E73.sketch_text.stroke-26"),sQuery(id+"F0.wireOp",EDGE,"E73.sketch_text.stroke-27"),sQuery(id+"F0.wireOp",EDGE,"E73.sketch_text.stroke-28"),sQuery(id+"F0.wireOp",EDGE,"E73.sketch_text.stroke-29"),sQuery(id+"F0.wireOp",EDGE,"E73.sketch_text.stroke-30"),sQuery(id+"F0.wireOp",EDGE,"E73.sketch_text.stroke-31"),sQuery(id+"F0.wireOp",EDGE,"E73.sketch_text.stroke-32"),sQuery(id+"F0.wireOp",EDGE,"E73.sketch_text.stroke-33"),sQuery(id+"F0.wireOp",EDGE,"E73.sketch_text.stroke-34"),sQuery(id+"F0.wireOp",EDGE,"E73.sketch_text.stroke-35"),sQuery(id+"F0.wireOp",EDGE,"E73.sketch_text.stroke-44"),sQuery(id+"F0.wireOp",EDGE,"E73.sketch_text.stroke-45"),sQuery(id+"F0.wireOp",EDGE,"E73.sketch_text.stroke-46"),sQuery(id+"F0.wireOp",EDGE,"E73.sketch_text.stroke-47"),sQuery(id+"F0.wireOp",EDGE,"E73.sketch_text.stroke-48"),sQuery(id+"F0.wireOp",EDGE,"E73.sketch_text.stroke-49"),sQuery(id+"F0.wireOp",EDGE,"E73.sketch_text.stroke-50"),sQuery(id+"F0.wireOp",EDGE,"E73.sketch_text.stroke-51"),sQuery(id+"F0.wireOp",EDGE,"E73.sketch_text.stroke-52"),sQuery(id+"F0.wireOp",EDGE,"E73.sketch_text.stroke-53"),sQuery(id+"F0.wireOp",EDGE,"E73.sketch_text.stroke-54"),sQuery(id+"F0.wireOp",EDGE,"E73.sketch_text.stroke-55"),sQuery(id+"F0.wireOp",EDGE,"E73.sketch_text.stroke-56"),sQuery(id+"F0.wireOp",EDGE,"E73.sketch_text.stroke-57"),sQuery(id+"F0.wireOp",EDGE,"E73.sketch_text.stroke-58"),sQuery(id+"F0.wireOp",EDGE,"E73.sketch_text.stroke-59"),sQuery(id+"F0.wireOp",EDGE,"E73.sketch_text.stroke-60"),sQuery(id+"F0.wireOp",EDGE,"E73.sketch_text.stroke-61"),sQuery(id+"F0.wireOp",EDGE,"E73.sketch_text.stroke-62"),sQuery(id+"F0.wireOp",EDGE,"E73.sketch_text.stroke-63"),sQuery(id+"F0.wireOp",EDGE,"E73.sketch_text.stroke-64"),sQuery(id+"F0.wireOp",EDGE,"E73.sketch_text.stroke-65"),sQuery(id+"F0.wireOp",EDGE,"E73.sketch_text.stroke-66"),sQuery(id+"F0.wireOp",EDGE,"E73.sketch_text.stroke-67"),sQuery(id+"F0.wireOp",EDGE,"E73.sketch_text.stroke-68"),sQuery(id+"F0.wireOp",EDGE,"E73.sketch_text.stroke-69"),sQuery(id+"F0.wireOp",EDGE,"E73.sketch_text.stroke-70"),sQuery(id+"F0.wireOp",EDGE,"E73.sketch_text.stroke-71"),sQuery(id+"F0.wireOp",EDGE,"E73.sketch_text.stroke-72"),sQuery(id+"F0.wireOp",EDGE,"E73.sketch_text.stroke-73"),sQuery(id+"F0.wireOp",EDGE,"E73.sketch_text.stroke-74"),sQuery(id+"F0.wireOp",EDGE,"E73.sketch_text.stroke-75"),sQuery(id+"F0.wireOp",EDGE,"E73.sketch_text.stroke-76"),sQuery(id+"F0.wireOp",EDGE,"E73.sketch_text.stroke-77"),sQuery(id+"F0.wireOp",EDGE,"E73.sketch_text.stroke-78"),sQuery(id+"F0.wireOp",EDGE,"E76.sketch_text.stroke-0"),sQuery(id+"F0.wireOp",EDGE,"E76.sketch_text.stroke-1"),sQuery(id+"F0.wireOp",EDGE,"E76.sketch_text.stroke-2"),sQuery(id+"F0.wireOp",EDGE,"E76.sketch_text.stroke-3"),sQuery(id+"F0.wireOp",EDGE,"E76.sketch_text.stroke-4"),sQuery(id+"F0.wireOp",EDGE,"E76.sketch_text.stroke-5"),sQuery(id+"F0.wireOp",EDGE,"E76.sketch_text.stroke-6"),sQuery(id+"F0.wireOp",EDGE,"E76.sketch_text.stroke-7"),sQuery(id+"F0.wireOp",EDGE,"E76.sketch_text.stroke-8"),sQuery(id+"F0.wireOp",EDGE,"E76.sketch_text.stroke-9"),sQuery(id+"F0.wireOp",EDGE,"E76.sketch_text.stroke-10"),sQuery(id+"F0.wireOp",EDGE,"E76.sketch_text.stroke-11"),sQuery(id+"F0.wireOp",EDGE,"E76.sketch_text.stroke-12"),sQuery(id+"F0.wireOp",EDGE,"E76.sketch_text.stroke-13"),sQuery(id+"F0.wireOp",EDGE,"E76.sketch_text.stroke-14"),sQuery(id+"F0.wireOp",EDGE,"E76.sketch_text.stroke-23"),sQuery(id+"F0.wireOp",EDGE,"E76.sketch_text.stroke-24"),sQuery(id+"F0.wireOp",EDGE,"E76.sketch_text.stroke-25"),sQuery(id+"F0.wireOp",EDGE,"E76.sketch_text.stroke-26"),sQuery(id+"F0.wireOp",EDGE,"E76.sketch_text.stroke-27"),sQuery(id+"F0.wireOp",EDGE,"E76.sketch_text.stroke-28"),sQuery(id+"F0.wireOp",EDGE,"E76.sketch_text.stroke-29"),sQuery(id+"F0.wireOp",EDGE,"E76.sketch_text.stroke-30"),sQuery(id+"F0.wireOp",EDGE,"E76.sketch_text.stroke-31"),sQuery(id+"F0.wireOp",EDGE,"E76.sketch_text.stroke-32"),sQuery(id+"F0.wireOp",EDGE,"E76.sketch_text.stroke-33"),sQuery(id+"F0.wireOp",EDGE,"E76.sketch_text.stroke-34"),sQuery(id+"F0.wireOp",EDGE,"E76.sketch_text.stroke-35"),sQuery(id+"F0.wireOp",EDGE,"E76.sketch_text.stroke-36"),sQuery(id+"F0.wireOp",EDGE,"E76.sketch_text.stroke-37"),sQuery(id+"F0.wireOp",EDGE,"E76.sketch_text.stroke-38"),sQuery(id+"F0.wireOp",EDGE,"E76.sketch_text.stroke-39"),sQuery(id+"F0.wireOp",EDGE,"E76.sketch_text.stroke-40"),sQuery(id+"F0.wireOp",EDGE,"E76.sketch_text.stroke-41"),sQuery(id+"F0.wireOp",EDGE,"E76.sketch_text.stroke-42"),sQuery(id+"F0.wireOp",EDGE,"E76.sketch_text.stroke-43"),sQuery(id+"F0.wireOp",EDGE,"E76.sketch_text.stroke-44"),sQuery(id+"F0.wireOp",EDGE,"E76.sketch_text.stroke-45"),sQuery(id+"F0.wireOp",EDGE,"E76.sketch_text.stroke-46"),sQuery(id+"F0.wireOp",EDGE,"E76.sketch_text.stroke-47"),sQuery(id+"F0.wireOp",EDGE,"E76.sketch_text.stroke-48"),sQuery(id+"F0.wireOp",EDGE,"E76.sketch_text.stroke-49"),sQuery(id+"F0.wireOp",EDGE,"E76.sketch_text.stroke-50"),sQuery(id+"F0.wireOp",EDGE,"E76.sketch_text.stroke-51"),sQuery(id+"F0.wireOp",EDGE,"E76.sketch_text.stroke-52"),sQuery(id+"F0.wireOp",EDGE,"E76.sketch_text.stroke-53"),sQuery(id+"F0.wireOp",EDGE,"E76.sketch_text.stroke-54"),sQuery(id+"F0.wireOp",EDGE,"E76.sketch_text.stroke-55"),sQuery(id+"F0.wireOp",EDGE,"E76.sketch_text.stroke-56"),sQuery(id+"F0.wireOp",EDGE,"E76.sketch_text.stroke-57"),sQuery(id+"F0.wireOp",EDGE,"E76.sketch_text.stroke-58"),sQuery(id+"F0.wireOp",EDGE,"E76.sketch_text.stroke-59"),sQuery(id+"F0.wireOp",EDGE,"E76.sketch_text.stroke-60"),sQuery(id+"F0.wireOp",EDGE,"E76.sketch_text.stroke-61"),sQuery(id+"F0.wireOp",EDGE,"E76.sketch_text.stroke-62"),sQuery(id+"F0.wireOp",EDGE,"E76.sketch_text.stroke-63"),sQuery(id+"F0.wireOp",EDGE,"E76.sketch_text.stroke-64"),sQuery(id+"F0.wireOp",EDGE,"E76.sketch_text.stroke-65"),sQuery(id+"F0.wireOp",EDGE,"E76.sketch_text.stroke-66"),sQuery(id+"F0.wireOp",EDGE,"E76.sketch_text.stroke-67"),sQuery(id+"F0.wireOp",EDGE,"E76.sketch_text.stroke-68"),sQuery(id+"F0.wireOp",EDGE,"E76.sketch_text.stroke-69"),sQuery(id+"F0.wireOp",EDGE,"E76.sketch_text.stroke-70"),sQuery(id+"F0.wireOp",EDGE,"E76.sketch_text.stroke-71"),sQuery(id+"F0.wireOp",EDGE,"E76.sketch_text.stroke-72"),sQuery(id+"F0.wireOp",EDGE,"E76.sketch_text.stroke-73"),sQuery(id+"F0.wireOp",EDGE,"E76.sketch_text.stroke-74"),sQuery(id+"F0.wireOp",EDGE,"E76.sketch_text.stroke-84"),sQuery(id+"F0.wireOp",EDGE,"E76.sketch_text.stroke-85"),sQuery(id+"F0.wireOp",EDGE,"E76.sketch_text.stroke-86"),sQuery(id+"F0.wireOp",EDGE,"E76.sketch_text.stroke-87"),sQuery(id+"F0.wireOp",EDGE,"E76.sketch_text.stroke-88"),sQuery(id+"F0.wireOp",EDGE,"E76.sketch_text.stroke-89"),sQuery(id+"F0.wireOp",EDGE,"E76.sketch_text.stroke-90"),sQuery(id+"F0.wireOp",EDGE,"E76.sketch_text.stroke-91"),sQuery(id+"F0.wireOp",EDGE,"E76.sketch_text.stroke-92"),sQuery(id+"F0.wireOp",EDGE,"E76.sketch_text.stroke-93"),sQuery(id+"F0.wireOp",EDGE,"E76.sketch_text.stroke-94"),sQuery(id+"F0.wireOp",EDGE,"E76.sketch_text.stroke-95"),sQuery(id+"F0.wireOp",EDGE,"E76.sketch_text.stroke-96"),sQuery(id+"F0.wireOp",EDGE,"E76.sketch_text.stroke-97"),sQuery(id+"F0.wireOp",EDGE,"E76.sketch_text.stroke-98"),sQuery(id+"F0.wireOp",EDGE,"E76.sketch_text.stroke-99"),sQuery(id+"F0.wireOp",EDGE,"E76.sketch_text.stroke-100"),sQuery(id+"F0.wireOp",EDGE,"E76.sketch_text.stroke-101"),sQuery(id+"F0.wireOp",EDGE,"E76.sketch_text.stroke-102"),sQuery(id+"F0.wireOp",EDGE,"E76.sketch_text.stroke-103"),sQuery(id+"F0.wireOp",EDGE,"E76.sketch_text.stroke-104"),sQuery(id+"F0.wireOp",EDGE,"E76.sketch_text.stroke-105"),sQuery(id+"F0.wireOp",EDGE,"E76.sketch_text.stroke-106"),sQuery(id+"F0.wireOp",EDGE,"E76.sketch_text.stroke-107"),sQuery(id+"F0.wireOp",EDGE,"E76.sketch_text.stroke-108"),sQuery(id+"F0.wireOp",EDGE,"E76.sketch_text.stroke-109"),sQuery(id+"F0.wireOp",EDGE,"E76.sketch_text.stroke-115"),sQuery(id+"F0.wireOp",EDGE,"E76.sketch_text.stroke-116"),sQuery(id+"F0.wireOp",EDGE,"E76.sketch_text.stroke-117"),sQuery(id+"F0.wireOp",EDGE,"E76.sketch_text.stroke-118"),sQuery(id+"F0.wireOp",EDGE,"E76.sketch_text.stroke-119"),sQuery(id+"F0.wireOp",EDGE,"E76.sketch_text.stroke-120"),sQuery(id+"F0.wireOp",EDGE,"E76.sketch_text.stroke-121"),sQuery(id+"F0.wireOp",EDGE,"E76.sketch_text.stroke-122"),sQuery(id+"F0.wireOp",EDGE,"E76.sketch_text.stroke-123"),sQuery(id+"F0.wireOp",EDGE,"E76.sketch_text.stroke-124"),sQuery(id+"F0.wireOp",EDGE,"E76.sketch_text.stroke-125"),sQuery(id+"F0.wireOp",EDGE,"E76.sketch_text.stroke-126"),sQuery(id+"F0.wireOp",EDGE,"E76.sketch_text.stroke-127"),sQuery(id+"F0.wireOp",EDGE,"E76.sketch_text.stroke-128"),sQuery(id+"F0.wireOp",EDGE,"E76.sketch_text.stroke-129"),sQuery(id+"F0.wireOp",EDGE,"E79.sketch_text.stroke-0"),sQuery(id+"F0.wireOp",EDGE,"E79.sketch_text.stroke-1"),sQuery(id+"F0.wireOp",EDGE,"E79.sketch_text.stroke-2"),sQuery(id+"F0.wireOp",EDGE,"E79.sketch_text.stroke-3"),sQuery(id+"F0.wireOp",EDGE,"E79.sketch_text.stroke-4"),sQuery(id+"F0.wireOp",EDGE,"E79.sketch_text.stroke-5"),sQuery(id+"F0.wireOp",EDGE,"E79.sketch_text.stroke-6"),sQuery(id+"F0.wireOp",EDGE,"E79.sketch_text.stroke-7"),sQuery(id+"F0.wireOp",EDGE,"E79.sketch_text.stroke-8"),sQuery(id+"F0.wireOp",EDGE,"E79.sketch_text.stroke-9"),sQuery(id+"F0.wireOp",EDGE,"E79.sketch_text.stroke-10"),sQuery(id+"F0.wireOp",EDGE,"E79.sketch_text.stroke-11"),sQuery(id+"F0.wireOp",EDGE,"E79.sketch_text.stroke-12"),sQuery(id+"F0.wireOp",EDGE,"E79.sketch_text.stroke-13"),sQuery(id+"F0.wireOp",EDGE,"E79.sketch_text.stroke-14"),sQuery(id+"F0.wireOp",EDGE,"E79.sketch_text.stroke-15"),sQuery(id+"F0.wireOp",EDGE,"E79.sketch_text.stroke-16"),sQuery(id+"F0.wireOp",EDGE,"E79.sketch_text.stroke-17"),sQuery(id+"F0.wireOp",EDGE,"E79.sketch_text.stroke-18"),sQuery(id+"F0.wireOp",EDGE,"E79.sketch_text.stroke-19"),sQuery(id+"F0.wireOp",EDGE,"E79.sketch_text.stroke-20"),sQuery(id+"F0.wireOp",EDGE,"E79.sketch_text.stroke-21"),sQuery(id+"F0.wireOp",EDGE,"E79.sketch_text.stroke-22"),sQuery(id+"F0.wireOp",EDGE,"E79.sketch_text.stroke-23"),sQuery(id+"F0.wireOp",EDGE,"E79.sketch_text.stroke-24"),sQuery(id+"F0.wireOp",EDGE,"E79.sketch_text.stroke-25"),sQuery(id+"F0.wireOp",EDGE,"E79.sketch_text.stroke-26"),sQuery(id+"F0.wireOp",EDGE,"E79.sketch_text.stroke-27"),sQuery(id+"F0.wireOp",EDGE,"E79.sketch_text.stroke-28"),sQuery(id+"F0.wireOp",EDGE,"E79.sketch_text.stroke-29"),sQuery(id+"F0.wireOp",EDGE,"E79.sketch_text.stroke-30"),sQuery(id+"F0.wireOp",EDGE,"E79.sketch_text.stroke-31"),sQuery(id+"F0.wireOp",EDGE,"E79.sketch_text.stroke-32"),sQuery(id+"F0.wireOp",EDGE,"E79.sketch_text.stroke-33"),sQuery(id+"F0.wireOp",EDGE,"E79.sketch_text.stroke-34"),sQuery(id+"F0.wireOp",EDGE,"E79.sketch_text.stroke-35"),sQuery(id+"F0.wireOp",EDGE,"E79.sketch_text.stroke-44"),sQuery(id+"F0.wireOp",EDGE,"E79.sketch_text.stroke-45"),sQuery(id+"F0.wireOp",EDGE,"E79.sketch_text.stroke-46"),sQuery(id+"F0.wireOp",EDGE,"E79.sketch_text.stroke-47"),sQuery(id+"F0.wireOp",EDGE,"E79.sketch_text.stroke-48"),sQuery(id+"F0.wireOp",EDGE,"E79.sketch_text.stroke-49"),sQuery(id+"F0.wireOp",EDGE,"E79.sketch_text.stroke-50"),sQuery(id+"F0.wireOp",EDGE,"E79.sketch_text.stroke-51"),sQuery(id+"F0.wireOp",EDGE,"E79.sketch_text.stroke-52"),sQuery(id+"F0.wireOp",EDGE,"E79.sketch_text.stroke-53"),sQuery(id+"F0.wireOp",EDGE,"E79.sketch_text.stroke-54"),sQuery(id+"F0.wireOp",EDGE,"E79.sketch_text.stroke-55"),sQuery(id+"F0.wireOp",EDGE,"E79.sketch_text.stroke-56"),sQuery(id+"F0.wireOp",EDGE,"E79.sketch_text.stroke-57"),sQuery(id+"F0.wireOp",EDGE,"E79.sketch_text.stroke-58"),sQuery(id+"F0.wireOp",EDGE,"E79.sketch_text.stroke-59"),sQuery(id+"F0.wireOp",EDGE,"E79.sketch_text.stroke-60"),sQuery(id+"F0.wireOp",EDGE,"E79.sketch_text.stroke-61"),sQuery(id+"F0.wireOp",EDGE,"E79.sketch_text.stroke-62"),sQuery(id+"F0.wireOp",EDGE,"E79.sketch_text.stroke-63"),sQuery(id+"F0.wireOp",EDGE,"E79.sketch_text.stroke-64"),sQuery(id+"F0.wireOp",EDGE,"E79.sketch_text.stroke-65"),sQuery(id+"F0.wireOp",EDGE,"E79.sketch_text.stroke-66"),sQuery(id+"F0.wireOp",EDGE,"E79.sketch_text.stroke-67"),sQuery(id+"F0.wireOp",EDGE,"E79.sketch_text.stroke-68"),sQuery(id+"F0.wireOp",EDGE,"E79.sketch_text.stroke-69"),sQuery(id+"F0.wireOp",EDGE,"E79.sketch_text.stroke-70"),sQuery(id+"F0.wireOp",EDGE,"E79.sketch_text.stroke-71"),sQuery(id+"F0.wireOp",EDGE,"E79.sketch_text.stroke-72"),sQuery(id+"F0.wireOp",EDGE,"E79.sketch_text.stroke-73"),sQuery(id+"F0.wireOp",EDGE,"E79.sketch_text.stroke-74"),sQuery(id+"F0.wireOp",EDGE,"E79.sketch_text.stroke-75"),sQuery(id+"F0.wireOp",EDGE,"E79.sketch_text.stroke-76"),sQuery(id+"F0.wireOp",EDGE,"E79.sketch_text.stroke-77"),sQuery(id+"F0.wireOp",EDGE,"E79.sketch_text.stroke-78"),sQuery(id+"F0.wireOp",EDGE,"E83"),sQuery(id+"F0.wireOp",EDGE,"E84"),sQuery(id+"F0.wireOp",EDGE,"E87"),sQuery(id+"F0.wireOp",EDGE,"E88"),sQuery(id+"F0.wireOp",EDGE,"E89"),sQuery(id+"F0.wireOp",EDGE,"E91"),sQuery(id+"F0.wireOp",EDGE,"E92"),sQuery(id+"F0.wireOp",EDGE,"ed6ad51a-24f1-4634-a6e9-502759cafa60.sketch_text.stroke-7"),sQuery(id+"F0.wireOp",EDGE,"ed6ad51a-24f1-4634-a6e9-502759cafa60.sketch_text.stroke-8"),sQuery(id+"F0.wireOp",EDGE,"ed6ad51a-24f1-4634-a6e9-502759cafa60.sketch_text.stroke-9"),sQuery(id+"F0.wireOp",EDGE,"ed6ad51a-24f1-4634-a6e9-502759cafa60.sketch_text.stroke-10"),sQuery(id+"F0.wireOp",EDGE,"ed6ad51a-24f1-4634-a6e9-502759cafa60.sketch_text.stroke-11"),sQuery(id+"F0.wireOp",EDGE,"ed6ad51a-24f1-4634-a6e9-502759cafa60.sketch_text.stroke-12"),sQuery(id+"F0.wireOp",EDGE,"ed6ad51a-24f1-4634-a6e9-502759cafa60.sketch_text.stroke-13"),sQuery(id+"F0.wireOp",EDGE,"ed6ad51a-24f1-4634-a6e9-502759cafa60.sketch_text.stroke-14"),sQuery(id+"F0.wireOp",EDGE,"ed6ad51a-24f1-4634-a6e9-502759cafa60.sketch_text.stroke-15"),sQuery(id+"F0.wireOp",EDGE,"ed6ad51a-24f1-4634-a6e9-502759cafa60.sketch_text.stroke-24"),sQuery(id+"F0.wireOp",EDGE,"ed6ad51a-24f1-4634-a6e9-502759cafa60.sketch_text.stroke-25"),sQuery(id+"F0.wireOp",EDGE,"ed6ad51a-24f1-4634-a6e9-502759cafa60.sketch_text.stroke-26"),sQuery(id+"F0.wireOp",EDGE,"ed6ad51a-24f1-4634-a6e9-502759cafa60.sketch_text.stroke-27"),sQuery(id+"F0.wireOp",EDGE,"ed6ad51a-24f1-4634-a6e9-502759cafa60.sketch_text.stroke-28"),sQuery(id+"F0.wireOp",EDGE,"ed6ad51a-24f1-4634-a6e9-502759cafa60.sketch_text.stroke-29"),sQuery(id+"F0.wireOp",EDGE,"ed6ad51a-24f1-4634-a6e9-502759cafa60.sketch_text.stroke-30"),sQuery(id+"F0.wireOp",EDGE,"ed6ad51a-24f1-4634-a6e9-502759cafa60.sketch_text.stroke-31"),sQuery(id+"F0.wireOp",EDGE,"ed6ad51a-24f1-4634-a6e9-502759cafa60.sketch_text.stroke-32"),sQuery(id+"F0.wireOp",EDGE,"ed6ad51a-24f1-4634-a6e9-502759cafa60.sketch_text.stroke-33"),sQuery(id+"F0.wireOp",EDGE,"ed6ad51a-24f1-4634-a6e9-502759cafa60.sketch_text.stroke-34"),sQuery(id+"F0.wireOp",EDGE,"ed6ad51a-24f1-4634-a6e9-502759cafa60.sketch_text.stroke-35"),sQuery(id+"F0.wireOp",EDGE,"ed6ad51a-24f1-4634-a6e9-502759cafa60.sketch_text.stroke-36"),sQuery(id+"F0.wireOp",EDGE,"ed6ad51a-24f1-4634-a6e9-502759cafa60.sketch_text.stroke-37"),sQuery(id+"F0.wireOp",EDGE,"ed6ad51a-24f1-4634-a6e9-502759cafa60.sketch_text.stroke-38"),sQuery(id+"F0.wireOp",EDGE,"ed6ad51a-24f1-4634-a6e9-502759cafa60.sketch_text.stroke-39"),sQuery(id+"F0.wireOp",EDGE,"ed6ad51a-24f1-4634-a6e9-502759cafa60.sketch_text.stroke-40"),sQuery(id+"F0.wireOp",EDGE,"ed6ad51a-24f1-4634-a6e9-502759cafa60.sketch_text.stroke-41"),sQuery(id+"F0.wireOp",EDGE,"ed6ad51a-24f1-4634-a6e9-502759cafa60.sketch_text.stroke-42"),sQuery(id+"F0.wireOp",EDGE,"ed6ad51a-24f1-4634-a6e9-502759cafa60.sketch_text.stroke-43"),sQuery(id+"F0.wireOp",EDGE,"ed6ad51a-24f1-4634-a6e9-502759cafa60.sketch_text.stroke-44"),sQuery(id+"F0.wireOp",EDGE,"ed6ad51a-24f1-4634-a6e9-502759cafa60.sketch_text.stroke-45"),sQuery(id+"F0.wireOp",EDGE,"ed6ad51a-24f1-4634-a6e9-502759cafa60.sketch_text.stroke-46"),sQuery(id+"F0.wireOp",EDGE,"ed6ad51a-24f1-4634-a6e9-502759cafa60.sketch_text.stroke-47"),sQuery(id+"F0.wireOp",EDGE,"ed6ad51a-24f1-4634-a6e9-502759cafa60.sketch_text.stroke-48"),sQuery(id+"F0.wireOp",EDGE,"ed6ad51a-24f1-4634-a6e9-502759cafa60.sketch_text.stroke-49"),sQuery(id+"F0.wireOp",EDGE,"ed6ad51a-24f1-4634-a6e9-502759cafa60.sketch_text.stroke-50"),sQuery(id+"F0.wireOp",EDGE,"ed6ad51a-24f1-4634-a6e9-502759cafa60.sketch_text.stroke-51"),sQuery(id+"F0.wireOp",EDGE,"ed6ad51a-24f1-4634-a6e9-502759cafa60.sketch_text.stroke-52"),sQuery(id+"F0.wireOp",EDGE,"ed6ad51a-24f1-4634-a6e9-502759cafa60.sketch_text.stroke-53"),sQuery(id+"F0.wireOp",EDGE,"ed6ad51a-24f1-4634-a6e9-502759cafa60.sketch_text.stroke-54"),sQuery(id+"F0.wireOp",EDGE,"ed6ad51a-24f1-4634-a6e9-502759cafa60.sketch_text.stroke-55"),sQuery(id+"F0.wireOp",EDGE,"ed6ad51a-24f1-4634-a6e9-502759cafa60.sketch_text.stroke-56"),sQuery(id+"F0.wireOp",EDGE,"ed6ad51a-24f1-4634-a6e9-502759cafa60.sketch_text.stroke-57"),sQuery(id+"F0.wireOp",EDGE,"ed6ad51a-24f1-4634-a6e9-502759cafa60.sketch_text.stroke-58"),sQuery(id+"F0.wireOp",EDGE,"ed6ad51a-24f1-4634-a6e9-502759cafa60.sketch_text.stroke-59"),sQuery(id+"F0.wireOp",EDGE,"ed6ad51a-24f1-4634-a6e9-502759cafa60.sketch_text.stroke-65"),sQuery(id+"F0.wireOp",EDGE,"ed6ad51a-24f1-4634-a6e9-502759cafa60.sketch_text.stroke-66"),sQuery(id+"F0.wireOp",EDGE,"ed6ad51a-24f1-4634-a6e9-502759cafa60.sketch_text.stroke-67"),sQuery(id+"F0.wireOp",EDGE,"ed6ad51a-24f1-4634-a6e9-502759cafa60.sketch_text.stroke-68"),sQuery(id+"F0.wireOp",EDGE,"ed6ad51a-24f1-4634-a6e9-502759cafa60.sketch_text.stroke-69"),sQuery(id+"F0.wireOp",EDGE,"ed6ad51a-24f1-4634-a6e9-502759cafa60.sketch_text.stroke-70"),sQuery(id+"F0.wireOp",EDGE,"ed6ad51a-24f1-4634-a6e9-502759cafa60.sketch_text.stroke-71"),sQuery(id+"F0.wireOp",EDGE,"ed6ad51a-24f1-4634-a6e9-502759cafa60.sketch_text.stroke-72"),sQuery(id+"F0.wireOp",EDGE,"ed6ad51a-24f1-4634-a6e9-502759cafa60.sketch_text.stroke-73"),sQuery(id+"F0.wireOp",EDGE,"ed6ad51a-24f1-4634-a6e9-502759cafa60.sketch_text.stroke-74"),sQuery(id+"F0.wireOp",EDGE,"ed6ad51a-24f1-4634-a6e9-502759cafa60.sketch_text.stroke-75"),sQuery(id+"F0.wireOp",EDGE,"ed6ad51a-24f1-4634-a6e9-502759cafa60.sketch_text.stroke-76"),sQuery(id+"F0.wireOp",EDGE,"ed6ad51a-24f1-4634-a6e9-502759cafa60.sketch_text.stroke-77"),sQuery(id+"F0.wireOp",EDGE,"ed6ad51a-24f1-4634-a6e9-502759cafa60.sketch_text.stroke-78"),sQuery(id+"F0.wireOp",EDGE,"ed6ad51a-24f1-4634-a6e9-502759cafa60.sketch_text.stroke-79"),sQuery(id+"F0.wireOp",EDGE,"ed6ad51a-24f1-4634-a6e9-502759cafa60.sketch_text.stroke-80"),sQuery(id+"F0.wireOp",EDGE,"ed6ad51a-24f1-4634-a6e9-502759cafa60.sketch_text.stroke-81"),sQuery(id+"F0.wireOp",EDGE,"ed6ad51a-24f1-4634-a6e9-502759cafa60.sketch_text.stroke-82"),sQuery(id+"F0.wireOp",EDGE,"ed6ad51a-24f1-4634-a6e9-502759cafa60.sketch_text.stroke-83"),sQuery(id+"F0.wireOp",EDGE,"ed6ad51a-24f1-4634-a6e9-502759cafa60.sketch_text.stroke-84"),sQuery(id+"F0.wireOp",EDGE,"ed6ad51a-24f1-4634-a6e9-502759cafa60.sketch_text.stroke-85"),sQuery(id+"F0.wireOp",EDGE,"ed6ad51a-24f1-4634-a6e9-502759cafa60.sketch_text.stroke-86"),sQuery(id+"F0.wireOp",EDGE,"ed6ad51a-24f1-4634-a6e9-502759cafa60.sketch_text.stroke-87"),sQuery(id+"F0.wireOp",EDGE,"ed6ad51a-24f1-4634-a6e9-502759cafa60.sketch_text.stroke-88"),sQuery(id+"F0.wireOp",EDGE,"ed6ad51a-24f1-4634-a6e9-502759cafa60.sketch_text.stroke-89"),sQuery(id+"F0.wireOp",EDGE,"ed6ad51a-24f1-4634-a6e9-502759cafa60.sketch_text.stroke-90"),sQuery(id+"F0.wireOp",EDGE,"ed6ad51a-24f1-4634-a6e9-502759cafa60.sketch_text.stroke-91"),sQuery(id+"F0.wireOp",EDGE,"ed6ad51a-24f1-4634-a6e9-502759cafa60.sketch_text.stroke-92"),sQuery(id+"F0.wireOp",EDGE,"E97.sketch_text.stroke-0"),sQuery(id+"F0.wireOp",EDGE,"E97.sketch_text.stroke-1"),sQuery(id+"F0.wireOp",EDGE,"E97.sketch_text.stroke-2"),sQuery(id+"F0.wireOp",EDGE,"E97.sketch_text.stroke-3"),sQuery(id+"F0.wireOp",EDGE,"E97.sketch_text.stroke-4"),sQuery(id+"F0.wireOp",EDGE,"E97.sketch_text.stroke-5"),sQuery(id+"F0.wireOp",EDGE,"E97.sketch_text.stroke-6"),sQuery(id+"F0.wireOp",EDGE,"E97.sketch_text.stroke-7"),sQuery(id+"F0.wireOp",EDGE,"E97.sketch_text.stroke-14"),sQuery(id+"F0.wireOp",EDGE,"E97.sketch_text.stroke-15"),sQuery(id+"F0.wireOp",EDGE,"E97.sketch_text.stroke-16"),sQuery(id+"F0.wireOp",EDGE,"E97.sketch_text.stroke-17"),sQuery(id+"F0.wireOp",EDGE,"E97.sketch_text.stroke-18"),sQuery(id+"F0.wireOp",EDGE,"E97.sketch_text.stroke-19"),sQuery(id+"F0.wireOp",EDGE,"E97.sketch_text.stroke-20"),sQuery(id+"F0.wireOp",EDGE,"E97.sketch_text.stroke-21"),sQuery(id+"F0.wireOp",EDGE,"E97.sketch_text.stroke-22"),sQuery(id+"F0.wireOp",EDGE,"E97.sketch_text.stroke-23"),sQuery(id+"F0.wireOp",EDGE,"E97.sketch_text.stroke-24"),sQuery(id+"F0.wireOp",EDGE,"E97.sketch_text.stroke-25"),sQuery(id+"F0.wireOp",EDGE,"E97.sketch_text.stroke-26"),sQuery(id+"F0.wireOp",EDGE,"E97.sketch_text.stroke-27"),sQuery(id+"F0.wireOp",EDGE,"E97.sketch_text.stroke-28"),sQuery(id+"F0.wireOp",EDGE,"E97.sketch_text.stroke-29"),sQuery(id+"F0.wireOp",EDGE,"E97.sketch_text.stroke-30"),sQuery(id+"F0.wireOp",EDGE,"E97.sketch_text.stroke-31"),sQuery(id+"F0.wireOp",EDGE,"E97.sketch_text.stroke-32"),sQuery(id+"F0.wireOp",EDGE,"E97.sketch_text.stroke-33"),sQuery(id+"F0.wireOp",EDGE,"E97.sketch_text.stroke-34"),sQuery(id+"F0.wireOp",EDGE,"E97.sketch_text.stroke-35"),sQuery(id+"F0.wireOp",EDGE,"E97.sketch_text.stroke-36"),sQuery(id+"F0.wireOp",EDGE,"E97.sketch_text.stroke-37"),sQuery(id+"F0.wireOp",EDGE,"E97.sketch_text.stroke-38"),sQuery(id+"F0.wireOp",EDGE,"E97.sketch_text.stroke-39"),sQuery(id+"F0.wireOp",EDGE,"E97.sketch_text.stroke-40"),sQuery(id+"F0.wireOp",EDGE,"E97.sketch_text.stroke-41"),sQuery(id+"F0.wireOp",EDGE,"E97.sketch_text.stroke-42"),sQuery(id+"F0.wireOp",EDGE,"E97.sketch_text.stroke-43"),sQuery(id+"F0.wireOp",EDGE,"E97.sketch_text.stroke-44"),sQuery(id+"F0.wireOp",EDGE,"E97.sketch_text.stroke-45"),sQuery(id+"F0.wireOp",EDGE,"E97.sketch_text.stroke-46"),sQuery(id+"F0.wireOp",EDGE,"E97.sketch_text.stroke-47"),sQuery(id+"F0.wireOp",EDGE,"E97.sketch_text.stroke-48"),sQuery(id+"F0.wireOp",EDGE,"E97.sketch_text.stroke-49"),sQuery(id+"F0.wireOp",EDGE,"E97.sketch_text.stroke-50"),sQuery(id+"F0.wireOp",EDGE,"E97.sketch_text.stroke-51"),sQuery(id+"F0.wireOp",EDGE,"E97.sketch_text.stroke-52"),sQuery(id+"F0.wireOp",EDGE,"E97.sketch_text.stroke-53"),sQuery(id+"F0.wireOp",EDGE,"E97.sketch_text.stroke-54"),sQuery(id+"F0.wireOp",EDGE,"E97.sketch_text.stroke-55"),sQuery(id+"F0.wireOp",EDGE,"E97.sketch_text.stroke-56"),sQuery(id+"F0.wireOp",EDGE,"E97.sketch_text.stroke-57"),sQuery(id+"F0.wireOp",EDGE,"E97.sketch_text.stroke-58"),sQuery(id+"F0.wireOp",EDGE,"E97.sketch_text.stroke-59"),sQuery(id+"F0.wireOp",EDGE,"E97.sketch_text.stroke-60"),sQuery(id+"F0.wireOp",EDGE,"E97.sketch_text.stroke-61"),sQuery(id+"F0.wireOp",EDGE,"E97.sketch_text.stroke-62"),sQuery(id+"F0.wireOp",EDGE,"E97.sketch_text.stroke-63"),sQuery(id+"F0.wireOp",EDGE,"E97.sketch_text.stroke-72"),sQuery(id+"F0.wireOp",EDGE,"E97.sketch_text.stroke-73"),sQuery(id+"F0.wireOp",EDGE,"E97.sketch_text.stroke-74"),sQuery(id+"F0.wireOp",EDGE,"E97.sketch_text.stroke-75"),sQuery(id+"F0.wireOp",EDGE,"E97.sketch_text.stroke-76"),sQuery(id+"F0.wireOp",EDGE,"E97.sketch_text.stroke-77"),sQuery(id+"F0.wireOp",EDGE,"E97.sketch_text.stroke-78"),sQuery(id+"F0.wireOp",EDGE,"E97.sketch_text.stroke-79"),sQuery(id+"F0.wireOp",EDGE,"E97.sketch_text.stroke-80"),sQuery(id+"F0.wireOp",EDGE,"E97.sketch_text.stroke-81"),sQuery(id+"F0.wireOp",EDGE,"E97.sketch_text.stroke-82"),sQuery(id+"F0.wireOp",EDGE,"E97.sketch_text.stroke-83"),sQuery(id+"F0.wireOp",EDGE,"E97.sketch_text.stroke-84"),sQuery(id+"F0.wireOp",EDGE,"E97.sketch_text.stroke-85"),sQuery(id+"F0.wireOp",EDGE,"E97.sketch_text.stroke-86"),sQuery(id+"F0.wireOp",EDGE,"E97.sketch_text.stroke-87"),sQuery(id+"F0.wireOp",EDGE,"E97.sketch_text.stroke-88"),sQuery(id+"F0.wireOp",EDGE,"E97.sketch_text.stroke-89"),sQuery(id+"F0.wireOp",EDGE,"E97.sketch_text.stroke-90"),sQuery(id+"F0.wireOp",EDGE,"E97.sketch_text.stroke-91"),sQuery(id+"F0.wireOp",EDGE,"E97.sketch_text.stroke-92"),sQuery(id+"F0.wireOp",EDGE,"E97.sketch_text.stroke-93"),sQuery(id+"F0.wireOp",EDGE,"E97.sketch_text.stroke-94"),sQuery(id+"F0.wireOp",EDGE,"E97.sketch_text.stroke-95"),sQuery(id+"F0.wireOp",EDGE,"E97.sketch_text.stroke-96"),sQuery(id+"F0.wireOp",EDGE,"E97.sketch_text.stroke-97"),sQuery(id+"F0.wireOp",EDGE,"E97.sketch_text.stroke-98"),sQuery(id+"F0.wireOp",EDGE,"E97.sketch_text.stroke-99"),sQuery(id+"F0.wireOp",EDGE,"E97.sketch_text.stroke-100"),sQuery(id+"F0.wireOp",EDGE,"E97.sketch_text.stroke-101"),sQuery(id+"F0.wireOp",EDGE,"E97.sketch_text.stroke-102"),sQuery(id+"F0.wireOp",EDGE,"E97.sketch_text.stroke-103"),sQuery(id+"F0.wireOp",EDGE,"E97.sketch_text.stroke-104"),sQuery(id+"F0.wireOp",EDGE,"E97.sketch_text.stroke-105"),sQuery(id+"F0.wireOp",EDGE,"E97.sketch_text.stroke-106"),sQuery(id+"F0.wireOp",EDGE,"E100.sketch_text.stroke-0"),sQuery(id+"F0.wireOp",EDGE,"E100.sketch_text.stroke-1"),sQuery(id+"F0.wireOp",EDGE,"E100.sketch_text.stroke-2"),sQuery(id+"F0.wireOp",EDGE,"E100.sketch_text.stroke-3"),sQuery(id+"F0.wireOp",EDGE,"E100.sketch_text.stroke-4"),sQuery(id+"F0.wireOp",EDGE,"E100.sketch_text.stroke-5"),sQuery(id+"F0.wireOp",EDGE,"E100.sketch_text.stroke-6"),sQuery(id+"F0.wireOp",EDGE,"E100.sketch_text.stroke-7"),sQuery(id+"F0.wireOp",EDGE,"E100.sketch_text.stroke-14"),sQuery(id+"F0.wireOp",EDGE,"E100.sketch_text.stroke-15"),sQuery(id+"F0.wireOp",EDGE,"E100.sketch_text.stroke-16"),sQuery(id+"F0.wireOp",EDGE,"E100.sketch_text.stroke-17"),sQuery(id+"F0.wireOp",EDGE,"E100.sketch_text.stroke-18"),sQuery(id+"F0.wireOp",EDGE,"E100.sketch_text.stroke-19"),sQuery(id+"F0.wireOp",EDGE,"E100.sketch_text.stroke-20"),sQuery(id+"F0.wireOp",EDGE,"E100.sketch_text.stroke-21"),sQuery(id+"F0.wireOp",EDGE,"E100.sketch_text.stroke-22"),sQuery(id+"F0.wireOp",EDGE,"E100.sketch_text.stroke-23"),sQuery(id+"F0.wireOp",EDGE,"E100.sketch_text.stroke-24"),sQuery(id+"F0.wireOp",EDGE,"E100.sketch_text.stroke-25"),sQuery(id+"F0.wireOp",EDGE,"E100.sketch_text.stroke-26"),sQuery(id+"F0.wireOp",EDGE,"E100.sketch_text.stroke-27"),sQuery(id+"F0.wireOp",EDGE,"E100.sketch_text.stroke-28"),sQuery(id+"F0.wireOp",EDGE,"E100.sketch_text.stroke-29"),sQuery(id+"F0.wireOp",EDGE,"E100.sketch_text.stroke-30"),sQuery(id+"F0.wireOp",EDGE,"E100.sketch_text.stroke-31"),sQuery(id+"F0.wireOp",EDGE,"E100.sketch_text.stroke-32"),sQuery(id+"F0.wireOp",EDGE,"E100.sketch_text.stroke-33"),sQuery(id+"F0.wireOp",EDGE,"E100.sketch_text.stroke-34"),sQuery(id+"F0.wireOp",EDGE,"E100.sketch_text.stroke-35"),sQuery(id+"F0.wireOp",EDGE,"E100.sketch_text.stroke-36"),sQuery(id+"F0.wireOp",EDGE,"E100.sketch_text.stroke-37"),sQuery(id+"F0.wireOp",EDGE,"E100.sketch_text.stroke-38"),sQuery(id+"F0.wireOp",EDGE,"E100.sketch_text.stroke-39"),sQuery(id+"F0.wireOp",EDGE,"E100.sketch_text.stroke-40"),sQuery(id+"F0.wireOp",EDGE,"E100.sketch_text.stroke-41"),sQuery(id+"F0.wireOp",EDGE,"E100.sketch_text.stroke-42"),sQuery(id+"F0.wireOp",EDGE,"E100.sketch_text.stroke-43"),sQuery(id+"F0.wireOp",EDGE,"E100.sketch_text.stroke-44"),sQuery(id+"F0.wireOp",EDGE,"E100.sketch_text.stroke-45"),sQuery(id+"F0.wireOp",EDGE,"E100.sketch_text.stroke-46"),sQuery(id+"F0.wireOp",EDGE,"E100.sketch_text.stroke-47"),sQuery(id+"F0.wireOp",EDGE,"E100.sketch_text.stroke-48"),sQuery(id+"F0.wireOp",EDGE,"E100.sketch_text.stroke-49"),sQuery(id+"F0.wireOp",EDGE,"E100.sketch_text.stroke-50"),sQuery(id+"F0.wireOp",EDGE,"E100.sketch_text.stroke-51"),sQuery(id+"F0.wireOp",EDGE,"E100.sketch_text.stroke-52"),sQuery(id+"F0.wireOp",EDGE,"E100.sketch_text.stroke-53"),sQuery(id+"F0.wireOp",EDGE,"E100.sketch_text.stroke-54"),sQuery(id+"F0.wireOp",EDGE,"E100.sketch_text.stroke-55"),sQuery(id+"F0.wireOp",EDGE,"E100.sketch_text.stroke-56"),sQuery(id+"F0.wireOp",EDGE,"E100.sketch_text.stroke-57"),sQuery(id+"F0.wireOp",EDGE,"E100.sketch_text.stroke-58"),sQuery(id+"F0.wireOp",EDGE,"E100.sketch_text.stroke-59"),sQuery(id+"F0.wireOp",EDGE,"E100.sketch_text.stroke-60"),sQuery(id+"F0.wireOp",EDGE,"E100.sketch_text.stroke-61"),sQuery(id+"F0.wireOp",EDGE,"E100.sketch_text.stroke-62"),sQuery(id+"F0.wireOp",EDGE,"E100.sketch_text.stroke-63"),sQuery(id+"F0.wireOp",EDGE,"E100.sketch_text.stroke-72"),sQuery(id+"F0.wireOp",EDGE,"E100.sketch_text.stroke-73"),sQuery(id+"F0.wireOp",EDGE,"E100.sketch_text.stroke-74"),sQuery(id+"F0.wireOp",EDGE,"E100.sketch_text.stroke-75"),sQuery(id+"F0.wireOp",EDGE,"E100.sketch_text.stroke-76"),sQuery(id+"F0.wireOp",EDGE,"E100.sketch_text.stroke-77"),sQuery(id+"F0.wireOp",EDGE,"E100.sketch_text.stroke-78"),sQuery(id+"F0.wireOp",EDGE,"E100.sketch_text.stroke-79"),sQuery(id+"F0.wireOp",EDGE,"E100.sketch_text.stroke-80"),sQuery(id+"F0.wireOp",EDGE,"E100.sketch_text.stroke-81"),sQuery(id+"F0.wireOp",EDGE,"E100.sketch_text.stroke-82"),sQuery(id+"F0.wireOp",EDGE,"E100.sketch_text.stroke-83"),sQuery(id+"F0.wireOp",EDGE,"E100.sketch_text.stroke-84"),sQuery(id+"F0.wireOp",EDGE,"E100.sketch_text.stroke-85"),sQuery(id+"F0.wireOp",EDGE,"E100.sketch_text.stroke-86"),sQuery(id+"F0.wireOp",EDGE,"E100.sketch_text.stroke-87"),sQuery(id+"F0.wireOp",EDGE,"E100.sketch_text.stroke-88"),sQuery(id+"F0.wireOp",EDGE,"E100.sketch_text.stroke-89"),sQuery(id+"F0.wireOp",EDGE,"E100.sketch_text.stroke-90"),sQuery(id+"F0.wireOp",EDGE,"E100.sketch_text.stroke-91"),sQuery(id+"F0.wireOp",EDGE,"E100.sketch_text.stroke-92"),sQuery(id+"F0.wireOp",EDGE,"E100.sketch_text.stroke-93"),sQuery(id+"F0.wireOp",EDGE,"E100.sketch_text.stroke-94"),sQuery(id+"F0.wireOp",EDGE,"E100.sketch_text.stroke-95"),sQuery(id+"F0.wireOp",EDGE,"E100.sketch_text.stroke-96"),sQuery(id+"F0.wireOp",EDGE,"E100.sketch_text.stroke-97"),sQuery(id+"F0.wireOp",EDGE,"E100.sketch_text.stroke-98"),sQuery(id+"F0.wireOp",EDGE,"E100.sketch_text.stroke-99"),sQuery(id+"F0.wireOp",EDGE,"E100.sketch_text.stroke-100"),sQuery(id+"F0.wireOp",EDGE,"E100.sketch_text.stroke-101"),sQuery(id+"F0.wireOp",EDGE,"E100.sketch_text.stroke-102"),sQuery(id+"F0.wireOp",EDGE,"E100.sketch_text.stroke-103"),sQuery(id+"F0.wireOp",EDGE,"E100.sketch_text.stroke-104"),sQuery(id+"F0.wireOp",EDGE,"E100.sketch_text.stroke-105"),sQuery(id+"F0.wireOp",EDGE,"E100.sketch_text.stroke-106"),sQuery(id+"F0.wireOp",EDGE,"E103.sketch_text.stroke-0"),sQuery(id+"F0.wireOp",EDGE,"E103.sketch_text.stroke-1"),sQuery(id+"F0.wireOp",EDGE,"E103.sketch_text.stroke-2"),sQuery(id+"F0.wireOp",EDGE,"E103.sketch_text.stroke-3"),sQuery(id+"F0.wireOp",EDGE,"E103.sketch_text.stroke-4"),sQuery(id+"F0.wireOp",EDGE,"E103.sketch_text.stroke-5"),sQuery(id+"F0.wireOp",EDGE,"E103.sketch_text.stroke-6"),sQuery(id+"F0.wireOp",EDGE,"E103.sketch_text.stroke-7"),sQuery(id+"F0.wireOp",EDGE,"E103.sketch_text.stroke-8"),sQuery(id+"F0.wireOp",EDGE,"E103.sketch_text.stroke-9"),sQuery(id+"F0.wireOp",EDGE,"E103.sketch_text.stroke-10"),sQuery(id+"F0.wireOp",EDGE,"E103.sketch_text.stroke-11"),sQuery(id+"F0.wireOp",EDGE,"E103.sketch_text.stroke-12"),sQuery(id+"F0.wireOp",EDGE,"E103.sketch_text.stroke-13"),sQuery(id+"F0.wireOp",EDGE,"E103.sketch_text.stroke-14"),sQuery(id+"F0.wireOp",EDGE,"E103.sketch_text.stroke-15"),sQuery(id+"F0.wireOp",EDGE,"E103.sketch_text.stroke-16"),sQuery(id+"F0.wireOp",EDGE,"E103.sketch_text.stroke-17"),sQuery(id+"F0.wireOp",EDGE,"E103.sketch_text.stroke-18"),sQuery(id+"F0.wireOp",EDGE,"E103.sketch_text.stroke-19"),sQuery(id+"F0.wireOp",EDGE,"E103.sketch_text.stroke-20"),sQuery(id+"F0.wireOp",EDGE,"E103.sketch_text.stroke-21"),sQuery(id+"F0.wireOp",EDGE,"E103.sketch_text.stroke-22"),sQuery(id+"F0.wireOp",EDGE,"E103.sketch_text.stroke-23"),sQuery(id+"F0.wireOp",EDGE,"E103.sketch_text.stroke-24"),sQuery(id+"F0.wireOp",EDGE,"E103.sketch_text.stroke-25"),sQuery(id+"F0.wireOp",EDGE,"E103.sketch_text.stroke-26"),sQuery(id+"F0.wireOp",EDGE,"E103.sketch_text.stroke-27"),sQuery(id+"F0.wireOp",EDGE,"E103.sketch_text.stroke-28"),sQuery(id+"F0.wireOp",EDGE,"E103.sketch_text.stroke-29"),sQuery(id+"F0.wireOp",EDGE,"E103.sketch_text.stroke-30"),sQuery(id+"F0.wireOp",EDGE,"E103.sketch_text.stroke-31"),sQuery(id+"F0.wireOp",EDGE,"E103.sketch_text.stroke-32"),sQuery(id+"F0.wireOp",EDGE,"E103.sketch_text.stroke-33"),sQuery(id+"F0.wireOp",EDGE,"E103.sketch_text.stroke-34"),sQuery(id+"F0.wireOp",EDGE,"E103.sketch_text.stroke-35"),sQuery(id+"F0.wireOp",EDGE,"E103.sketch_text.stroke-44"),sQuery(id+"F0.wireOp",EDGE,"E103.sketch_text.stroke-45"),sQuery(id+"F0.wireOp",EDGE,"E103.sketch_text.stroke-46"),sQuery(id+"F0.wireOp",EDGE,"E103.sketch_text.stroke-47"),sQuery(id+"F0.wireOp",EDGE,"E103.sketch_text.stroke-48"),sQuery(id+"F0.wireOp",EDGE,"E103.sketch_text.stroke-49"),sQuery(id+"F0.wireOp",EDGE,"E103.sketch_text.stroke-50"),sQuery(id+"F0.wireOp",EDGE,"E103.sketch_text.stroke-51"),sQuery(id+"F0.wireOp",EDGE,"E103.sketch_text.stroke-52"),sQuery(id+"F0.wireOp",EDGE,"E103.sketch_text.stroke-53"),sQuery(id+"F0.wireOp",EDGE,"E103.sketch_text.stroke-54"),sQuery(id+"F0.wireOp",EDGE,"E103.sketch_text.stroke-55"),sQuery(id+"F0.wireOp",EDGE,"E103.sketch_text.stroke-56"),sQuery(id+"F0.wireOp",EDGE,"E103.sketch_text.stroke-57"),sQuery(id+"F0.wireOp",EDGE,"E103.sketch_text.stroke-58"),sQuery(id+"F0.wireOp",EDGE,"E103.sketch_text.stroke-59"),sQuery(id+"F0.wireOp",EDGE,"E103.sketch_text.stroke-60"),sQuery(id+"F0.wireOp",EDGE,"E103.sketch_text.stroke-61"),sQuery(id+"F0.wireOp",EDGE,"E103.sketch_text.stroke-62"),sQuery(id+"F0.wireOp",EDGE,"E103.sketch_text.stroke-63"),sQuery(id+"F0.wireOp",EDGE,"E103.sketch_text.stroke-64"),sQuery(id+"F0.wireOp",EDGE,"E103.sketch_text.stroke-65"),sQuery(id+"F0.wireOp",EDGE,"E103.sketch_text.stroke-66"),sQuery(id+"F0.wireOp",EDGE,"E103.sketch_text.stroke-67"),sQuery(id+"F0.wireOp",EDGE,"E103.sketch_text.stroke-68"),sQuery(id+"F0.wireOp",EDGE,"E103.sketch_text.stroke-69"),sQuery(id+"F0.wireOp",EDGE,"E103.sketch_text.stroke-70"),sQuery(id+"F0.wireOp",EDGE,"E103.sketch_text.stroke-71"),sQuery(id+"F0.wireOp",EDGE,"E103.sketch_text.stroke-72"),sQuery(id+"F0.wireOp",EDGE,"E103.sketch_text.stroke-73"),sQuery(id+"F0.wireOp",EDGE,"E103.sketch_text.stroke-74"),sQuery(id+"F0.wireOp",EDGE,"E103.sketch_text.stroke-75"),sQuery(id+"F0.wireOp",EDGE,"E103.sketch_text.stroke-76"),sQuery(id+"F0.wireOp",EDGE,"E103.sketch_text.stroke-77"),sQuery(id+"F0.wireOp",EDGE,"E103.sketch_text.stroke-78"),sQuery(id+"F0.wireOp",EDGE,"E106.sketch_text.stroke-0"),sQuery(id+"F0.wireOp",EDGE,"E106.sketch_text.stroke-1"),sQuery(id+"F0.wireOp",EDGE,"E106.sketch_text.stroke-2"),sQuery(id+"F0.wireOp",EDGE,"E106.sketch_text.stroke-3"),sQuery(id+"F0.wireOp",EDGE,"E106.sketch_text.stroke-4"),sQuery(id+"F0.wireOp",EDGE,"E106.sketch_text.stroke-5"),sQuery(id+"F0.wireOp",EDGE,"E106.sketch_text.stroke-6"),sQuery(id+"F0.wireOp",EDGE,"E106.sketch_text.stroke-7"),sQuery(id+"F0.wireOp",EDGE,"E106.sketch_text.stroke-8"),sQuery(id+"F0.wireOp",EDGE,"E106.sketch_text.stroke-9"),sQuery(id+"F0.wireOp",EDGE,"E106.sketch_text.stroke-10"),sQuery(id+"F0.wireOp",EDGE,"E106.sketch_text.stroke-11"),sQuery(id+"F0.wireOp",EDGE,"E106.sketch_text.stroke-12"),sQuery(id+"F0.wireOp",EDGE,"E106.sketch_text.stroke-13"),sQuery(id+"F0.wireOp",EDGE,"E106.sketch_text.stroke-14"),sQuery(id+"F0.wireOp",EDGE,"E106.sketch_text.stroke-15"),sQuery(id+"F0.wireOp",EDGE,"E106.sketch_text.stroke-16"),sQuery(id+"F0.wireOp",EDGE,"E106.sketch_text.stroke-17"),sQuery(id+"F0.wireOp",EDGE,"E106.sketch_text.stroke-26"),sQuery(id+"F0.wireOp",EDGE,"E106.sketch_text.stroke-27"),sQuery(id+"F0.wireOp",EDGE,"E106.sketch_text.stroke-28"),sQuery(id+"F0.wireOp",EDGE,"E106.sketch_text.stroke-29"),sQuery(id+"F0.wireOp",EDGE,"E106.sketch_text.stroke-30"),sQuery(id+"F0.wireOp",EDGE,"E106.sketch_text.stroke-31"),sQuery(id+"F0.wireOp",EDGE,"E106.sketch_text.stroke-32"),sQuery(id+"F0.wireOp",EDGE,"E106.sketch_text.stroke-33"),sQuery(id+"F0.wireOp",EDGE,"E106.sketch_text.stroke-34"),sQuery(id+"F0.wireOp",EDGE,"E106.sketch_text.stroke-35"),sQuery(id+"F0.wireOp",EDGE,"E106.sketch_text.stroke-36"),sQuery(id+"F0.wireOp",EDGE,"E106.sketch_text.stroke-37"),sQuery(id+"F0.wireOp",EDGE,"E106.sketch_text.stroke-38"),sQuery(id+"F0.wireOp",EDGE,"E106.sketch_text.stroke-39"),sQuery(id+"F0.wireOp",EDGE,"E106.sketch_text.stroke-40"),sQuery(id+"F0.wireOp",EDGE,"E106.sketch_text.stroke-41"),sQuery(id+"F0.wireOp",EDGE,"E106.sketch_text.stroke-42"),sQuery(id+"F0.wireOp",EDGE,"E106.sketch_text.stroke-48"),sQuery(id+"F0.wireOp",EDGE,"E106.sketch_text.stroke-49"),sQuery(id+"F0.wireOp",EDGE,"E106.sketch_text.stroke-50"),sQuery(id+"F0.wireOp",EDGE,"E106.sketch_text.stroke-51"),sQuery(id+"F0.wireOp",EDGE,"E106.sketch_text.stroke-52"),sQuery(id+"F0.wireOp",EDGE,"E106.sketch_text.stroke-53"),sQuery(id+"F0.wireOp",EDGE,"E106.sketch_text.stroke-54"),sQuery(id+"F0.wireOp",EDGE,"E106.sketch_text.stroke-55"),sQuery(id+"F0.wireOp",EDGE,"E106.sketch_text.stroke-56"),sQuery(id+"F0.wireOp",EDGE,"E106.sketch_text.stroke-57"),sQuery(id+"F0.wireOp",EDGE,"E106.sketch_text.stroke-58"),sQuery(id+"F0.wireOp",EDGE,"E106.sketch_text.stroke-59"),sQuery(id+"F0.wireOp",EDGE,"E106.sketch_text.stroke-60"),sQuery(id+"F0.wireOp",EDGE,"E106.sketch_text.stroke-61"),sQuery(id+"F0.wireOp",EDGE,"E106.sketch_text.stroke-62"),sQuery(id+"F0.wireOp",EDGE,"E109.sketch_text.stroke-0"),sQuery(id+"F0.wireOp",EDGE,"E109.sketch_text.stroke-1"),sQuery(id+"F0.wireOp",EDGE,"E109.sketch_text.stroke-2"),sQuery(id+"F0.wireOp",EDGE,"E109.sketch_text.stroke-3"),sQuery(id+"F0.wireOp",EDGE,"E109.sketch_text.stroke-4"),sQuery(id+"F0.wireOp",EDGE,"E109.sketch_text.stroke-5"),sQuery(id+"F0.wireOp",EDGE,"E109.sketch_text.stroke-14"),sQuery(id+"F0.wireOp",EDGE,"E109.sketch_text.stroke-15"),sQuery(id+"F0.wireOp",EDGE,"E109.sketch_text.stroke-16"),sQuery(id+"F0.wireOp",EDGE,"E109.sketch_text.stroke-17"),sQuery(id+"F0.wireOp",EDGE,"E109.sketch_text.stroke-18"),sQuery(id+"F0.wireOp",EDGE,"E109.sketch_text.stroke-19"),sQuery(id+"F0.wireOp",EDGE,"E109.sketch_text.stroke-20"),sQuery(id+"F0.wireOp",EDGE,"E109.sketch_text.stroke-21"),sQuery(id+"F0.wireOp",EDGE,"E109.sketch_text.stroke-22"),sQuery(id+"F0.wireOp",EDGE,"E109.sketch_text.stroke-23"),sQuery(id+"F0.wireOp",EDGE,"E109.sketch_text.stroke-32"),sQuery(id+"F0.wireOp",EDGE,"E109.sketch_text.stroke-33"),sQuery(id+"F0.wireOp",EDGE,"E109.sketch_text.stroke-34"),sQuery(id+"F0.wireOp",EDGE,"E109.sketch_text.stroke-35"),sQuery(id+"F0.wireOp",EDGE,"E109.sketch_text.stroke-36"),sQuery(id+"F0.wireOp",EDGE,"E109.sketch_text.stroke-37"),sQuery(id+"F0.wireOp",EDGE,"E109.sketch_text.stroke-38"),sQuery(id+"F0.wireOp",EDGE,"E109.sketch_text.stroke-39"),sQuery(id+"F0.wireOp",EDGE,"E109.sketch_text.stroke-40"),sQuery(id+"F0.wireOp",EDGE,"E109.sketch_text.stroke-41"),sQuery(id+"F0.wireOp",EDGE,"E109.sketch_text.stroke-42"),sQuery(id+"F0.wireOp",EDGE,"E109.sketch_text.stroke-43"),sQuery(id+"F0.wireOp",EDGE,"E109.sketch_text.stroke-44"),sQuery(id+"F0.wireOp",EDGE,"E109.sketch_text.stroke-45"),sQuery(id+"F0.wireOp",EDGE,"E109.sketch_text.stroke-46"),sQuery(id+"F0.wireOp",EDGE,"E109.sketch_text.stroke-47"),sQuery(id+"F0.wireOp",EDGE,"E109.sketch_text.stroke-48"),sQuery(id+"F0.wireOp",EDGE,"E109.sketch_text.stroke-49"),sQuery(id+"F0.wireOp",EDGE,"E109.sketch_text.stroke-50"),sQuery(id+"F0.wireOp",EDGE,"E109.sketch_text.stroke-51"),sQuery(id+"F0.wireOp",EDGE,"E109.sketch_text.stroke-52"),sQuery(id+"F0.wireOp",EDGE,"E109.sketch_text.stroke-53"),sQuery(id+"F0.wireOp",EDGE,"E109.sketch_text.stroke-54"),sQuery(id+"F0.wireOp",EDGE,"E109.sketch_text.stroke-55"),sQuery(id+"F0.wireOp",EDGE,"E109.sketch_text.stroke-56"),sQuery(id+"F0.wireOp",EDGE,"E109.sketch_text.stroke-65"),sQuery(id+"F0.wireOp",EDGE,"E109.sketch_text.stroke-66"),sQuery(id+"F0.wireOp",EDGE,"E109.sketch_text.stroke-67"),sQuery(id+"F0.wireOp",EDGE,"E109.sketch_text.stroke-68"),sQuery(id+"F0.wireOp",EDGE,"E109.sketch_text.stroke-69"),sQuery(id+"F0.wireOp",EDGE,"E109.sketch_text.stroke-70"),sQuery(id+"F0.wireOp",EDGE,"E109.sketch_text.stroke-71"),sQuery(id+"F0.wireOp",EDGE,"E109.sketch_text.stroke-72"),sQuery(id+"F0.wireOp",EDGE,"E109.sketch_text.stroke-73"),sQuery(id+"F0.wireOp",EDGE,"E109.sketch_text.stroke-74"),sQuery(id+"F0.wireOp",EDGE,"E109.sketch_text.stroke-75"),sQuery(id+"F0.wireOp",EDGE,"E109.sketch_text.stroke-76"),sQuery(id+"F0.wireOp",EDGE,"E109.sketch_text.stroke-77"),sQuery(id+"F0.wireOp",EDGE,"E109.sketch_text.stroke-78"),sQuery(id+"F0.wireOp",EDGE,"E109.sketch_text.stroke-79"),sQuery(id+"F0.wireOp",EDGE,"E109.sketch_text.stroke-80"),sQuery(id+"F0.wireOp",EDGE,"E109.sketch_text.stroke-81"),sQuery(id+"F0.wireOp",EDGE,"E109.sketch_text.stroke-82"),sQuery(id+"F0.wireOp",EDGE,"E109.sketch_text.stroke-83"),sQuery(id+"F0.wireOp",EDGE,"E109.sketch_text.stroke-84"),sQuery(id+"F0.wireOp",EDGE,"E109.sketch_text.stroke-85"),sQuery(id+"F0.wireOp",EDGE,"E109.sketch_text.stroke-86"),sQuery(id+"F0.wireOp",EDGE,"E109.sketch_text.stroke-87"),sQuery(id+"F0.wireOp",EDGE,"E109.sketch_text.stroke-88"),sQuery(id+"F0.wireOp",EDGE,"E109.sketch_text.stroke-89"),sQuery(id+"F0.wireOp",EDGE,"E109.sketch_text.stroke-90"),sQuery(id+"F0.wireOp",EDGE,"E109.sketch_text.stroke-91"),sQuery(id+"F0.wireOp",EDGE,"E109.sketch_text.stroke-92"),sQuery(id+"F0.wireOp",EDGE,"E109.sketch_text.stroke-97"),sQuery(id+"F0.wireOp",EDGE,"E109.sketch_text.stroke-98"),sQuery(id+"F0.wireOp",EDGE,"E109.sketch_text.stroke-99"),sQuery(id+"F0.wireOp",EDGE,"E109.sketch_text.stroke-100"),sQuery(id+"F0.wireOp",EDGE,"E109.sketch_text.stroke-101"),sQuery(id+"F0.wireOp",EDGE,"E109.sketch_text.stroke-102"),sQuery(id+"F0.wireOp",EDGE,"E109.sketch_text.stroke-103"),sQuery(id+"F0.wireOp",EDGE,"E109.sketch_text.stroke-104"),sQuery(id+"F0.wireOp",EDGE,"E109.sketch_text.stroke-105"),sQuery(id+"F0.wireOp",EDGE,"E109.sketch_text.stroke-106"),sQuery(id+"F0.wireOp",EDGE,"E112.sketch_text.stroke-0"),sQuery(id+"F0.wireOp",EDGE,"E112.sketch_text.stroke-1"),sQuery(id+"F0.wireOp",EDGE,"E112.sketch_text.stroke-2"),sQuery(id+"F0.wireOp",EDGE,"E112.sketch_text.stroke-3"),sQuery(id+"F0.wireOp",EDGE,"E112.sketch_text.stroke-4"),sQuery(id+"F0.wireOp",EDGE,"E112.sketch_text.stroke-5"),sQuery(id+"F0.wireOp",EDGE,"E112.sketch_text.stroke-14"),sQuery(id+"F0.wireOp",EDGE,"E112.sketch_text.stroke-15"),sQuery(id+"F0.wireOp",EDGE,"E112.sketch_text.stroke-16"),sQuery(id+"F0.wireOp",EDGE,"E112.sketch_text.stroke-17"),sQuery(id+"F0.wireOp",EDGE,"E112.sketch_text.stroke-18"),sQuery(id+"F0.wireOp",EDGE,"E112.sketch_text.stroke-19"),sQuery(id+"F0.wireOp",EDGE,"E112.sketch_text.stroke-20"),sQuery(id+"F0.wireOp",EDGE,"E112.sketch_text.stroke-21"),sQuery(id+"F0.wireOp",EDGE,"E112.sketch_text.stroke-22"),sQuery(id+"F0.wireOp",EDGE,"E112.sketch_text.stroke-23"),sQuery(id+"F0.wireOp",EDGE,"E112.sketch_text.stroke-32"),sQuery(id+"F0.wireOp",EDGE,"E112.sketch_text.stroke-33"),sQuery(id+"F0.wireOp",EDGE,"E112.sketch_text.stroke-34"),sQuery(id+"F0.wireOp",EDGE,"E112.sketch_text.stroke-35"),sQuery(id+"F0.wireOp",EDGE,"E112.sketch_text.stroke-36"),sQuery(id+"F0.wireOp",EDGE,"E112.sketch_text.stroke-37"),sQuery(id+"F0.wireOp",EDGE,"E112.sketch_text.stroke-38"),sQuery(id+"F0.wireOp",EDGE,"E112.sketch_text.stroke-39"),sQuery(id+"F0.wireOp",EDGE,"E112.sketch_text.stroke-40"),sQuery(id+"F0.wireOp",EDGE,"E112.sketch_text.stroke-41"),sQuery(id+"F0.wireOp",EDGE,"E112.sketch_text.stroke-42"),sQuery(id+"F0.wireOp",EDGE,"E112.sketch_text.stroke-43"),sQuery(id+"F0.wireOp",EDGE,"E112.sketch_text.stroke-44"),sQuery(id+"F0.wireOp",EDGE,"E112.sketch_text.stroke-45"),sQuery(id+"F0.wireOp",EDGE,"E112.sketch_text.stroke-46"),sQuery(id+"F0.wireOp",EDGE,"E112.sketch_text.stroke-47"),sQuery(id+"F0.wireOp",EDGE,"E112.sketch_text.stroke-48"),sQuery(id+"F0.wireOp",EDGE,"E112.sketch_text.stroke-49"),sQuery(id+"F0.wireOp",EDGE,"E112.sketch_text.stroke-50"),sQuery(id+"F0.wireOp",EDGE,"E112.sketch_text.stroke-51"),sQuery(id+"F0.wireOp",EDGE,"E112.sketch_text.stroke-52"),sQuery(id+"F0.wireOp",EDGE,"E112.sketch_text.stroke-53"),sQuery(id+"F0.wireOp",EDGE,"E112.sketch_text.stroke-54"),sQuery(id+"F0.wireOp",EDGE,"E112.sketch_text.stroke-55"),sQuery(id+"F0.wireOp",EDGE,"E112.sketch_text.stroke-56"),sQuery(id+"F0.wireOp",EDGE,"E112.sketch_text.stroke-65"),sQuery(id+"F0.wireOp",EDGE,"E112.sketch_text.stroke-66"),sQuery(id+"F0.wireOp",EDGE,"E112.sketch_text.stroke-67"),sQuery(id+"F0.wireOp",EDGE,"E112.sketch_text.stroke-68"),sQuery(id+"F0.wireOp",EDGE,"E112.sketch_text.stroke-69"),sQuery(id+"F0.wireOp",EDGE,"E112.sketch_text.stroke-70"),sQuery(id+"F0.wireOp",EDGE,"E112.sketch_text.stroke-71"),sQuery(id+"F0.wireOp",EDGE,"E112.sketch_text.stroke-72"),sQuery(id+"F0.wireOp",EDGE,"E112.sketch_text.stroke-73"),sQuery(id+"F0.wireOp",EDGE,"E112.sketch_text.stroke-74"),sQuery(id+"F0.wireOp",EDGE,"E112.sketch_text.stroke-75"),sQuery(id+"F0.wireOp",EDGE,"E112.sketch_text.stroke-76"),sQuery(id+"F0.wireOp",EDGE,"E112.sketch_text.stroke-77"),sQuery(id+"F0.wireOp",EDGE,"E112.sketch_text.stroke-78"),sQuery(id+"F0.wireOp",EDGE,"E112.sketch_text.stroke-79"),sQuery(id+"F0.wireOp",EDGE,"E112.sketch_text.stroke-80"),sQuery(id+"F0.wireOp",EDGE,"E112.sketch_text.stroke-81"),sQuery(id+"F0.wireOp",EDGE,"E112.sketch_text.stroke-82"),sQuery(id+"F0.wireOp",EDGE,"E112.sketch_text.stroke-83"),sQuery(id+"F0.wireOp",EDGE,"E112.sketch_text.stroke-84"),sQuery(id+"F0.wireOp",EDGE,"E112.sketch_text.stroke-85"),sQuery(id+"F0.wireOp",EDGE,"E112.sketch_text.stroke-86"),sQuery(id+"F0.wireOp",EDGE,"E112.sketch_text.stroke-87"),sQuery(id+"F0.wireOp",EDGE,"E112.sketch_text.stroke-88"),sQuery(id+"F0.wireOp",EDGE,"E112.sketch_text.stroke-89"),sQuery(id+"F0.wireOp",EDGE,"E112.sketch_text.stroke-90"),sQuery(id+"F0.wireOp",EDGE,"E112.sketch_text.stroke-91"),sQuery(id+"F0.wireOp",EDGE,"E112.sketch_text.stroke-92"),sQuery(id+"F0.wireOp",EDGE,"E112.sketch_text.stroke-97"),sQuery(id+"F0.wireOp",EDGE,"E112.sketch_text.stroke-98"),sQuery(id+"F0.wireOp",EDGE,"E112.sketch_text.stroke-99"),sQuery(id+"F0.wireOp",EDGE,"E112.sketch_text.stroke-100"),sQuery(id+"F0.wireOp",EDGE,"E112.sketch_text.stroke-101"),sQuery(id+"F0.wireOp",EDGE,"E112.sketch_text.stroke-102"),sQuery(id+"F0.wireOp",EDGE,"E112.sketch_text.stroke-103"),sQuery(id+"F0.wireOp",EDGE,"E112.sketch_text.stroke-104"),sQuery(id+"F0.wireOp",EDGE,"E112.sketch_text.stroke-105"),sQuery(id+"F0.wireOp",EDGE,"E112.sketch_text.stroke-106"),sQuery(id+"F0.wireOp",EDGE,"E112.sketch_text.stroke-107"),sQuery(id+"F0.wireOp",EDGE,"E112.sketch_text.stroke-108"),sQuery(id+"F0.wireOp",EDGE,"E112.sketch_text.stroke-109"),sQuery(id+"F0.wireOp",EDGE,"E112.sketch_text.stroke-110"),sQuery(id+"F0.wireOp",EDGE,"E112.sketch_text.stroke-111"),sQuery(id+"F0.wireOp",EDGE,"E112.sketch_text.stroke-112"),sQuery(id+"F0.wireOp",EDGE,"E112.sketch_text.stroke-113"),sQuery(id+"F0.wireOp",EDGE,"E112.sketch_text.stroke-114"),sQuery(id+"F0.wireOp",EDGE,"E112.sketch_text.stroke-115"),sQuery(id+"F0.wireOp",EDGE,"E112.sketch_text.stroke-116"),sQuery(id+"F0.wireOp",EDGE,"E112.sketch_text.stroke-117"),sQuery(id+"F0.wireOp",EDGE,"E112.sketch_text.stroke-118"),sQuery(id+"F0.wireOp",EDGE,"E112.sketch_text.stroke-119"),sQuery(id+"F0.wireOp",EDGE,"E112.sketch_text.stroke-120"),sQuery(id+"F0.wireOp",EDGE,"E113"),sQuery(id+"F0.wireOp",EDGE,"E114"),sQuery(id+"F0.wireOp",EDGE,"E120"),sQuery(id+"F0.wireOp",EDGE,"E121"),sQuery(id+"F0.wireOp",EDGE,"E124.sketch_text.stroke-0"),sQuery(id+"F0.wireOp",EDGE,"E124.sketch_text.stroke-1"),sQuery(id+"F0.wireOp",EDGE,"E124.sketch_text.stroke-2"),sQuery(id+"F0.wireOp",EDGE,"E124.sketch_text.stroke-3")])]});
            hole(context, id + "F4", {"style" : HoleStyle.C_SINK, "endStyle" : HoleEndStyle.BLIND, "holeDiameter" : 3 * mm, "cSinkDiameter" : 5 * mm, "cSinkAngle" : 90 * degree, "holeDepth" : 12 * mm, "isTappedThrough" : true, "tappedDepth" : 12 * mm, "tapClearance" : 3, "locations" : qUnion([Q0, Q1, Q2, Q3, Q4, Q5]), "scope" : qUnion([Q6])});
        }
    });
